# Revit family: ATK_ST_SFD_Pile (NEW)
name_source: partatom
category: Structural Foundations
units: mm (PartAtom-declared; Revit-internal decimal feet)

## family parameters
Always vertical = Yes
Cap = No
Cut with Voids When Loaded = No
Material for Model Behavior = Concrete
Shared = Yes
Work Plane-Based = No

## types (170) — shared parameters
31 = Pile Type-30
Assembly Code = A1020130
Minimum Embedment = 75 mm
Pile Type = Pile Type-30
Type Comments = Z2
Width = 1000 mm  [stored 3.28084 ft]

## per-type parameters (varying)
- ATK_P3A_1000_Diameter_Pile: ATK_1.25DIA_Circle_Radius=1250 mm  [stored 4.10105 ft]; ATK_2.5_DIA_Circle_Radius=2500 mm  [stored 8.2021 ft]; ATK_Pile_DIA=1000 mm  [stored 3.28084 ft]; Band Width 2=240 mm; Band Width 3=100 mm  [stored 0.328084 ft]; Depth=15000 mm  [stored 49.2126 ft]; Pile Type 01=Yes; Pile Type 02=No; Pile Type 03=No; Pile Type 04=No; Pile Type 05=No; Pile Type 06=No; Pile Type 07=No; Pile Type 08=No; Pile Type 09=No; Pile Type 10=No; Pile Type 11=No; Pile Type 12=No; Pile Type 13=No; Pile Type 14=No; Pile Type 15=No; Pile Type 16=No; Pile Type 17=No; Pile Type 18=No; Pile Type 19=No; Pile Type 20=No; Pile Type 21=No; Pile Type 22=No; Pile Type 23=No; Pile Type 24=No; Pile Type 25=No; Pile Type 26=No; Pile Type 27=No; Pile Type 28=No; Pile Type 29=No; Pile Type 30=No; Pile Type 31=Yes; Pile Type-32=No; Pile Type-33=No; Pile Type-34=No; Pile Type-35=No; Pile Type-36=No; Pile Type-37=Yes; Pile Type-38=No; Pile Type-39=No; Pile Type-40=No; Pile Type-41=No; Pile Type-42=No; Pile Type-43=No; Pile Type-44=No; Pile Type-45=No; Pile Type-46=No; Pile Type-47=No; Pile Type-48=No; Pile Type-49=No; Pile Type-50=No; Pile Type-51=No; Pile Type-52=No; Pile Type-53=No; Pile Type-54=No; Radius=500 mm  [stored 1.64042 ft]; Radius/2=250 mm  [stored 0.82021 ft]; band width=167 mm
- ATK_P7A_1000_Diameter_Pile: ATK_1.25DIA_Circle_Radius=1250 mm  [stored 4.10105 ft]; ATK_2.5_DIA_Circle_Radius=2500 mm  [stored 8.2021 ft]; ATK_Pile_DIA=1000 mm  [stored 3.28084 ft]; Band Width 2=240 mm; Band Width 3=100 mm  [stored 0.328084 ft]; Depth=19000 mm; Pile Type 01=No; Pile Type 02=No; Pile Type 03=No; Pile Type 04=No; Pile Type 05=No; Pile Type 06=No; Pile Type 07=No; Pile Type 08=No; Pile Type 09=No; Pile Type 10=No; Pile Type 11=No; Pile Type 12=No; Pile Type 13=No; Pile Type 14=No; Pile Type 15=No; Pile Type 16=No; Pile Type 17=No; Pile Type 18=No; Pile Type 19=No; Pile Type 20=No; Pile Type 21=No; Pile Type 22=No; Pile Type 23=No; Pile Type 24=No; Pile Type 25=Yes; Pile Type 26=No; Pile Type 27=No; Pile Type 28=No; Pile Type 29=No; Pile Type 30=No; Pile Type 31=Yes; Pile Type-32=No; Pile Type-33=No; Pile Type-34=No; Pile Type-35=No; Pile Type-36=No; Pile Type-37=Yes; Pile Type-38=No; Pile Type-39=No; Pile Type-40=No; Pile Type-41=No; Pile Type-42=No; Pile Type-43=No; Pile Type-44=No; Pile Type-45=No; Pile Type-46=No; Pile Type-47=No; Pile Type-48=No; Pile Type-49=No; Pile Type-50=No; Pile Type-51=No; Pile Type-52=No; Pile Type-53=No; Pile Type-54=No; Radius=500 mm  [stored 1.64042 ft]; Radius/2=250 mm  [stored 0.82021 ft]; band width=167 mm
- ATK_P8A_1000_Diameter_Pile: ATK_1.25DIA_Circle_Radius=1250 mm  [stored 4.10105 ft]; ATK_2.5_DIA_Circle_Radius=2500 mm  [stored 8.2021 ft]; ATK_Pile_DIA=1000 mm  [stored 3.28084 ft]; Band Width 2=240 mm; Band Width 3=100 mm  [stored 0.328084 ft]; Depth=20000 mm  [stored 65.6168 ft]; Pile Type 01=No; Pile Type 02=No; Pile Type 03=No; Pile Type 04=No; Pile Type 05=No; Pile Type 06=No; Pile Type 07=No; Pile Type 08=No; Pile Type 09=No; Pile Type 10=No; Pile Type 11=No; Pile Type 12=No; Pile Type 13=No; Pile Type 14=No; Pile Type 15=No; Pile Type 16=No; Pile Type 17=No; Pile Type 18=No; Pile Type 19=No; Pile Type 20=No; Pile Type 21=No; Pile Type 22=No; Pile Type 23=No; Pile Type 24=No; Pile Type 25=No; Pile Type 26=No; Pile Type 27=No; Pile Type 28=No; Pile Type 29=Yes; Pile Type 30=No; Pile Type 31=Yes; Pile Type-32=No; Pile Type-33=No; Pile Type-34=No; Pile Type-35=No; Pile Type-36=No; Pile Type-37=Yes; Pile Type-38=No; Pile Type-39=No; Pile Type-40=No; Pile Type-41=No; Pile Type-42=No; Pile Type-43=No; Pile Type-44=No; Pile Type-45=No; Pile Type-46=No; Pile Type-47=No; Pile Type-48=No; Pile Type-49=No; Pile Type-50=No; Pile Type-51=No; Pile Type-52=No; Pile Type-53=No; Pile Type-54=No; Radius=500 mm  [stored 1.64042 ft]; Radius/2=250 mm  [stored 0.82021 ft]; band width=167 mm
- ATK_P9A_1000_Diameter_Pile 2: ATK_1.25DIA_Circle_Radius=1250 mm  [stored 4.10105 ft]; ATK_2.5_DIA_Circle_Radius=2500 mm  [stored 8.2021 ft]; ATK_Pile_DIA=1000 mm  [stored 3.28084 ft]; Band Width 2=240 mm; Band Width 3=100 mm  [stored 0.328084 ft]; Depth=21000 mm  [stored 68.8976 ft]; Pile Type 01=No; Pile Type 02=No; Pile Type 03=No; Pile Type 04=No; Pile Type 05=No; Pile Type 06=No; Pile Type 07=No; Pile Type 08=No; Pile Type 09=No; Pile Type 10=No; Pile Type 11=No; Pile Type 12=No; Pile Type 13=No; Pile Type 14=No; Pile Type 15=No; Pile Type 16=No; Pile Type 17=No; Pile Type 18=No; Pile Type 19=No; Pile Type 20=No; Pile Type 21=No; Pile Type 22=No; Pile Type 23=Yes; Pile Type 24=No; Pile Type 25=No; Pile Type 26=No; Pile Type 27=No; Pile Type 28=No; Pile Type 29=No; Pile Type 30=No; Pile Type 31=Yes; Pile Type-32=No; Pile Type-33=No; Pile Type-34=No; Pile Type-35=No; Pile Type-36=No; Pile Type-37=Yes; Pile Type-38=No; Pile Type-39=No; Pile Type-40=No; Pile Type-41=No; Pile Type-42=No; Pile Type-43=No; Pile Type-44=No; Pile Type-45=No; Pile Type-46=No; Pile Type-47=No; Pile Type-48=No; Pile Type-49=No; Pile Type-50=No; Pile Type-51=No; Pile Type-52=No; Pile Type-53=No; Pile Type-54=No; Radius=500 mm  [stored 1.64042 ft]; Radius/2=250 mm  [stored 0.82021 ft]; band width=167 mm
- ATK_P4B_900_Diameter_Pile 6: ATK_1.25DIA_Circle_Radius=1125 mm; ATK_2.5_DIA_Circle_Radius=2250 mm; ATK_Pile_DIA=900 mm  [stored 2.95276 ft]; Band Width 2=215 mm; Band Width 3=90 mm; Depth=16000 mm  [stored 52.4934 ft]; Pile Type 01=No; Pile Type 02=Yes; Pile Type 03=No; Pile Type 04=No; Pile Type 05=No; Pile Type 06=No; Pile Type 07=No; Pile Type 08=No; Pile Type 09=No; Pile Type 10=No; Pile Type 11=No; Pile Type 12=No; Pile Type 13=No; Pile Type 14=No; Pile Type 15=No; Pile Type 16=No; Pile Type 17=No; Pile Type 18=No; Pile Type 19=No; Pile Type 20=No; Pile Type 21=No; Pile Type 22=No; Pile Type 23=No; Pile Type 24=No; Pile Type 25=No; Pile Type 26=No; Pile Type 27=No; Pile Type 28=No; Pile Type 29=No; Pile Type 30=No; Pile Type 31=Yes; Pile Type-32=No; Pile Type-33=No; Pile Type-34=No; Pile Type-35=No; Pile Type-36=No; Pile Type-37=Yes; Pile Type-38=No; Pile Type-39=No; Pile Type-40=No; Pile Type-41=No; Pile Type-42=No; Pile Type-43=No; Pile Type-44=No; Pile Type-45=No; Pile Type-46=No; Pile Type-47=No; Pile Type-48=No; Pile Type-49=No; Pile Type-50=No; Pile Type-51=No; Pile Type-52=No; Pile Type-53=No; Pile Type-54=No; Radius=450 mm  [stored 1.47638 ft]; Radius/2=225 mm  [stored 0.738189 ft]; band width=150 mm
- ATK_P3B_900_Diameter_Pile 6: ATK_1.25DIA_Circle_Radius=1125 mm; ATK_2.5_DIA_Circle_Radius=2250 mm; ATK_Pile_DIA=900 mm  [stored 2.95276 ft]; Band Width 2=215 mm; Band Width 3=90 mm; Depth=15000 mm  [stored 49.2126 ft]; Pile Type 01=No; Pile Type 02=No; Pile Type 03=No; Pile Type 04=No; Pile Type 05=No; Pile Type 06=No; Pile Type 07=Yes; Pile Type 08=No; Pile Type 09=No; Pile Type 10=No; Pile Type 11=No; Pile Type 12=No; Pile Type 13=No; Pile Type 14=No; Pile Type 15=No; Pile Type 16=No; Pile Type 17=No; Pile Type 18=No; Pile Type 19=No; Pile Type 20=No; Pile Type 21=No; Pile Type 22=No; Pile Type 23=No; Pile Type 24=No; Pile Type 25=No; Pile Type 26=No; Pile Type 27=No; Pile Type 28=No; Pile Type 29=No; Pile Type 30=No; Pile Type 31=Yes; Pile Type-32=No; Pile Type-33=No; Pile Type-34=No; Pile Type-35=No; Pile Type-36=No; Pile Type-37=Yes; Pile Type-38=No; Pile Type-39=No; Pile Type-40=No; Pile Type-41=No; Pile Type-42=No; Pile Type-43=No; Pile Type-44=No; Pile Type-45=No; Pile Type-46=No; Pile Type-47=No; Pile Type-48=No; Pile Type-49=No; Pile Type-50=No; Pile Type-51=No; Pile Type-52=No; Pile Type-53=No; Pile Type-54=No; Radius=450 mm  [stored 1.47638 ft]; Radius/2=225 mm  [stored 0.738189 ft]; band width=150 mm
- ATK_P2B_900_Diameter_Pile 5: ATK_1.25DIA_Circle_Radius=1125 mm; ATK_2.5_DIA_Circle_Radius=2250 mm; ATK_Pile_DIA=900 mm  [stored 2.95276 ft]; Band Width 2=215 mm; Band Width 3=90 mm; Depth=14000 mm  [stored 45.9318 ft]; Pile Type 01=No; Pile Type 02=No; Pile Type 03=Yes; Pile Type 04=No; Pile Type 05=No; Pile Type 06=No; Pile Type 07=No; Pile Type 08=No; Pile Type 09=No; Pile Type 10=No; Pile Type 11=No; Pile Type 12=No; Pile Type 13=No; Pile Type 14=No; Pile Type 15=No; Pile Type 16=No; Pile Type 17=No; Pile Type 18=No; Pile Type 19=No; Pile Type 20=No; Pile Type 21=No; Pile Type 22=No; Pile Type 23=No; Pile Type 24=No; Pile Type 25=No; Pile Type 26=No; Pile Type 27=No; Pile Type 28=No; Pile Type 29=No; Pile Type 30=No; Pile Type 31=Yes; Pile Type-32=No; Pile Type-33=No; Pile Type-34=No; Pile Type-35=No; Pile Type-36=No; Pile Type-37=Yes; Pile Type-38=No; Pile Type-39=No; Pile Type-40=No; Pile Type-41=No; Pile Type-42=No; Pile Type-43=No; Pile Type-44=No; Pile Type-45=No; Pile Type-46=No; Pile Type-47=No; Pile Type-48=No; Pile Type-49=No; Pile Type-50=No; Pile Type-51=No; Pile Type-52=No; Pile Type-53=No; Pile Type-54=No; Radius=450 mm  [stored 1.47638 ft]; Radius/2=225 mm  [stored 0.738189 ft]; band width=150 mm
- ATK_P6C_750_Diameter_Pile 2: ATK_1.25DIA_Circle_Radius=938 mm; ATK_2.5_DIA_Circle_Radius=1875 mm  [stored 6.15157 ft]; ATK_Pile_DIA=750 mm  [stored 2.46063 ft]; Band Width 2=178 mm; Band Width 3=75 mm; Depth=18000 mm; Pile Type 01=No; Pile Type 02=No; Pile Type 03=No; Pile Type 04=No; Pile Type 05=No; Pile Type 06=Yes; Pile Type 07=No; Pile Type 08=No; Pile Type 09=No; Pile Type 10=No; Pile Type 11=No; Pile Type 12=No; Pile Type 13=No; Pile Type 14=No; Pile Type 15=No; Pile Type 16=No; Pile Type 17=No; Pile Type 18=No; Pile Type 19=No; Pile Type 20=No; Pile Type 21=No; Pile Type 22=No; Pile Type 23=No; Pile Type 24=No; Pile Type 25=No; Pile Type 26=No; Pile Type 27=No; Pile Type 28=No; Pile Type 29=No; Pile Type 30=No; Pile Type 31=Yes; Pile Type-32=No; Pile Type-33=No; Pile Type-34=No; Pile Type-35=No; Pile Type-36=No; Pile Type-37=Yes; Pile Type-38=No; Pile Type-39=No; Pile Type-40=No; Pile Type-41=No; Pile Type-42=No; Pile Type-43=No; Pile Type-44=No; Pile Type-45=No; Pile Type-46=No; Pile Type-47=No; Pile Type-48=No; Pile Type-49=No; Pile Type-50=No; Pile Type-51=No; Pile Type-52=No; Pile Type-53=No; Pile Type-54=No; Radius=375 mm  [stored 1.23031 ft]; Radius/2=188 mm; band width=125 mm  [stored 0.410105 ft]
- ATK_P5C_750_Diameter_Pile 2: ATK_1.25DIA_Circle_Radius=938 mm; ATK_2.5_DIA_Circle_Radius=1875 mm  [stored 6.15157 ft]; ATK_Pile_DIA=750 mm  [stored 2.46063 ft]; Band Width 2=178 mm; Band Width 3=75 mm; Depth=17000 mm; Pile Type 01=No; Pile Type 02=No; Pile Type 03=No; Pile Type 04=No; Pile Type 05=No; Pile Type 06=No; Pile Type 07=No; Pile Type 08=Yes; Pile Type 09=No; Pile Type 10=No; Pile Type 11=No; Pile Type 12=No; Pile Type 13=No; Pile Type 14=No; Pile Type 15=No; Pile Type 16=No; Pile Type 17=No; Pile Type 18=No; Pile Type 19=No; Pile Type 20=No; Pile Type 21=No; Pile Type 22=No; Pile Type 23=No; Pile Type 24=No; Pile Type 25=No; Pile Type 26=No; Pile Type 27=No; Pile Type 28=No; Pile Type 29=No; Pile Type 30=No; Pile Type 31=Yes; Pile Type-32=No; Pile Type-33=No; Pile Type-34=No; Pile Type-35=No; Pile Type-36=No; Pile Type-37=Yes; Pile Type-38=No; Pile Type-39=No; Pile Type-40=No; Pile Type-41=No; Pile Type-42=No; Pile Type-43=No; Pile Type-44=No; Pile Type-45=No; Pile Type-46=No; Pile Type-47=No; Pile Type-48=No; Pile Type-49=No; Pile Type-50=No; Pile Type-51=No; Pile Type-52=No; Pile Type-53=No; Pile Type-54=No; Radius=375 mm  [stored 1.23031 ft]; Radius/2=188 mm; band width=125 mm  [stored 0.410105 ft]
- ATK_P4C_750_Diameter_Pile 2: ATK_1.25DIA_Circle_Radius=938 mm; ATK_2.5_DIA_Circle_Radius=1875 mm  [stored 6.15157 ft]; ATK_Pile_DIA=750 mm  [stored 2.46063 ft]; Band Width 2=178 mm; Band Width 3=75 mm; Depth=16000 mm  [stored 52.4934 ft]; Pile Type 01=No; Pile Type 02=No; Pile Type 03=No; Pile Type 04=No; Pile Type 05=No; Pile Type 06=No; Pile Type 07=No; Pile Type 08=No; Pile Type 09=No; Pile Type 10=No; Pile Type 11=No; Pile Type 12=Yes; Pile Type 13=No; Pile Type 14=No; Pile Type 15=No; Pile Type 16=No; Pile Type 17=No; Pile Type 18=No; Pile Type 19=No; Pile Type 20=No; Pile Type 21=No; Pile Type 22=No; Pile Type 23=No; Pile Type 24=No; Pile Type 25=No; Pile Type 26=No; Pile Type 27=No; Pile Type 28=No; Pile Type 29=No; Pile Type 30=No; Pile Type 31=Yes; Pile Type-32=No; Pile Type-33=No; Pile Type-34=No; Pile Type-35=No; Pile Type-36=No; Pile Type-37=Yes; Pile Type-38=No; Pile Type-39=No; Pile Type-40=No; Pile Type-41=No; Pile Type-42=No; Pile Type-43=No; Pile Type-44=No; Pile Type-45=No; Pile Type-46=No; Pile Type-47=No; Pile Type-48=No; Pile Type-49=No; Pile Type-50=No; Pile Type-51=No; Pile Type-52=No; Pile Type-53=No; Pile Type-54=No; Radius=375 mm  [stored 1.23031 ft]; Radius/2=188 mm; band width=125 mm  [stored 0.410105 ft]
- ATK_P3C_750_Diameter_Pile 2: ATK_1.25DIA_Circle_Radius=938 mm; ATK_2.5_DIA_Circle_Radius=1875 mm  [stored 6.15157 ft]; ATK_Pile_DIA=750 mm  [stored 2.46063 ft]; Band Width 2=178 mm; Band Width 3=75 mm; Depth=15000 mm  [stored 49.2126 ft]; Pile Type 01=No; Pile Type 02=No; Pile Type 03=No; Pile Type 04=No; Pile Type 05=No; Pile Type 06=No; Pile Type 07=No; Pile Type 08=No; Pile Type 09=No; Pile Type 10=No; Pile Type 11=No; Pile Type 12=No; Pile Type 13=Yes; Pile Type 14=No; Pile Type 15=No; Pile Type 16=No; Pile Type 17=No; Pile Type 18=No; Pile Type 19=No; Pile Type 20=No; Pile Type 21=No; Pile Type 22=No; Pile Type 23=No; Pile Type 24=No; Pile Type 25=No; Pile Type 26=No; Pile Type 27=No; Pile Type 28=No; Pile Type 29=No; Pile Type 30=No; Pile Type 31=Yes; Pile Type-32=No; Pile Type-33=No; Pile Type-34=No; Pile Type-35=No; Pile Type-36=No; Pile Type-37=Yes; Pile Type-38=No; Pile Type-39=No; Pile Type-40=No; Pile Type-41=No; Pile Type-42=No; Pile Type-43=No; Pile Type-44=No; Pile Type-45=No; Pile Type-46=No; Pile Type-47=No; Pile Type-48=No; Pile Type-49=No; Pile Type-50=No; Pile Type-51=No; Pile Type-52=No; Pile Type-53=No; Pile Type-54=No; Radius=375 mm  [stored 1.23031 ft]; Radius/2=188 mm; band width=125 mm  [stored 0.410105 ft]
- ATK_P2C_750_Diameter_Pile: ATK_1.25DIA_Circle_Radius=938 mm; ATK_2.5_DIA_Circle_Radius=1875 mm  [stored 6.15157 ft]; ATK_Pile_DIA=750 mm  [stored 2.46063 ft]; Band Width 2=178 mm; Band Width 3=75 mm; Depth=14000 mm  [stored 45.9318 ft]; Pile Type 01=No; Pile Type 02=No; Pile Type 03=No; Pile Type 04=No; Pile Type 05=No; Pile Type 06=No; Pile Type 07=No; Pile Type 08=No; Pile Type 09=No; Pile Type 10=No; Pile Type 11=No; Pile Type 12=No; Pile Type 13=No; Pile Type 14=Yes; Pile Type 15=No; Pile Type 16=No; Pile Type 17=No; Pile Type 18=No; Pile Type 19=No; Pile Type 20=No; Pile Type 21=No; Pile Type 22=No; Pile Type 23=No; Pile Type 24=No; Pile Type 25=No; Pile Type 26=No; Pile Type 27=No; Pile Type 28=No; Pile Type 29=No; Pile Type 30=No; Pile Type 31=Yes; Pile Type-32=No; Pile Type-33=No; Pile Type-34=No; Pile Type-35=No; Pile Type-36=No; Pile Type-37=Yes; Pile Type-38=No; Pile Type-39=No; Pile Type-40=No; Pile Type-41=No; Pile Type-42=No; Pile Type-43=No; Pile Type-44=No; Pile Type-45=No; Pile Type-46=No; Pile Type-47=No; Pile Type-48=No; Pile Type-49=No; Pile Type-50=No; Pile Type-51=No; Pile Type-52=No; Pile Type-53=No; Pile Type-54=No; Radius=375 mm  [stored 1.23031 ft]; Radius/2=188 mm; band width=125 mm  [stored 0.410105 ft]
- ATK_P5B_900_Diameter_Pile 3: ATK_1.25DIA_Circle_Radius=1125 mm; ATK_2.5_DIA_Circle_Radius=2250 mm; ATK_Pile_DIA=900 mm  [stored 2.95276 ft]; Band Width 2=215 mm; Band Width 3=90 mm; Depth=17000 mm; Pile Type 01=No; Pile Type 02=No; Pile Type 03=No; Pile Type 04=No; Pile Type 05=No; Pile Type 06=No; Pile Type 07=No; Pile Type 08=No; Pile Type 09=No; Pile Type 10=No; Pile Type 11=No; Pile Type 12=No; Pile Type 13=No; Pile Type 14=No; Pile Type 15=No; Pile Type 16=No; Pile Type 17=No; Pile Type 18=No; Pile Type 19=No; Pile Type 20=Yes; Pile Type 21=No; Pile Type 22=No; Pile Type 23=No; Pile Type 24=No; Pile Type 25=No; Pile Type 26=No; Pile Type 27=No; Pile Type 28=No; Pile Type 29=No; Pile Type 30=No; Pile Type 31=Yes; Pile Type-32=No; Pile Type-33=No; Pile Type-34=No; Pile Type-35=No; Pile Type-36=No; Pile Type-37=Yes; Pile Type-38=No; Pile Type-39=No; Pile Type-40=No; Pile Type-41=No; Pile Type-42=No; Pile Type-43=No; Pile Type-44=No; Pile Type-45=No; Pile Type-46=No; Pile Type-47=No; Pile Type-48=No; Pile Type-49=No; Pile Type-50=No; Pile Type-51=No; Pile Type-52=No; Pile Type-53=No; Pile Type-54=No; Radius=450 mm  [stored 1.47638 ft]; Radius/2=225 mm  [stored 0.738189 ft]; band width=150 mm
- ATK_P6A_1000_Diameter_Pile 2: ATK_1.25DIA_Circle_Radius=1250 mm  [stored 4.10105 ft]; ATK_2.5_DIA_Circle_Radius=2500 mm  [stored 8.2021 ft]; ATK_Pile_DIA=1000 mm  [stored 3.28084 ft]; Band Width 2=240 mm; Band Width 3=100 mm  [stored 0.328084 ft]; Depth=18000 mm; Pile Type 01=No; Pile Type 02=No; Pile Type 03=No; Pile Type 04=No; Pile Type 05=No; Pile Type 06=No; Pile Type 07=No; Pile Type 08=No; Pile Type 09=No; Pile Type 10=No; Pile Type 11=No; Pile Type 12=No; Pile Type 13=No; Pile Type 14=No; Pile Type 15=No; Pile Type 16=Yes; Pile Type 17=No; Pile Type 18=No; Pile Type 19=No; Pile Type 20=No; Pile Type 21=No; Pile Type 22=No; Pile Type 23=No; Pile Type 24=No; Pile Type 25=No; Pile Type 26=No; Pile Type 27=No; Pile Type 28=No; Pile Type 29=No; Pile Type 30=No; Pile Type 31=Yes; Pile Type-32=No; Pile Type-33=No; Pile Type-34=No; Pile Type-35=No; Pile Type-36=No; Pile Type-37=Yes; Pile Type-38=No; Pile Type-39=No; Pile Type-40=No; Pile Type-41=No; Pile Type-42=No; Pile Type-43=No; Pile Type-44=No; Pile Type-45=No; Pile Type-46=No; Pile Type-47=No; Pile Type-48=No; Pile Type-49=No; Pile Type-50=No; Pile Type-51=No; Pile Type-52=No; Pile Type-53=No; Pile Type-54=No; Radius=500 mm  [stored 1.64042 ft]; Radius/2=250 mm  [stored 0.82021 ft]; band width=167 mm
- ATK_P5A_1000_Diameter_Pile 2: ATK_1.25DIA_Circle_Radius=1250 mm  [stored 4.10105 ft]; ATK_2.5_DIA_Circle_Radius=2500 mm  [stored 8.2021 ft]; ATK_Pile_DIA=1000 mm  [stored 3.28084 ft]; Band Width 2=240 mm; Band Width 3=100 mm  [stored 0.328084 ft]; Depth=17000 mm; Pile Type 01=No; Pile Type 02=No; Pile Type 03=No; Pile Type 04=No; Pile Type 05=No; Pile Type 06=No; Pile Type 07=No; Pile Type 08=No; Pile Type 09=No; Pile Type 10=No; Pile Type 11=No; Pile Type 12=No; Pile Type 13=No; Pile Type 14=No; Pile Type 15=No; Pile Type 16=No; Pile Type 17=No; Pile Type 18=No; Pile Type 19=No; Pile Type 20=No; Pile Type 21=No; Pile Type 22=No; Pile Type 23=No; Pile Type 24=No; Pile Type 25=No; Pile Type 26=No; Pile Type 27=Yes; Pile Type 28=No; Pile Type 29=No; Pile Type 30=No; Pile Type 31=Yes; Pile Type-32=No; Pile Type-33=No; Pile Type-34=No; Pile Type-35=No; Pile Type-36=No; Pile Type-37=Yes; Pile Type-38=No; Pile Type-39=No; Pile Type-40=No; Pile Type-41=No; Pile Type-42=No; Pile Type-43=No; Pile Type-44=No; Pile Type-45=No; Pile Type-46=No; Pile Type-47=No; Pile Type-48=No; Pile Type-49=No; Pile Type-50=No; Pile Type-51=No; Pile Type-52=No; Pile Type-53=No; Pile Type-54=No; Radius=500 mm  [stored 1.64042 ft]; Radius/2=250 mm  [stored 0.82021 ft]; band width=167 mm
- ATK_P4A_1000_Diameter_Pile 2: ATK_1.25DIA_Circle_Radius=1250 mm  [stored 4.10105 ft]; ATK_2.5_DIA_Circle_Radius=2500 mm  [stored 8.2021 ft]; ATK_Pile_DIA=1000 mm  [stored 3.28084 ft]; Band Width 2=240 mm; Band Width 3=100 mm  [stored 0.328084 ft]; Depth=16000 mm  [stored 52.4934 ft]; Pile Type 01=No; Pile Type 02=No; Pile Type 03=No; Pile Type 04=No; Pile Type 05=No; Pile Type 06=No; Pile Type 07=No; Pile Type 08=No; Pile Type 09=No; Pile Type 10=No; Pile Type 11=No; Pile Type 12=No; Pile Type 13=No; Pile Type 14=No; Pile Type 15=No; Pile Type 16=No; Pile Type 17=No; Pile Type 18=No; Pile Type 19=No; Pile Type 20=No; Pile Type 21=No; Pile Type 22=No; Pile Type 23=No; Pile Type 24=No; Pile Type 25=No; Pile Type 26=No; Pile Type 27=No; Pile Type 28=Yes; Pile Type 29=No; Pile Type 30=No; Pile Type 31=Yes; Pile Type-32=No; Pile Type-33=No; Pile Type-34=No; Pile Type-35=No; Pile Type-36=No; Pile Type-37=Yes; Pile Type-38=No; Pile Type-39=No; Pile Type-40=No; Pile Type-41=No; Pile Type-42=No; Pile Type-43=No; Pile Type-44=No; Pile Type-45=No; Pile Type-46=No; Pile Type-47=No; Pile Type-48=No; Pile Type-49=No; Pile Type-50=No; Pile Type-51=No; Pile Type-52=No; Pile Type-53=No; Pile Type-54=No; Radius=500 mm  [stored 1.64042 ft]; Radius/2=250 mm  [stored 0.82021 ft]; band width=167 mm
- ATK_P4B2_900_Diameter_Pile 7: ATK_1.25DIA_Circle_Radius=1125 mm; ATK_2.5_DIA_Circle_Radius=2250 mm; ATK_Pile_DIA=900 mm  [stored 2.95276 ft]; Band Width 2=215 mm; Band Width 3=90 mm; Depth=16000 mm  [stored 52.4934 ft]; Pile Type 01=No; Pile Type 02=No; Pile Type 03=No; Pile Type 04=No; Pile Type 05=No; Pile Type 06=No; Pile Type 07=No; Pile Type 08=No; Pile Type 09=No; Pile Type 10=No; Pile Type 11=Yes; Pile Type 12=Yes; Pile Type 13=No; Pile Type 14=No; Pile Type 15=No; Pile Type 16=No; Pile Type 17=No; Pile Type 18=No; Pile Type 19=No; Pile Type 20=No; Pile Type 21=No; Pile Type 22=No; Pile Type 23=No; Pile Type 24=No; Pile Type 25=No; Pile Type 26=No; Pile Type 27=No; Pile Type 28=No; Pile Type 29=No; Pile Type 30=No; Pile Type 31=Yes; Pile Type-32=No; Pile Type-33=No; Pile Type-34=No; Pile Type-35=No; Pile Type-36=No; Pile Type-37=Yes; Pile Type-38=No; Pile Type-39=No; Pile Type-40=No; Pile Type-41=No; Pile Type-42=No; Pile Type-43=No; Pile Type-44=No; Pile Type-45=No; Pile Type-46=No; Pile Type-47=No; Pile Type-48=No; Pile Type-49=No; Pile Type-50=No; Pile Type-51=No; Pile Type-52=No; Pile Type-53=No; Pile Type-54=No; Radius=450 mm  [stored 1.47638 ft]; Radius/2=225 mm  [stored 0.738189 ft]; band width=150 mm
- ATK_P5B2_900_Diameter_Pile 4: ATK_1.25DIA_Circle_Radius=1125 mm; ATK_2.5_DIA_Circle_Radius=2250 mm; ATK_Pile_DIA=900 mm  [stored 2.95276 ft]; Band Width 2=215 mm; Band Width 3=90 mm; Depth=17000 mm; Pile Type 01=No; Pile Type 02=No; Pile Type 03=No; Pile Type 04=No; Pile Type 05=No; Pile Type 06=No; Pile Type 07=No; Pile Type 08=No; Pile Type 09=No; Pile Type 10=No; Pile Type 11=No; Pile Type 12=No; Pile Type 13=No; Pile Type 14=No; Pile Type 15=No; Pile Type 16=No; Pile Type 17=No; Pile Type 18=No; Pile Type 19=No; Pile Type 20=No; Pile Type 21=No; Pile Type 22=No; Pile Type 23=No; Pile Type 24=No; Pile Type 25=No; Pile Type 26=Yes; Pile Type 27=No; Pile Type 28=No; Pile Type 29=No; Pile Type 30=No; Pile Type 31=Yes; Pile Type-32=No; Pile Type-33=No; Pile Type-34=No; Pile Type-35=No; Pile Type-36=No; Pile Type-37=Yes; Pile Type-38=No; Pile Type-39=No; Pile Type-40=No; Pile Type-41=No; Pile Type-42=No; Pile Type-43=No; Pile Type-44=No; Pile Type-45=No; Pile Type-46=No; Pile Type-47=No; Pile Type-48=No; Pile Type-49=No; Pile Type-50=No; Pile Type-51=No; Pile Type-52=No; Pile Type-53=No; Pile Type-54=No; Radius=450 mm  [stored 1.47638 ft]; Radius/2=225 mm  [stored 0.738189 ft]; band width=150 mm
- ATK_P5A4_1000_Diameter_Pile 4: ATK_1.25DIA_Circle_Radius=1250 mm  [stored 4.10105 ft]; ATK_2.5_DIA_Circle_Radius=2500 mm  [stored 8.2021 ft]; ATK_Pile_DIA=1000 mm  [stored 3.28084 ft]; Band Width 2=240 mm; Band Width 3=100 mm  [stored 0.328084 ft]; Depth=17000 mm; Pile Type 01=No; Pile Type 02=No; Pile Type 03=No; Pile Type 04=No; Pile Type 05=No; Pile Type 06=No; Pile Type 07=No; Pile Type 08=No; Pile Type 09=No; Pile Type 10=No; Pile Type 11=Yes; Pile Type 12=No; Pile Type 13=No; Pile Type 14=No; Pile Type 15=No; Pile Type 16=No; Pile Type 17=No; Pile Type 18=No; Pile Type 19=No; Pile Type 20=No; Pile Type 21=No; Pile Type 22=No; Pile Type 23=No; Pile Type 24=No; Pile Type 25=No; Pile Type 26=No; Pile Type 27=No; Pile Type 28=No; Pile Type 29=No; Pile Type 30=No; Pile Type 31=Yes; Pile Type-32=No; Pile Type-33=No; Pile Type-34=No; Pile Type-35=No; Pile Type-36=No; Pile Type-37=Yes; Pile Type-38=No; Pile Type-39=No; Pile Type-40=No; Pile Type-41=No; Pile Type-42=No; Pile Type-43=No; Pile Type-44=No; Pile Type-45=No; Pile Type-46=No; Pile Type-47=No; Pile Type-48=No; Pile Type-49=No; Pile Type-50=No; Pile Type-51=No; Pile Type-52=No; Pile Type-53=No; Pile Type-54=No; Radius=500 mm  [stored 1.64042 ft]; Radius/2=250 mm  [stored 0.82021 ft]; band width=167 mm
- ATK_P6A1_1000_Diameter_Pile 3: ATK_1.25DIA_Circle_Radius=1250 mm  [stored 4.10105 ft]; ATK_2.5_DIA_Circle_Radius=2500 mm  [stored 8.2021 ft]; ATK_Pile_DIA=1000 mm  [stored 3.28084 ft]; Band Width 2=240 mm; Band Width 3=100 mm  [stored 0.328084 ft]; Depth=18000 mm; Pile Type 01=No; Pile Type 02=No; Pile Type 03=No; Pile Type 04=No; Pile Type 05=No; Pile Type 06=No; Pile Type 07=No; Pile Type 08=No; Pile Type 09=No; Pile Type 10=No; Pile Type 11=No; Pile Type 12=No; Pile Type 13=No; Pile Type 14=No; Pile Type 15=No; Pile Type 16=No; Pile Type 17=No; Pile Type 18=No; Pile Type 19=Yes; Pile Type 20=No; Pile Type 21=No; Pile Type 22=No; Pile Type 23=No; Pile Type 24=No; Pile Type 25=No; Pile Type 26=No; Pile Type 27=No; Pile Type 28=No; Pile Type 29=No; Pile Type 30=No; Pile Type 31=Yes; Pile Type-32=No; Pile Type-33=No; Pile Type-34=No; Pile Type-35=No; Pile Type-36=No; Pile Type-37=Yes; Pile Type-38=No; Pile Type-39=No; Pile Type-40=No; Pile Type-41=No; Pile Type-42=No; Pile Type-43=No; Pile Type-44=No; Pile Type-45=No; Pile Type-46=No; Pile Type-47=No; Pile Type-48=No; Pile Type-49=No; Pile Type-50=No; Pile Type-51=No; Pile Type-52=No; Pile Type-53=No; Pile Type-54=No; Radius=500 mm  [stored 1.64042 ft]; Radius/2=250 mm  [stored 0.82021 ft]; band width=167 mm
- ATK_P5C1_750_Diameter_Pile 3: ATK_1.25DIA_Circle_Radius=938 mm; ATK_2.5_DIA_Circle_Radius=1875 mm  [stored 6.15157 ft]; ATK_Pile_DIA=750 mm  [stored 2.46063 ft]; Band Width 2=178 mm; Band Width 3=75 mm; Depth=17000 mm; Pile Type 01=No; Pile Type 02=No; Pile Type 03=No; Pile Type 04=No; Pile Type 05=No; Pile Type 06=No; Pile Type 07=No; Pile Type 08=No; Pile Type 09=No; Pile Type 10=No; Pile Type 11=No; Pile Type 12=No; Pile Type 13=No; Pile Type 14=No; Pile Type 15=Yes; Pile Type 16=No; Pile Type 17=No; Pile Type 18=No; Pile Type 19=No; Pile Type 20=No; Pile Type 21=No; Pile Type 22=No; Pile Type 23=No; Pile Type 24=No; Pile Type 25=No; Pile Type 26=No; Pile Type 27=No; Pile Type 28=No; Pile Type 29=No; Pile Type 30=No; Pile Type 31=Yes; Pile Type-32=No; Pile Type-33=No; Pile Type-34=No; Pile Type-35=No; Pile Type-36=No; Pile Type-37=Yes; Pile Type-38=No; Pile Type-39=No; Pile Type-40=No; Pile Type-41=No; Pile Type-42=No; Pile Type-43=No; Pile Type-44=No; Pile Type-45=No; Pile Type-46=No; Pile Type-47=No; Pile Type-48=No; Pile Type-49=No; Pile Type-50=No; Pile Type-51=No; Pile Type-52=No; Pile Type-53=No; Pile Type-54=No; Radius=375 mm  [stored 1.23031 ft]; Radius/2=188 mm; band width=125 mm  [stored 0.410105 ft]
- ATK_P6C1_750_Diameter_Pile 3: ATK_1.25DIA_Circle_Radius=938 mm; ATK_2.5_DIA_Circle_Radius=1875 mm  [stored 6.15157 ft]; ATK_Pile_DIA=750 mm  [stored 2.46063 ft]; Band Width 2=178 mm; Band Width 3=75 mm; Depth=18000 mm; Pile Type 01=No; Pile Type 02=No; Pile Type 03=No; Pile Type 04=No; Pile Type 05=Yes; Pile Type 06=No; Pile Type 07=No; Pile Type 08=No; Pile Type 09=No; Pile Type 10=No; Pile Type 11=No; Pile Type 12=No; Pile Type 13=No; Pile Type 14=No; Pile Type 15=No; Pile Type 16=No; Pile Type 17=No; Pile Type 18=No; Pile Type 19=No; Pile Type 20=No; Pile Type 21=No; Pile Type 22=No; Pile Type 23=No; Pile Type 24=No; Pile Type 25=No; Pile Type 26=No; Pile Type 27=No; Pile Type 28=No; Pile Type 29=No; Pile Type 30=No; Pile Type 31=Yes; Pile Type-32=No; Pile Type-33=No; Pile Type-34=No; Pile Type-35=No; Pile Type-36=No; Pile Type-37=Yes; Pile Type-38=No; Pile Type-39=No; Pile Type-40=No; Pile Type-41=No; Pile Type-42=No; Pile Type-43=No; Pile Type-44=No; Pile Type-45=No; Pile Type-46=No; Pile Type-47=No; Pile Type-48=No; Pile Type-49=No; Pile Type-50=No; Pile Type-51=No; Pile Type-52=No; Pile Type-53=No; Pile Type-54=No; Radius=375 mm  [stored 1.23031 ft]; Radius/2=188 mm; band width=125 mm  [stored 0.410105 ft]
- ATK_P5A3_1000_Diameter_Pile 3: ATK_1.25DIA_Circle_Radius=1250 mm  [stored 4.10105 ft]; ATK_2.5_DIA_Circle_Radius=2500 mm  [stored 8.2021 ft]; ATK_Pile_DIA=1000 mm  [stored 3.28084 ft]; Band Width 2=240 mm; Band Width 3=100 mm  [stored 0.328084 ft]; Depth=17000 mm; Pile Type 01=No; Pile Type 02=No; Pile Type 03=No; Pile Type 04=Yes; Pile Type 05=No; Pile Type 06=No; Pile Type 07=No; Pile Type 08=No; Pile Type 09=No; Pile Type 10=No; Pile Type 11=No; Pile Type 12=No; Pile Type 13=No; Pile Type 14=No; Pile Type 15=No; Pile Type 16=No; Pile Type 17=No; Pile Type 18=No; Pile Type 19=No; Pile Type 20=No; Pile Type 21=No; Pile Type 22=No; Pile Type 23=No; Pile Type 24=No; Pile Type 25=No; Pile Type 26=No; Pile Type 27=No; Pile Type 28=No; Pile Type 29=No; Pile Type 30=No; Pile Type 31=Yes; Pile Type-32=No; Pile Type-33=No; Pile Type-34=No; Pile Type-35=No; Pile Type-36=No; Pile Type-37=Yes; Pile Type-38=No; Pile Type-39=No; Pile Type-40=No; Pile Type-41=No; Pile Type-42=No; Pile Type-43=No; Pile Type-44=No; Pile Type-45=No; Pile Type-46=No; Pile Type-47=No; Pile Type-48=No; Pile Type-49=No; Pile Type-50=No; Pile Type-51=No; Pile Type-52=No; Pile Type-53=No; Pile Type-54=No; Radius=500 mm  [stored 1.64042 ft]; Radius/2=250 mm  [stored 0.82021 ft]; band width=167 mm
- ATK_P5B1_900_Diameter_Pile 8: ATK_1.25DIA_Circle_Radius=1125 mm; ATK_2.5_DIA_Circle_Radius=2250 mm; ATK_Pile_DIA=900 mm  [stored 2.95276 ft]; Band Width 2=215 mm; Band Width 3=90 mm; Depth=17000 mm; Pile Type 01=Yes; Pile Type 02=No; Pile Type 03=No; Pile Type 04=No; Pile Type 05=No; Pile Type 06=No; Pile Type 07=No; Pile Type 08=No; Pile Type 09=No; Pile Type 10=No; Pile Type 11=No; Pile Type 12=No; Pile Type 13=No; Pile Type 14=No; Pile Type 15=No; Pile Type 16=No; Pile Type 17=No; Pile Type 18=No; Pile Type 19=No; Pile Type 20=No; Pile Type 21=No; Pile Type 22=No; Pile Type 23=No; Pile Type 24=No; Pile Type 25=No; Pile Type 26=No; Pile Type 27=No; Pile Type 28=No; Pile Type 29=No; Pile Type 30=No; Pile Type 31=Yes; Pile Type-32=No; Pile Type-33=No; Pile Type-34=No; Pile Type-35=No; Pile Type-36=No; Pile Type-37=Yes; Pile Type-38=No; Pile Type-39=No; Pile Type-40=No; Pile Type-41=No; Pile Type-42=No; Pile Type-43=No; Pile Type-44=No; Pile Type-45=No; Pile Type-46=No; Pile Type-47=No; Pile Type-48=No; Pile Type-49=No; Pile Type-50=No; Pile Type-51=No; Pile Type-52=No; Pile Type-53=No; Pile Type-54=No; Radius=450 mm  [stored 1.47638 ft]; Radius/2=225 mm  [stored 0.738189 ft]; band width=150 mm
- ATK_P4B1_900_Diameter_Pile 7: ATK_1.25DIA_Circle_Radius=1125 mm; ATK_2.5_DIA_Circle_Radius=2250 mm; ATK_Pile_DIA=900 mm  [stored 2.95276 ft]; Band Width 2=215 mm; Band Width 3=90 mm; Depth=16000 mm  [stored 52.4934 ft]; Pile Type 01=No; Pile Type 02=No; Pile Type 03=No; Pile Type 04=No; Pile Type 05=No; Pile Type 06=No; Pile Type 07=No; Pile Type 08=No; Pile Type 09=No; Pile Type 10=Yes; Pile Type 11=No; Pile Type 12=No; Pile Type 13=No; Pile Type 14=No; Pile Type 15=No; Pile Type 16=No; Pile Type 17=No; Pile Type 18=No; Pile Type 19=No; Pile Type 20=No; Pile Type 21=No; Pile Type 22=No; Pile Type 23=No; Pile Type 24=No; Pile Type 25=No; Pile Type 26=No; Pile Type 27=No; Pile Type 28=No; Pile Type 29=No; Pile Type 30=No; Pile Type 31=Yes; Pile Type-32=No; Pile Type-33=No; Pile Type-34=No; Pile Type-35=No; Pile Type-36=No; Pile Type-37=Yes; Pile Type-38=No; Pile Type-39=No; Pile Type-40=No; Pile Type-41=No; Pile Type-42=No; Pile Type-43=No; Pile Type-44=No; Pile Type-45=No; Pile Type-46=No; Pile Type-47=No; Pile Type-48=No; Pile Type-49=No; Pile Type-50=No; Pile Type-51=No; Pile Type-52=No; Pile Type-53=No; Pile Type-54=No; Radius=450 mm  [stored 1.47638 ft]; Radius/2=225 mm  [stored 0.738189 ft]; band width=150 mm
- ATK_P5A2_1000_Diameter_Pile 3: ATK_1.25DIA_Circle_Radius=1250 mm  [stored 4.10105 ft]; ATK_2.5_DIA_Circle_Radius=2500 mm  [stored 8.2021 ft]; ATK_Pile_DIA=1000 mm  [stored 3.28084 ft]; Band Width 2=240 mm; Band Width 3=100 mm  [stored 0.328084 ft]; Depth=17000 mm; Pile Type 01=No; Pile Type 02=No; Pile Type 03=No; Pile Type 04=No; Pile Type 05=No; Pile Type 06=No; Pile Type 07=No; Pile Type 08=No; Pile Type 09=Yes; Pile Type 10=No; Pile Type 11=No; Pile Type 12=No; Pile Type 13=No; Pile Type 14=No; Pile Type 15=No; Pile Type 16=No; Pile Type 17=No; Pile Type 18=No; Pile Type 19=No; Pile Type 20=No; Pile Type 21=No; Pile Type 22=No; Pile Type 23=No; Pile Type 24=No; Pile Type 25=No; Pile Type 26=No; Pile Type 27=No; Pile Type 28=No; Pile Type 29=No; Pile Type 30=No; Pile Type 31=Yes; Pile Type-32=No; Pile Type-33=No; Pile Type-34=No; Pile Type-35=No; Pile Type-36=No; Pile Type-37=Yes; Pile Type-38=No; Pile Type-39=No; Pile Type-40=No; Pile Type-41=No; Pile Type-42=No; Pile Type-43=No; Pile Type-44=No; Pile Type-45=No; Pile Type-46=No; Pile Type-47=No; Pile Type-48=No; Pile Type-49=No; Pile Type-50=No; Pile Type-51=No; Pile Type-52=No; Pile Type-53=No; Pile Type-54=No; Radius=500 mm  [stored 1.64042 ft]; Radius/2=250 mm  [stored 0.82021 ft]; band width=167 mm
- ATK_P5A1_1000_Diameter_Pile 2: ATK_1.25DIA_Circle_Radius=1250 mm  [stored 4.10105 ft]; ATK_2.5_DIA_Circle_Radius=2500 mm  [stored 8.2021 ft]; ATK_Pile_DIA=1000 mm  [stored 3.28084 ft]; Band Width 2=240 mm; Band Width 3=100 mm  [stored 0.328084 ft]; Depth=16000 mm  [stored 52.4934 ft]; Pile Type 01=No; Pile Type 02=No; Pile Type 03=No; Pile Type 04=No; Pile Type 05=No; Pile Type 06=No; Pile Type 07=No; Pile Type 08=No; Pile Type 09=No; Pile Type 10=No; Pile Type 11=No; Pile Type 12=No; Pile Type 13=No; Pile Type 14=No; Pile Type 15=No; Pile Type 16=No; Pile Type 17=No; Pile Type 18=No; Pile Type 19=No; Pile Type 20=Yes; Pile Type 21=Yes; Pile Type 22=No; Pile Type 23=No; Pile Type 24=No; Pile Type 25=No; Pile Type 26=No; Pile Type 27=No; Pile Type 28=No; Pile Type 29=No; Pile Type 30=No; Pile Type 31=Yes; Pile Type-32=No; Pile Type-33=No; Pile Type-34=No; Pile Type-35=No; Pile Type-36=No; Pile Type-37=Yes; Pile Type-38=No; Pile Type-39=No; Pile Type-40=No; Pile Type-41=No; Pile Type-42=No; Pile Type-43=No; Pile Type-44=No; Pile Type-45=No; Pile Type-46=No; Pile Type-47=No; Pile Type-48=No; Pile Type-49=No; Pile Type-50=No; Pile Type-51=No; Pile Type-52=No; Pile Type-53=No; Pile Type-54=No; Radius=500 mm  [stored 1.64042 ft]; Radius/2=250 mm  [stored 0.82021 ft]; band width=167 mm
- ATK_P4C1_750_Diameter_Pile 4: ATK_1.25DIA_Circle_Radius=938 mm; ATK_2.5_DIA_Circle_Radius=1875 mm  [stored 6.15157 ft]; ATK_Pile_DIA=750 mm  [stored 2.46063 ft]; Band Width 2=178 mm; Band Width 3=75 mm; Depth=16000 mm  [stored 52.4934 ft]; Pile Type 01=No; Pile Type 02=No; Pile Type 03=No; Pile Type 04=Yes; Pile Type 05=Yes; Pile Type 06=No; Pile Type 07=No; Pile Type 08=No; Pile Type 09=No; Pile Type 10=No; Pile Type 11=No; Pile Type 12=No; Pile Type 13=No; Pile Type 14=No; Pile Type 15=No; Pile Type 16=No; Pile Type 17=No; Pile Type 18=No; Pile Type 19=No; Pile Type 20=No; Pile Type 21=No; Pile Type 22=No; Pile Type 23=No; Pile Type 24=No; Pile Type 25=No; Pile Type 26=No; Pile Type 27=No; Pile Type 28=No; Pile Type 29=No; Pile Type 30=No; Pile Type 31=Yes; Pile Type-32=No; Pile Type-33=No; Pile Type-34=No; Pile Type-35=No; Pile Type-36=No; Pile Type-37=Yes; Pile Type-38=No; Pile Type-39=No; Pile Type-40=No; Pile Type-41=No; Pile Type-42=No; Pile Type-43=No; Pile Type-44=No; Pile Type-45=No; Pile Type-46=No; Pile Type-47=No; Pile Type-48=No; Pile Type-49=No; Pile Type-50=No; Pile Type-51=No; Pile Type-52=No; Pile Type-53=No; Pile Type-54=No; Radius=375 mm  [stored 1.23031 ft]; Radius/2=188 mm; band width=125 mm  [stored 0.410105 ft]
- ATK_P8O_750_Diameter: ATK_1.25DIA_Circle_Radius=938 mm; ATK_2.5_DIA_Circle_Radius=1875 mm  [stored 6.15157 ft]; ATK_Pile_DIA=750 mm  [stored 2.46063 ft]; Band Width 2=178 mm; Band Width 3=75 mm; Depth=20000 mm  [stored 65.6168 ft]; Pile Type 01=No; Pile Type 02=No; Pile Type 03=No; Pile Type 04=No; Pile Type 05=No; Pile Type 06=No; Pile Type 07=No; Pile Type 08=Yes; Pile Type 09=No; Pile Type 10=No; Pile Type 11=No; Pile Type 12=No; Pile Type 13=No; Pile Type 14=No; Pile Type 15=No; Pile Type 16=No; Pile Type 17=No; Pile Type 18=No; Pile Type 19=No; Pile Type 20=No; Pile Type 21=No; Pile Type 22=No; Pile Type 23=No; Pile Type 24=No; Pile Type 25=No; Pile Type 26=No; Pile Type 27=No; Pile Type 28=No; Pile Type 29=No; Pile Type 30=No; Pile Type 31=Yes; Pile Type-32=No; Pile Type-33=No; Pile Type-34=No; Pile Type-35=No; Pile Type-36=No; Pile Type-37=Yes; Pile Type-38=No; Pile Type-39=No; Pile Type-40=No; Pile Type-41=No; Pile Type-42=No; Pile Type-43=No; Pile Type-44=No; Pile Type-45=No; Pile Type-46=No; Pile Type-47=No; Pile Type-48=No; Pile Type-49=No; Pile Type-50=No; Pile Type-51=No; Pile Type-52=No; Pile Type-53=No; Pile Type-54=No; Radius=375 mm  [stored 1.23031 ft]; Radius/2=188 mm; band width=125 mm  [stored 0.410105 ft]
- ATK_P16R_1000_Diameter: ATK_1.25DIA_Circle_Radius=1250 mm  [stored 4.10105 ft]; ATK_2.5_DIA_Circle_Radius=2500 mm  [stored 8.2021 ft]; ATK_Pile_DIA=1000 mm  [stored 3.28084 ft]; Band Width 2=240 mm; Band Width 3=100 mm  [stored 0.328084 ft]; Depth=28000 mm  [stored 91.8635 ft]; Pile Type 01=No; Pile Type 02=No; Pile Type 03=No; Pile Type 04=No; Pile Type 05=No; Pile Type 06=No; Pile Type 07=No; Pile Type 08=Yes; Pile Type 09=No; Pile Type 10=No; Pile Type 11=No; Pile Type 12=No; Pile Type 13=No; Pile Type 14=No; Pile Type 15=No; Pile Type 16=Yes; Pile Type 17=No; Pile Type 18=No; Pile Type 19=No; Pile Type 20=No; Pile Type 21=No; Pile Type 22=No; Pile Type 23=No; Pile Type 24=No; Pile Type 25=No; Pile Type 26=No; Pile Type 27=No; Pile Type 28=No; Pile Type 29=No; Pile Type 30=No; Pile Type 31=Yes; Pile Type-32=No; Pile Type-33=No; Pile Type-34=No; Pile Type-35=No; Pile Type-36=No; Pile Type-37=Yes; Pile Type-38=No; Pile Type-39=No; Pile Type-40=No; Pile Type-41=No; Pile Type-42=No; Pile Type-43=No; Pile Type-44=No; Pile Type-45=No; Pile Type-46=No; Pile Type-47=No; Pile Type-48=No; Pile Type-49=No; Pile Type-50=No; Pile Type-51=No; Pile Type-52=No; Pile Type-53=No; Pile Type-54=No; Radius=500 mm  [stored 1.64042 ft]; Radius/2=250 mm  [stored 0.82021 ft]; band width=167 mm
- ATK_P15R_1000_Diameter: ATK_1.25DIA_Circle_Radius=1250 mm  [stored 4.10105 ft]; ATK_2.5_DIA_Circle_Radius=2500 mm  [stored 8.2021 ft]; ATK_Pile_DIA=1000 mm  [stored 3.28084 ft]; Band Width 2=240 mm; Band Width 3=100 mm  [stored 0.328084 ft]; Depth=27000 mm  [stored 88.5827 ft]; Pile Type 01=No; Pile Type 02=No; Pile Type 03=No; Pile Type 04=No; Pile Type 05=No; Pile Type 06=No; Pile Type 07=Yes; Pile Type 08=No; Pile Type 09=No; Pile Type 10=No; Pile Type 11=No; Pile Type 12=No; Pile Type 13=No; Pile Type 14=No; Pile Type 15=Yes; Pile Type 16=No; Pile Type 17=No; Pile Type 18=No; Pile Type 19=No; Pile Type 20=No; Pile Type 21=No; Pile Type 22=No; Pile Type 23=No; Pile Type 24=No; Pile Type 25=No; Pile Type 26=No; Pile Type 27=No; Pile Type 28=No; Pile Type 29=No; Pile Type 30=No; Pile Type 31=Yes; Pile Type-32=No; Pile Type-33=No; Pile Type-34=No; Pile Type-35=No; Pile Type-36=No; Pile Type-37=Yes; Pile Type-38=No; Pile Type-39=No; Pile Type-40=No; Pile Type-41=No; Pile Type-42=No; Pile Type-43=No; Pile Type-44=No; Pile Type-45=No; Pile Type-46=No; Pile Type-47=No; Pile Type-48=No; Pile Type-49=No; Pile Type-50=No; Pile Type-51=No; Pile Type-52=No; Pile Type-53=No; Pile Type-54=No; Radius=500 mm  [stored 1.64042 ft]; Radius/2=250 mm  [stored 0.82021 ft]; band width=167 mm
- ATK_P14R_1000_Diameter: ATK_1.25DIA_Circle_Radius=1250 mm  [stored 4.10105 ft]; ATK_2.5_DIA_Circle_Radius=2500 mm  [stored 8.2021 ft]; ATK_Pile_DIA=1000 mm  [stored 3.28084 ft]; Band Width 2=240 mm; Band Width 3=100 mm  [stored 0.328084 ft]; Depth=26000 mm  [stored 85.3018 ft]; Pile Type 01=No; Pile Type 02=No; Pile Type 03=No; Pile Type 04=No; Pile Type 05=No; Pile Type 06=Yes; Pile Type 07=No; Pile Type 08=No; Pile Type 09=No; Pile Type 10=No; Pile Type 11=No; Pile Type 12=No; Pile Type 13=No; Pile Type 14=Yes; Pile Type 15=No; Pile Type 16=No; Pile Type 17=No; Pile Type 18=No; Pile Type 19=No; Pile Type 20=No; Pile Type 21=No; Pile Type 22=No; Pile Type 23=No; Pile Type 24=No; Pile Type 25=No; Pile Type 26=No; Pile Type 27=No; Pile Type 28=No; Pile Type 29=No; Pile Type 30=No; Pile Type 31=Yes; Pile Type-32=No; Pile Type-33=No; Pile Type-34=No; Pile Type-35=No; Pile Type-36=No; Pile Type-37=Yes; Pile Type-38=No; Pile Type-39=No; Pile Type-40=No; Pile Type-41=No; Pile Type-42=No; Pile Type-43=No; Pile Type-44=No; Pile Type-45=No; Pile Type-46=No; Pile Type-47=No; Pile Type-48=No; Pile Type-49=No; Pile Type-50=No; Pile Type-51=No; Pile Type-52=No; Pile Type-53=No; Pile Type-54=No; Radius=500 mm  [stored 1.64042 ft]; Radius/2=250 mm  [stored 0.82021 ft]; band width=167 mm
- ATK_P13R_1000_Diameter: ATK_1.25DIA_Circle_Radius=1250 mm  [stored 4.10105 ft]; ATK_2.5_DIA_Circle_Radius=2500 mm  [stored 8.2021 ft]; ATK_Pile_DIA=1000 mm  [stored 3.28084 ft]; Band Width 2=240 mm; Band Width 3=100 mm  [stored 0.328084 ft]; Depth=25000 mm  [stored 82.021 ft]; Pile Type 01=No; Pile Type 02=No; Pile Type 03=No; Pile Type 04=No; Pile Type 05=Yes; Pile Type 06=No; Pile Type 07=No; Pile Type 08=No; Pile Type 09=No; Pile Type 10=No; Pile Type 11=No; Pile Type 12=No; Pile Type 13=Yes; Pile Type 14=No; Pile Type 15=No; Pile Type 16=No; Pile Type 17=No; Pile Type 18=No; Pile Type 19=No; Pile Type 20=No; Pile Type 21=No; Pile Type 22=No; Pile Type 23=No; Pile Type 24=No; Pile Type 25=No; Pile Type 26=No; Pile Type 27=No; Pile Type 28=No; Pile Type 29=No; Pile Type 30=No; Pile Type 31=Yes; Pile Type-32=No; Pile Type-33=No; Pile Type-34=No; Pile Type-35=No; Pile Type-36=No; Pile Type-37=Yes; Pile Type-38=No; Pile Type-39=No; Pile Type-40=No; Pile Type-41=No; Pile Type-42=No; Pile Type-43=No; Pile Type-44=No; Pile Type-45=No; Pile Type-46=No; Pile Type-47=No; Pile Type-48=No; Pile Type-49=No; Pile Type-50=No; Pile Type-51=No; Pile Type-52=No; Pile Type-53=No; Pile Type-54=No; Radius=500 mm  [stored 1.64042 ft]; Radius/2=250 mm  [stored 0.82021 ft]; band width=167 mm
- ATK_P12R_1000_Diameter: ATK_1.25DIA_Circle_Radius=1250 mm  [stored 4.10105 ft]; ATK_2.5_DIA_Circle_Radius=2500 mm  [stored 8.2021 ft]; ATK_Pile_DIA=1000 mm  [stored 3.28084 ft]; Band Width 2=240 mm; Band Width 3=100 mm  [stored 0.328084 ft]; Depth=24000 mm  [stored 78.7402 ft]; Pile Type 01=No; Pile Type 02=No; Pile Type 03=No; Pile Type 04=Yes; Pile Type 05=No; Pile Type 06=No; Pile Type 07=No; Pile Type 08=No; Pile Type 09=No; Pile Type 10=No; Pile Type 11=No; Pile Type 12=Yes; Pile Type 13=No; Pile Type 14=No; Pile Type 15=No; Pile Type 16=No; Pile Type 17=No; Pile Type 18=No; Pile Type 19=No; Pile Type 20=No; Pile Type 21=No; Pile Type 22=No; Pile Type 23=No; Pile Type 24=No; Pile Type 25=No; Pile Type 26=No; Pile Type 27=No; Pile Type 28=No; Pile Type 29=No; Pile Type 30=No; Pile Type 31=Yes; Pile Type-32=No; Pile Type-33=No; Pile Type-34=No; Pile Type-35=No; Pile Type-36=No; Pile Type-37=Yes; Pile Type-38=No; Pile Type-39=No; Pile Type-40=No; Pile Type-41=No; Pile Type-42=No; Pile Type-43=No; Pile Type-44=No; Pile Type-45=No; Pile Type-46=No; Pile Type-47=No; Pile Type-48=No; Pile Type-49=No; Pile Type-50=No; Pile Type-51=No; Pile Type-52=No; Pile Type-53=No; Pile Type-54=No; Radius=500 mm  [stored 1.64042 ft]; Radius/2=250 mm  [stored 0.82021 ft]; band width=167 mm
- ATK_P11R_1000_Diameter: ATK_1.25DIA_Circle_Radius=1250 mm  [stored 4.10105 ft]; ATK_2.5_DIA_Circle_Radius=2500 mm  [stored 8.2021 ft]; ATK_Pile_DIA=1000 mm  [stored 3.28084 ft]; Band Width 2=240 mm; Band Width 3=100 mm  [stored 0.328084 ft]; Depth=23000 mm  [stored 75.4593 ft]; Pile Type 01=No; Pile Type 02=No; Pile Type 03=Yes; Pile Type 04=No; Pile Type 05=No; Pile Type 06=No; Pile Type 07=No; Pile Type 08=No; Pile Type 09=No; Pile Type 10=No; Pile Type 11=Yes; Pile Type 12=No; Pile Type 13=No; Pile Type 14=No; Pile Type 15=No; Pile Type 16=No; Pile Type 17=No; Pile Type 18=No; Pile Type 19=No; Pile Type 20=No; Pile Type 21=No; Pile Type 22=No; Pile Type 23=No; Pile Type 24=No; Pile Type 25=No; Pile Type 26=No; Pile Type 27=No; Pile Type 28=No; Pile Type 29=No; Pile Type 30=No; Pile Type 31=Yes; Pile Type-32=No; Pile Type-33=No; Pile Type-34=No; Pile Type-35=No; Pile Type-36=No; Pile Type-37=Yes; Pile Type-38=No; Pile Type-39=No; Pile Type-40=No; Pile Type-41=No; Pile Type-42=No; Pile Type-43=No; Pile Type-44=No; Pile Type-45=No; Pile Type-46=No; Pile Type-47=No; Pile Type-48=No; Pile Type-49=No; Pile Type-50=No; Pile Type-51=No; Pile Type-52=No; Pile Type-53=No; Pile Type-54=No; Radius=500 mm  [stored 1.64042 ft]; Radius/2=250 mm  [stored 0.82021 ft]; band width=167 mm
- ATK_P9R_1000_Diameter: ATK_1.25DIA_Circle_Radius=1250 mm  [stored 4.10105 ft]; ATK_2.5_DIA_Circle_Radius=2500 mm  [stored 8.2021 ft]; ATK_Pile_DIA=1000 mm  [stored 3.28084 ft]; Band Width 2=240 mm; Band Width 3=100 mm  [stored 0.328084 ft]; Depth=21000 mm  [stored 68.8976 ft]; Pile Type 01=No; Pile Type 02=No; Pile Type 03=No; Pile Type 04=No; Pile Type 05=No; Pile Type 06=No; Pile Type 07=No; Pile Type 08=No; Pile Type 09=Yes; Pile Type 10=No; Pile Type 11=No; Pile Type 12=No; Pile Type 13=No; Pile Type 14=No; Pile Type 15=No; Pile Type 16=No; Pile Type 17=No; Pile Type 18=No; Pile Type 19=Yes; Pile Type 20=No; Pile Type 21=No; Pile Type 22=No; Pile Type 23=No; Pile Type 24=No; Pile Type 25=No; Pile Type 26=No; Pile Type 27=No; Pile Type 28=No; Pile Type 29=No; Pile Type 30=No; Pile Type 31=Yes; Pile Type-32=No; Pile Type-33=No; Pile Type-34=No; Pile Type-35=No; Pile Type-36=No; Pile Type-37=Yes; Pile Type-38=No; Pile Type-39=No; Pile Type-40=No; Pile Type-41=No; Pile Type-42=No; Pile Type-43=No; Pile Type-44=No; Pile Type-45=No; Pile Type-46=No; Pile Type-47=No; Pile Type-48=No; Pile Type-49=No; Pile Type-50=No; Pile Type-51=No; Pile Type-52=No; Pile Type-53=No; Pile Type-54=No; Radius=500 mm  [stored 1.64042 ft]; Radius/2=250 mm  [stored 0.82021 ft]; band width=167 mm
- ATK_P8R_1000_Diameter: ATK_1.25DIA_Circle_Radius=1250 mm  [stored 4.10105 ft]; ATK_2.5_DIA_Circle_Radius=2500 mm  [stored 8.2021 ft]; ATK_Pile_DIA=1000 mm  [stored 3.28084 ft]; Band Width 2=240 mm; Band Width 3=100 mm  [stored 0.328084 ft]; Depth=20000 mm  [stored 65.6168 ft]; Pile Type 01=No; Pile Type 02=No; Pile Type 03=No; Pile Type 04=No; Pile Type 05=No; Pile Type 06=No; Pile Type 07=No; Pile Type 08=Yes; Pile Type 09=No; Pile Type 10=No; Pile Type 11=No; Pile Type 12=No; Pile Type 13=No; Pile Type 14=No; Pile Type 15=No; Pile Type 16=No; Pile Type 17=No; Pile Type 18=Yes; Pile Type 19=No; Pile Type 20=No; Pile Type 21=No; Pile Type 22=No; Pile Type 23=No; Pile Type 24=No; Pile Type 25=No; Pile Type 26=No; Pile Type 27=No; Pile Type 28=No; Pile Type 29=No; Pile Type 30=No; Pile Type 31=Yes; Pile Type-32=No; Pile Type-33=No; Pile Type-34=No; Pile Type-35=No; Pile Type-36=No; Pile Type-37=Yes; Pile Type-38=No; Pile Type-39=No; Pile Type-40=No; Pile Type-41=No; Pile Type-42=No; Pile Type-43=No; Pile Type-44=No; Pile Type-45=No; Pile Type-46=No; Pile Type-47=No; Pile Type-48=No; Pile Type-49=No; Pile Type-50=No; Pile Type-51=No; Pile Type-52=No; Pile Type-53=No; Pile Type-54=No; Radius=500 mm  [stored 1.64042 ft]; Radius/2=250 mm  [stored 0.82021 ft]; band width=167 mm
- ATK_P7R_1000_Diameter: ATK_1.25DIA_Circle_Radius=1250 mm  [stored 4.10105 ft]; ATK_2.5_DIA_Circle_Radius=2500 mm  [stored 8.2021 ft]; ATK_Pile_DIA=1000 mm  [stored 3.28084 ft]; Band Width 2=240 mm; Band Width 3=100 mm  [stored 0.328084 ft]; Depth=19000 mm; Pile Type 01=No; Pile Type 02=No; Pile Type 03=No; Pile Type 04=No; Pile Type 05=No; Pile Type 06=No; Pile Type 07=Yes; Pile Type 08=No; Pile Type 09=No; Pile Type 10=No; Pile Type 11=No; Pile Type 12=No; Pile Type 13=No; Pile Type 14=No; Pile Type 15=No; Pile Type 16=No; Pile Type 17=Yes; Pile Type 18=No; Pile Type 19=No; Pile Type 20=No; Pile Type 21=No; Pile Type 22=No; Pile Type 23=No; Pile Type 24=No; Pile Type 25=No; Pile Type 26=No; Pile Type 27=No; Pile Type 28=No; Pile Type 29=No; Pile Type 30=No; Pile Type 31=Yes; Pile Type-32=No; Pile Type-33=No; Pile Type-34=No; Pile Type-35=No; Pile Type-36=No; Pile Type-37=Yes; Pile Type-38=No; Pile Type-39=No; Pile Type-40=No; Pile Type-41=No; Pile Type-42=No; Pile Type-43=No; Pile Type-44=No; Pile Type-45=No; Pile Type-46=No; Pile Type-47=No; Pile Type-48=No; Pile Type-49=No; Pile Type-50=No; Pile Type-51=No; Pile Type-52=No; Pile Type-53=No; Pile Type-54=No; Radius=500 mm  [stored 1.64042 ft]; Radius/2=250 mm  [stored 0.82021 ft]; band width=167 mm
- ATK_P6R_1000_Diameter: ATK_1.25DIA_Circle_Radius=1250 mm  [stored 4.10105 ft]; ATK_2.5_DIA_Circle_Radius=2500 mm  [stored 8.2021 ft]; ATK_Pile_DIA=1000 mm  [stored 3.28084 ft]; Band Width 2=240 mm; Band Width 3=100 mm  [stored 0.328084 ft]; Depth=18000 mm; Pile Type 01=No; Pile Type 02=No; Pile Type 03=No; Pile Type 04=No; Pile Type 05=No; Pile Type 06=Yes; Pile Type 07=No; Pile Type 08=No; Pile Type 09=No; Pile Type 10=No; Pile Type 11=No; Pile Type 12=No; Pile Type 13=No; Pile Type 14=No; Pile Type 15=No; Pile Type 16=Yes; Pile Type 17=No; Pile Type 18=No; Pile Type 19=No; Pile Type 20=No; Pile Type 21=No; Pile Type 22=No; Pile Type 23=No; Pile Type 24=No; Pile Type 25=No; Pile Type 26=No; Pile Type 27=No; Pile Type 28=No; Pile Type 29=No; Pile Type 30=No; Pile Type 31=Yes; Pile Type-32=No; Pile Type-33=No; Pile Type-34=No; Pile Type-35=No; Pile Type-36=No; Pile Type-37=Yes; Pile Type-38=No; Pile Type-39=No; Pile Type-40=No; Pile Type-41=No; Pile Type-42=No; Pile Type-43=No; Pile Type-44=No; Pile Type-45=No; Pile Type-46=No; Pile Type-47=No; Pile Type-48=No; Pile Type-49=No; Pile Type-50=No; Pile Type-51=No; Pile Type-52=No; Pile Type-53=No; Pile Type-54=No; Radius=500 mm  [stored 1.64042 ft]; Radius/2=250 mm  [stored 0.82021 ft]; band width=167 mm
- ATK_P5R_1000_Diameter: ATK_1.25DIA_Circle_Radius=1250 mm  [stored 4.10105 ft]; ATK_2.5_DIA_Circle_Radius=2500 mm  [stored 8.2021 ft]; ATK_Pile_DIA=1000 mm  [stored 3.28084 ft]; Band Width 2=240 mm; Band Width 3=100 mm  [stored 0.328084 ft]; Depth=17000 mm; Pile Type 01=No; Pile Type 02=No; Pile Type 03=No; Pile Type 04=No; Pile Type 05=Yes; Pile Type 06=No; Pile Type 07=No; Pile Type 08=No; Pile Type 09=No; Pile Type 10=No; Pile Type 11=No; Pile Type 12=No; Pile Type 13=No; Pile Type 14=No; Pile Type 15=Yes; Pile Type 16=No; Pile Type 17=No; Pile Type 18=No; Pile Type 19=No; Pile Type 20=No; Pile Type 21=No; Pile Type 22=No; Pile Type 23=No; Pile Type 24=No; Pile Type 25=No; Pile Type 26=No; Pile Type 27=No; Pile Type 28=No; Pile Type 29=No; Pile Type 30=No; Pile Type 31=Yes; Pile Type-32=No; Pile Type-33=No; Pile Type-34=No; Pile Type-35=No; Pile Type-36=No; Pile Type-37=Yes; Pile Type-38=No; Pile Type-39=No; Pile Type-40=No; Pile Type-41=No; Pile Type-42=No; Pile Type-43=No; Pile Type-44=No; Pile Type-45=No; Pile Type-46=No; Pile Type-47=No; Pile Type-48=No; Pile Type-49=No; Pile Type-50=No; Pile Type-51=No; Pile Type-52=No; Pile Type-53=No; Pile Type-54=No; Radius=500 mm  [stored 1.64042 ft]; Radius/2=250 mm  [stored 0.82021 ft]; band width=167 mm
- ATK_P4R_1000_Diameter: ATK_1.25DIA_Circle_Radius=1250 mm  [stored 4.10105 ft]; ATK_2.5_DIA_Circle_Radius=2500 mm  [stored 8.2021 ft]; ATK_Pile_DIA=1000 mm  [stored 3.28084 ft]; Band Width 2=240 mm; Band Width 3=100 mm  [stored 0.328084 ft]; Depth=16000 mm  [stored 52.4934 ft]; Pile Type 01=No; Pile Type 02=No; Pile Type 03=No; Pile Type 04=Yes; Pile Type 05=No; Pile Type 06=No; Pile Type 07=No; Pile Type 08=No; Pile Type 09=No; Pile Type 10=No; Pile Type 11=No; Pile Type 12=No; Pile Type 13=No; Pile Type 14=Yes; Pile Type 15=No; Pile Type 16=No; Pile Type 17=No; Pile Type 18=No; Pile Type 19=No; Pile Type 20=No; Pile Type 21=No; Pile Type 22=No; Pile Type 23=No; Pile Type 24=No; Pile Type 25=No; Pile Type 26=No; Pile Type 27=No; Pile Type 28=No; Pile Type 29=No; Pile Type 30=No; Pile Type 31=Yes; Pile Type-32=No; Pile Type-33=No; Pile Type-34=No; Pile Type-35=No; Pile Type-36=No; Pile Type-37=Yes; Pile Type-38=No; Pile Type-39=No; Pile Type-40=No; Pile Type-41=No; Pile Type-42=No; Pile Type-43=No; Pile Type-44=No; Pile Type-45=No; Pile Type-46=No; Pile Type-47=No; Pile Type-48=No; Pile Type-49=No; Pile Type-50=No; Pile Type-51=No; Pile Type-52=No; Pile Type-53=No; Pile Type-54=No; Radius=500 mm  [stored 1.64042 ft]; Radius/2=250 mm  [stored 0.82021 ft]; band width=167 mm
- ATK_P3R_1000_Diameter: ATK_1.25DIA_Circle_Radius=1250 mm  [stored 4.10105 ft]; ATK_2.5_DIA_Circle_Radius=2500 mm  [stored 8.2021 ft]; ATK_Pile_DIA=1000 mm  [stored 3.28084 ft]; Band Width 2=240 mm; Band Width 3=100 mm  [stored 0.328084 ft]; Depth=15000 mm  [stored 49.2126 ft]; Pile Type 01=No; Pile Type 02=No; Pile Type 03=Yes; Pile Type 04=No; Pile Type 05=No; Pile Type 06=No; Pile Type 07=No; Pile Type 08=No; Pile Type 09=No; Pile Type 10=No; Pile Type 11=No; Pile Type 12=No; Pile Type 13=Yes; Pile Type 14=No; Pile Type 15=No; Pile Type 16=No; Pile Type 17=No; Pile Type 18=No; Pile Type 19=No; Pile Type 20=No; Pile Type 21=No; Pile Type 22=No; Pile Type 23=No; Pile Type 24=No; Pile Type 25=No; Pile Type 26=No; Pile Type 27=No; Pile Type 28=No; Pile Type 29=No; Pile Type 30=No; Pile Type 31=Yes; Pile Type-32=No; Pile Type-33=No; Pile Type-34=No; Pile Type-35=No; Pile Type-36=No; Pile Type-37=Yes; Pile Type-38=No; Pile Type-39=No; Pile Type-40=No; Pile Type-41=No; Pile Type-42=No; Pile Type-43=No; Pile Type-44=No; Pile Type-45=No; Pile Type-46=No; Pile Type-47=No; Pile Type-48=No; Pile Type-49=No; Pile Type-50=No; Pile Type-51=No; Pile Type-52=No; Pile Type-53=No; Pile Type-54=No; Radius=500 mm  [stored 1.64042 ft]; Radius/2=250 mm  [stored 0.82021 ft]; band width=167 mm
- ATK_P2R_1000_Diameter: ATK_1.25DIA_Circle_Radius=1250 mm  [stored 4.10105 ft]; ATK_2.5_DIA_Circle_Radius=2500 mm  [stored 8.2021 ft]; ATK_Pile_DIA=1000 mm  [stored 3.28084 ft]; Band Width 2=240 mm; Band Width 3=100 mm  [stored 0.328084 ft]; Depth=14000 mm  [stored 45.9318 ft]; Pile Type 01=No; Pile Type 02=Yes; Pile Type 03=No; Pile Type 04=No; Pile Type 05=No; Pile Type 06=No; Pile Type 07=No; Pile Type 08=No; Pile Type 09=No; Pile Type 10=No; Pile Type 11=No; Pile Type 12=Yes; Pile Type 13=No; Pile Type 14=No; Pile Type 15=No; Pile Type 16=No; Pile Type 17=No; Pile Type 18=No; Pile Type 19=No; Pile Type 20=No; Pile Type 21=No; Pile Type 22=No; Pile Type 23=No; Pile Type 24=No; Pile Type 25=No; Pile Type 26=No; Pile Type 27=No; Pile Type 28=No; Pile Type 29=No; Pile Type 30=No; Pile Type 31=Yes; Pile Type-32=No; Pile Type-33=No; Pile Type-34=No; Pile Type-35=No; Pile Type-36=No; Pile Type-37=Yes; Pile Type-38=No; Pile Type-39=No; Pile Type-40=No; Pile Type-41=No; Pile Type-42=No; Pile Type-43=No; Pile Type-44=No; Pile Type-45=No; Pile Type-46=No; Pile Type-47=No; Pile Type-48=No; Pile Type-49=No; Pile Type-50=No; Pile Type-51=No; Pile Type-52=No; Pile Type-53=No; Pile Type-54=No; Radius=500 mm  [stored 1.64042 ft]; Radius/2=250 mm  [stored 0.82021 ft]; band width=167 mm
- ATK_P1R_1000_Diameter: ATK_1.25DIA_Circle_Radius=1250 mm  [stored 4.10105 ft]; ATK_2.5_DIA_Circle_Radius=2500 mm  [stored 8.2021 ft]; ATK_Pile_DIA=1000 mm  [stored 3.28084 ft]; Band Width 2=240 mm; Band Width 3=100 mm  [stored 0.328084 ft]; Depth=13000 mm  [stored 42.6509 ft]; Pile Type 01=Yes; Pile Type 02=No; Pile Type 03=No; Pile Type 04=No; Pile Type 05=No; Pile Type 06=No; Pile Type 07=No; Pile Type 08=No; Pile Type 09=No; Pile Type 10=No; Pile Type 11=Yes; Pile Type 12=No; Pile Type 13=No; Pile Type 14=No; Pile Type 15=No; Pile Type 16=No; Pile Type 17=No; Pile Type 18=No; Pile Type 19=No; Pile Type 20=No; Pile Type 21=No; Pile Type 22=No; Pile Type 23=No; Pile Type 24=No; Pile Type 25=No; Pile Type 26=No; Pile Type 27=No; Pile Type 28=No; Pile Type 29=No; Pile Type 30=No; Pile Type 31=Yes; Pile Type-32=No; Pile Type-33=No; Pile Type-34=No; Pile Type-35=No; Pile Type-36=No; Pile Type-37=Yes; Pile Type-38=No; Pile Type-39=No; Pile Type-40=No; Pile Type-41=No; Pile Type-42=No; Pile Type-43=No; Pile Type-44=No; Pile Type-45=No; Pile Type-46=No; Pile Type-47=No; Pile Type-48=No; Pile Type-49=No; Pile Type-50=No; Pile Type-51=No; Pile Type-52=No; Pile Type-53=No; Pile Type-54=No; Radius=500 mm  [stored 1.64042 ft]; Radius/2=250 mm  [stored 0.82021 ft]; band width=167 mm
- ATK_P7O_750_Diameter: ATK_1.25DIA_Circle_Radius=938 mm; ATK_2.5_DIA_Circle_Radius=1875 mm  [stored 6.15157 ft]; ATK_Pile_DIA=750 mm  [stored 2.46063 ft]; Band Width 2=178 mm; Band Width 3=75 mm; Depth=19000 mm; Pile Type 01=No; Pile Type 02=No; Pile Type 03=No; Pile Type 04=No; Pile Type 05=No; Pile Type 06=No; Pile Type 07=Yes; Pile Type 08=No; Pile Type 09=No; Pile Type 10=No; Pile Type 11=No; Pile Type 12=No; Pile Type 13=No; Pile Type 14=No; Pile Type 15=No; Pile Type 16=No; Pile Type 17=No; Pile Type 18=No; Pile Type 19=No; Pile Type 20=No; Pile Type 21=No; Pile Type 22=No; Pile Type 23=No; Pile Type 24=No; Pile Type 25=No; Pile Type 26=No; Pile Type 27=No; Pile Type 28=No; Pile Type 29=No; Pile Type 30=No; Pile Type 31=Yes; Pile Type-32=No; Pile Type-33=No; Pile Type-34=No; Pile Type-35=No; Pile Type-36=No; Pile Type-37=Yes; Pile Type-38=No; Pile Type-39=No; Pile Type-40=No; Pile Type-41=No; Pile Type-42=No; Pile Type-43=No; Pile Type-44=No; Pile Type-45=No; Pile Type-46=No; Pile Type-47=No; Pile Type-48=No; Pile Type-49=No; Pile Type-50=No; Pile Type-51=No; Pile Type-52=No; Pile Type-53=No; Pile Type-54=No; Radius=375 mm  [stored 1.23031 ft]; Radius/2=188 mm; band width=125 mm  [stored 0.410105 ft]
- ATK_P6O_750_Diameter: ATK_1.25DIA_Circle_Radius=938 mm; ATK_2.5_DIA_Circle_Radius=1875 mm  [stored 6.15157 ft]; ATK_Pile_DIA=750 mm  [stored 2.46063 ft]; Band Width 2=178 mm; Band Width 3=75 mm; Depth=18000 mm; Pile Type 01=No; Pile Type 02=No; Pile Type 03=No; Pile Type 04=No; Pile Type 05=No; Pile Type 06=Yes; Pile Type 07=No; Pile Type 08=No; Pile Type 09=No; Pile Type 10=No; Pile Type 11=No; Pile Type 12=No; Pile Type 13=No; Pile Type 14=No; Pile Type 15=No; Pile Type 16=No; Pile Type 17=No; Pile Type 18=No; Pile Type 19=No; Pile Type 20=No; Pile Type 21=No; Pile Type 22=No; Pile Type 23=No; Pile Type 24=No; Pile Type 25=No; Pile Type 26=No; Pile Type 27=No; Pile Type 28=No; Pile Type 29=No; Pile Type 30=No; Pile Type 31=Yes; Pile Type-32=No; Pile Type-33=No; Pile Type-34=No; Pile Type-35=No; Pile Type-36=No; Pile Type-37=Yes; Pile Type-38=No; Pile Type-39=No; Pile Type-40=No; Pile Type-41=No; Pile Type-42=No; Pile Type-43=No; Pile Type-44=No; Pile Type-45=No; Pile Type-46=No; Pile Type-47=No; Pile Type-48=No; Pile Type-49=No; Pile Type-50=No; Pile Type-51=No; Pile Type-52=No; Pile Type-53=No; Pile Type-54=No; Radius=375 mm  [stored 1.23031 ft]; Radius/2=188 mm; band width=125 mm  [stored 0.410105 ft]
- ATK_P5O_750_Diameter: ATK_1.25DIA_Circle_Radius=938 mm; ATK_2.5_DIA_Circle_Radius=1875 mm  [stored 6.15157 ft]; ATK_Pile_DIA=750 mm  [stored 2.46063 ft]; Band Width 2=178 mm; Band Width 3=75 mm; Depth=17000 mm; Pile Type 01=No; Pile Type 02=No; Pile Type 03=No; Pile Type 04=No; Pile Type 05=Yes; Pile Type 06=No; Pile Type 07=No; Pile Type 08=No; Pile Type 09=No; Pile Type 10=No; Pile Type 11=No; Pile Type 12=No; Pile Type 13=No; Pile Type 14=No; Pile Type 15=No; Pile Type 16=No; Pile Type 17=No; Pile Type 18=No; Pile Type 19=No; Pile Type 20=No; Pile Type 21=No; Pile Type 22=No; Pile Type 23=No; Pile Type 24=No; Pile Type 25=No; Pile Type 26=No; Pile Type 27=No; Pile Type 28=No; Pile Type 29=No; Pile Type 30=No; Pile Type 31=Yes; Pile Type-32=No; Pile Type-33=No; Pile Type-34=No; Pile Type-35=No; Pile Type-36=No; Pile Type-37=Yes; Pile Type-38=No; Pile Type-39=No; Pile Type-40=No; Pile Type-41=No; Pile Type-42=No; Pile Type-43=No; Pile Type-44=No; Pile Type-45=No; Pile Type-46=No; Pile Type-47=No; Pile Type-48=No; Pile Type-49=No; Pile Type-50=No; Pile Type-51=No; Pile Type-52=No; Pile Type-53=No; Pile Type-54=No; Radius=375 mm  [stored 1.23031 ft]; Radius/2=188 mm; band width=125 mm  [stored 0.410105 ft]
- ATK_P4O_750_Diameter: ATK_1.25DIA_Circle_Radius=938 mm; ATK_2.5_DIA_Circle_Radius=1875 mm  [stored 6.15157 ft]; ATK_Pile_DIA=750 mm  [stored 2.46063 ft]; Band Width 2=178 mm; Band Width 3=75 mm; Depth=16000 mm  [stored 52.4934 ft]; Pile Type 01=No; Pile Type 02=No; Pile Type 03=No; Pile Type 04=Yes; Pile Type 05=No; Pile Type 06=No; Pile Type 07=No; Pile Type 08=No; Pile Type 09=No; Pile Type 10=No; Pile Type 11=No; Pile Type 12=No; Pile Type 13=No; Pile Type 14=No; Pile Type 15=No; Pile Type 16=No; Pile Type 17=No; Pile Type 18=No; Pile Type 19=No; Pile Type 20=No; Pile Type 21=No; Pile Type 22=No; Pile Type 23=No; Pile Type 24=No; Pile Type 25=No; Pile Type 26=No; Pile Type 27=No; Pile Type 28=No; Pile Type 29=No; Pile Type 30=No; Pile Type 31=Yes; Pile Type-32=No; Pile Type-33=No; Pile Type-34=No; Pile Type-35=No; Pile Type-36=No; Pile Type-37=Yes; Pile Type-38=No; Pile Type-39=No; Pile Type-40=No; Pile Type-41=No; Pile Type-42=No; Pile Type-43=No; Pile Type-44=No; Pile Type-45=No; Pile Type-46=No; Pile Type-47=No; Pile Type-48=No; Pile Type-49=No; Pile Type-50=No; Pile Type-51=No; Pile Type-52=No; Pile Type-53=No; Pile Type-54=No; Radius=375 mm  [stored 1.23031 ft]; Radius/2=188 mm; band width=125 mm  [stored 0.410105 ft]
- ATK_P3O_750_Diameter: ATK_1.25DIA_Circle_Radius=938 mm; ATK_2.5_DIA_Circle_Radius=1875 mm  [stored 6.15157 ft]; ATK_Pile_DIA=750 mm  [stored 2.46063 ft]; Band Width 2=178 mm; Band Width 3=75 mm; Depth=15000 mm  [stored 49.2126 ft]; Pile Type 01=No; Pile Type 02=No; Pile Type 03=Yes; Pile Type 04=No; Pile Type 05=No; Pile Type 06=No; Pile Type 07=No; Pile Type 08=No; Pile Type 09=No; Pile Type 10=No; Pile Type 11=No; Pile Type 12=No; Pile Type 13=No; Pile Type 14=No; Pile Type 15=No; Pile Type 16=No; Pile Type 17=No; Pile Type 18=No; Pile Type 19=No; Pile Type 20=No; Pile Type 21=No; Pile Type 22=No; Pile Type 23=No; Pile Type 24=No; Pile Type 25=No; Pile Type 26=No; Pile Type 27=No; Pile Type 28=No; Pile Type 29=No; Pile Type 30=No; Pile Type 31=Yes; Pile Type-32=No; Pile Type-33=No; Pile Type-34=No; Pile Type-35=No; Pile Type-36=No; Pile Type-37=Yes; Pile Type-38=No; Pile Type-39=No; Pile Type-40=No; Pile Type-41=No; Pile Type-42=No; Pile Type-43=No; Pile Type-44=No; Pile Type-45=No; Pile Type-46=No; Pile Type-47=No; Pile Type-48=No; Pile Type-49=No; Pile Type-50=No; Pile Type-51=No; Pile Type-52=No; Pile Type-53=No; Pile Type-54=No; Radius=375 mm  [stored 1.23031 ft]; Radius/2=188 mm; band width=125 mm  [stored 0.410105 ft]
- ATK_P1O_750_Diameter: ATK_1.25DIA_Circle_Radius=938 mm; ATK_2.5_DIA_Circle_Radius=1875 mm  [stored 6.15157 ft]; ATK_Pile_DIA=750 mm  [stored 2.46063 ft]; Band Width 2=178 mm; Band Width 3=75 mm; Depth=13000 mm  [stored 42.6509 ft]; Pile Type 01=Yes; Pile Type 02=No; Pile Type 03=No; Pile Type 04=No; Pile Type 05=No; Pile Type 06=No; Pile Type 07=No; Pile Type 08=No; Pile Type 09=No; Pile Type 10=No; Pile Type 11=No; Pile Type 12=No; Pile Type 13=No; Pile Type 14=No; Pile Type 15=No; Pile Type 16=No; Pile Type 17=No; Pile Type 18=No; Pile Type 19=No; Pile Type 20=No; Pile Type 21=No; Pile Type 22=No; Pile Type 23=No; Pile Type 24=No; Pile Type 25=No; Pile Type 26=No; Pile Type 27=No; Pile Type 28=No; Pile Type 29=No; Pile Type 30=No; Pile Type 31=Yes; Pile Type-32=No; Pile Type-33=No; Pile Type-34=No; Pile Type-35=No; Pile Type-36=No; Pile Type-37=Yes; Pile Type-38=No; Pile Type-39=No; Pile Type-40=No; Pile Type-41=No; Pile Type-42=No; Pile Type-43=No; Pile Type-44=No; Pile Type-45=No; Pile Type-46=No; Pile Type-47=No; Pile Type-48=No; Pile Type-49=No; Pile Type-50=No; Pile Type-51=No; Pile Type-52=No; Pile Type-53=No; Pile Type-54=No; Radius=375 mm  [stored 1.23031 ft]; Radius/2=188 mm; band width=125 mm  [stored 0.410105 ft]
- ATK_P3U_900_Diameter: ATK_1.25DIA_Circle_Radius=1125 mm; ATK_2.5_DIA_Circle_Radius=2250 mm; ATK_Pile_DIA=900 mm  [stored 2.95276 ft]; Band Width 2=215 mm; Band Width 3=90 mm; Depth=15000 mm  [stored 49.2126 ft]; Pile Type 01=No; Pile Type 02=No; Pile Type 03=Yes; Pile Type 04=Yes; Pile Type 05=No; Pile Type 06=No; Pile Type 07=No; Pile Type 08=No; Pile Type 09=No; Pile Type 10=No; Pile Type 11=No; Pile Type 12=No; Pile Type 13=No; Pile Type 14=No; Pile Type 15=No; Pile Type 16=No; Pile Type 17=No; Pile Type 18=No; Pile Type 19=No; Pile Type 20=No; Pile Type 21=No; Pile Type 22=No; Pile Type 23=No; Pile Type 24=No; Pile Type 25=No; Pile Type 26=No; Pile Type 27=No; Pile Type 28=No; Pile Type 29=No; Pile Type 30=No; Pile Type 31=Yes; Pile Type-32=No; Pile Type-33=No; Pile Type-34=No; Pile Type-35=No; Pile Type-36=No; Pile Type-37=Yes; Pile Type-38=No; Pile Type-39=No; Pile Type-40=No; Pile Type-41=No; Pile Type-42=No; Pile Type-43=No; Pile Type-44=No; Pile Type-45=No; Pile Type-46=No; Pile Type-47=No; Pile Type-48=No; Pile Type-49=No; Pile Type-50=No; Pile Type-51=No; Pile Type-52=No; Pile Type-53=No; Pile Type-54=No; Radius=450 mm  [stored 1.47638 ft]; Radius/2=225 mm  [stored 0.738189 ft]; band width=150 mm
- ATK_P18U_900_Diameter: ATK_1.25DIA_Circle_Radius=1125 mm; ATK_2.5_DIA_Circle_Radius=2250 mm; ATK_Pile_DIA=900 mm  [stored 2.95276 ft]; Band Width 2=215 mm; Band Width 3=90 mm; Depth=30000 mm; Pile Type 01=No; Pile Type 02=No; Pile Type 03=No; Pile Type 04=No; Pile Type 05=No; Pile Type 06=No; Pile Type 07=No; Pile Type 08=No; Pile Type 09=No; Pile Type 10=No; Pile Type 11=No; Pile Type 12=No; Pile Type 13=No; Pile Type 14=No; Pile Type 15=No; Pile Type 16=No; Pile Type 17=No; Pile Type 18=Yes; Pile Type 19=Yes; Pile Type 20=No; Pile Type 21=No; Pile Type 22=No; Pile Type 23=No; Pile Type 24=No; Pile Type 25=No; Pile Type 26=No; Pile Type 27=No; Pile Type 28=No; Pile Type 29=No; Pile Type 30=No; Pile Type 31=Yes; Pile Type-32=No; Pile Type-33=No; Pile Type-34=No; Pile Type-35=No; Pile Type-36=No; Pile Type-37=Yes; Pile Type-38=No; Pile Type-39=No; Pile Type-40=No; Pile Type-41=No; Pile Type-42=No; Pile Type-43=No; Pile Type-44=No; Pile Type-45=No; Pile Type-46=No; Pile Type-47=No; Pile Type-48=No; Pile Type-49=No; Pile Type-50=No; Pile Type-51=No; Pile Type-52=No; Pile Type-53=No; Pile Type-54=No; Radius=450 mm  [stored 1.47638 ft]; Radius/2=225 mm  [stored 0.738189 ft]; band width=150 mm
- ATK_P17U_900_Diameter: ATK_1.25DIA_Circle_Radius=1125 mm; ATK_2.5_DIA_Circle_Radius=2250 mm; ATK_Pile_DIA=900 mm  [stored 2.95276 ft]; Band Width 2=215 mm; Band Width 3=90 mm; Depth=29000 mm; Pile Type 01=No; Pile Type 02=No; Pile Type 03=No; Pile Type 04=No; Pile Type 05=No; Pile Type 06=No; Pile Type 07=No; Pile Type 08=No; Pile Type 09=No; Pile Type 10=No; Pile Type 11=No; Pile Type 12=No; Pile Type 13=No; Pile Type 14=No; Pile Type 15=No; Pile Type 16=No; Pile Type 17=Yes; Pile Type 18=Yes; Pile Type 19=No; Pile Type 20=No; Pile Type 21=No; Pile Type 22=No; Pile Type 23=No; Pile Type 24=No; Pile Type 25=No; Pile Type 26=No; Pile Type 27=No; Pile Type 28=No; Pile Type 29=No; Pile Type 30=No; Pile Type 31=Yes; Pile Type-32=No; Pile Type-33=No; Pile Type-34=No; Pile Type-35=No; Pile Type-36=No; Pile Type-37=Yes; Pile Type-38=No; Pile Type-39=No; Pile Type-40=No; Pile Type-41=No; Pile Type-42=No; Pile Type-43=No; Pile Type-44=No; Pile Type-45=No; Pile Type-46=No; Pile Type-47=No; Pile Type-48=No; Pile Type-49=No; Pile Type-50=No; Pile Type-51=No; Pile Type-52=No; Pile Type-53=No; Pile Type-54=No; Radius=450 mm  [stored 1.47638 ft]; Radius/2=225 mm  [stored 0.738189 ft]; band width=150 mm
- ATK_P16U_900_Diameter: ATK_1.25DIA_Circle_Radius=1125 mm; ATK_2.5_DIA_Circle_Radius=2250 mm; ATK_Pile_DIA=900 mm  [stored 2.95276 ft]; Band Width 2=215 mm; Band Width 3=90 mm; Depth=28000 mm  [stored 91.8635 ft]; Pile Type 01=No; Pile Type 02=No; Pile Type 03=No; Pile Type 04=No; Pile Type 05=No; Pile Type 06=No; Pile Type 07=No; Pile Type 08=No; Pile Type 09=No; Pile Type 10=No; Pile Type 11=No; Pile Type 12=No; Pile Type 13=No; Pile Type 14=No; Pile Type 15=No; Pile Type 16=Yes; Pile Type 17=Yes; Pile Type 18=No; Pile Type 19=No; Pile Type 20=No; Pile Type 21=No; Pile Type 22=No; Pile Type 23=No; Pile Type 24=No; Pile Type 25=No; Pile Type 26=No; Pile Type 27=No; Pile Type 28=No; Pile Type 29=No; Pile Type 30=No; Pile Type 31=Yes; Pile Type-32=No; Pile Type-33=No; Pile Type-34=No; Pile Type-35=No; Pile Type-36=No; Pile Type-37=Yes; Pile Type-38=No; Pile Type-39=No; Pile Type-40=No; Pile Type-41=No; Pile Type-42=No; Pile Type-43=No; Pile Type-44=No; Pile Type-45=No; Pile Type-46=No; Pile Type-47=No; Pile Type-48=No; Pile Type-49=No; Pile Type-50=No; Pile Type-51=No; Pile Type-52=No; Pile Type-53=No; Pile Type-54=No; Radius=450 mm  [stored 1.47638 ft]; Radius/2=225 mm  [stored 0.738189 ft]; band width=150 mm
- ATK_P15U_900_Diameter: ATK_1.25DIA_Circle_Radius=1125 mm; ATK_2.5_DIA_Circle_Radius=2250 mm; ATK_Pile_DIA=900 mm  [stored 2.95276 ft]; Band Width 2=215 mm; Band Width 3=90 mm; Depth=27000 mm  [stored 88.5827 ft]; Pile Type 01=No; Pile Type 02=No; Pile Type 03=No; Pile Type 04=No; Pile Type 05=No; Pile Type 06=No; Pile Type 07=No; Pile Type 08=No; Pile Type 09=No; Pile Type 10=No; Pile Type 11=No; Pile Type 12=No; Pile Type 13=No; Pile Type 14=No; Pile Type 15=Yes; Pile Type 16=Yes; Pile Type 17=No; Pile Type 18=No; Pile Type 19=No; Pile Type 20=No; Pile Type 21=No; Pile Type 22=No; Pile Type 23=No; Pile Type 24=No; Pile Type 25=No; Pile Type 26=No; Pile Type 27=No; Pile Type 28=No; Pile Type 29=No; Pile Type 30=No; Pile Type 31=Yes; Pile Type-32=No; Pile Type-33=No; Pile Type-34=No; Pile Type-35=No; Pile Type-36=No; Pile Type-37=Yes; Pile Type-38=No; Pile Type-39=No; Pile Type-40=No; Pile Type-41=No; Pile Type-42=No; Pile Type-43=No; Pile Type-44=No; Pile Type-45=No; Pile Type-46=No; Pile Type-47=No; Pile Type-48=No; Pile Type-49=No; Pile Type-50=No; Pile Type-51=No; Pile Type-52=No; Pile Type-53=No; Pile Type-54=No; Radius=450 mm  [stored 1.47638 ft]; Radius/2=225 mm  [stored 0.738189 ft]; band width=150 mm
- ATK_P14U_900_Diameter: ATK_1.25DIA_Circle_Radius=1125 mm; ATK_2.5_DIA_Circle_Radius=2250 mm; ATK_Pile_DIA=900 mm  [stored 2.95276 ft]; Band Width 2=215 mm; Band Width 3=90 mm; Depth=26000 mm  [stored 85.3018 ft]; Pile Type 01=No; Pile Type 02=No; Pile Type 03=No; Pile Type 04=No; Pile Type 05=No; Pile Type 06=No; Pile Type 07=No; Pile Type 08=No; Pile Type 09=No; Pile Type 10=No; Pile Type 11=No; Pile Type 12=No; Pile Type 13=No; Pile Type 14=Yes; Pile Type 15=Yes; Pile Type 16=No; Pile Type 17=No; Pile Type 18=No; Pile Type 19=No; Pile Type 20=No; Pile Type 21=No; Pile Type 22=No; Pile Type 23=No; Pile Type 24=No; Pile Type 25=No; Pile Type 26=No; Pile Type 27=No; Pile Type 28=No; Pile Type 29=No; Pile Type 30=No; Pile Type 31=Yes; Pile Type-32=No; Pile Type-33=No; Pile Type-34=No; Pile Type-35=No; Pile Type-36=No; Pile Type-37=Yes; Pile Type-38=No; Pile Type-39=No; Pile Type-40=No; Pile Type-41=No; Pile Type-42=No; Pile Type-43=No; Pile Type-44=No; Pile Type-45=No; Pile Type-46=No; Pile Type-47=No; Pile Type-48=No; Pile Type-49=No; Pile Type-50=No; Pile Type-51=No; Pile Type-52=No; Pile Type-53=No; Pile Type-54=No; Radius=450 mm  [stored 1.47638 ft]; Radius/2=225 mm  [stored 0.738189 ft]; band width=150 mm
- ATK_P13U_900_Diameter: ATK_1.25DIA_Circle_Radius=1125 mm; ATK_2.5_DIA_Circle_Radius=2250 mm; ATK_Pile_DIA=900 mm  [stored 2.95276 ft]; Band Width 2=215 mm; Band Width 3=90 mm; Depth=25000 mm  [stored 82.021 ft]; Pile Type 01=No; Pile Type 02=No; Pile Type 03=No; Pile Type 04=No; Pile Type 05=No; Pile Type 06=No; Pile Type 07=No; Pile Type 08=No; Pile Type 09=No; Pile Type 10=No; Pile Type 11=No; Pile Type 12=No; Pile Type 13=Yes; Pile Type 14=Yes; Pile Type 15=No; Pile Type 16=No; Pile Type 17=No; Pile Type 18=No; Pile Type 19=No; Pile Type 20=No; Pile Type 21=No; Pile Type 22=No; Pile Type 23=No; Pile Type 24=No; Pile Type 25=No; Pile Type 26=No; Pile Type 27=No; Pile Type 28=No; Pile Type 29=No; Pile Type 30=No; Pile Type 31=Yes; Pile Type-32=No; Pile Type-33=No; Pile Type-34=No; Pile Type-35=No; Pile Type-36=No; Pile Type-37=Yes; Pile Type-38=No; Pile Type-39=No; Pile Type-40=No; Pile Type-41=No; Pile Type-42=No; Pile Type-43=No; Pile Type-44=No; Pile Type-45=No; Pile Type-46=No; Pile Type-47=No; Pile Type-48=No; Pile Type-49=No; Pile Type-50=No; Pile Type-51=No; Pile Type-52=No; Pile Type-53=No; Pile Type-54=No; Radius=450 mm  [stored 1.47638 ft]; Radius/2=225 mm  [stored 0.738189 ft]; band width=150 mm
- ATK_P12U_900_Diameter: ATK_1.25DIA_Circle_Radius=1125 mm; ATK_2.5_DIA_Circle_Radius=2250 mm; ATK_Pile_DIA=900 mm  [stored 2.95276 ft]; Band Width 2=215 mm; Band Width 3=90 mm; Depth=24000 mm  [stored 78.7402 ft]; Pile Type 01=No; Pile Type 02=No; Pile Type 03=No; Pile Type 04=No; Pile Type 05=No; Pile Type 06=No; Pile Type 07=No; Pile Type 08=No; Pile Type 09=No; Pile Type 10=No; Pile Type 11=No; Pile Type 12=Yes; Pile Type 13=Yes; Pile Type 14=No; Pile Type 15=No; Pile Type 16=No; Pile Type 17=No; Pile Type 18=No; Pile Type 19=No; Pile Type 20=No; Pile Type 21=No; Pile Type 22=No; Pile Type 23=No; Pile Type 24=No; Pile Type 25=No; Pile Type 26=No; Pile Type 27=No; Pile Type 28=No; Pile Type 29=No; Pile Type 30=No; Pile Type 31=Yes; Pile Type-32=No; Pile Type-33=No; Pile Type-34=No; Pile Type-35=No; Pile Type-36=No; Pile Type-37=Yes; Pile Type-38=No; Pile Type-39=No; Pile Type-40=No; Pile Type-41=No; Pile Type-42=No; Pile Type-43=No; Pile Type-44=No; Pile Type-45=No; Pile Type-46=No; Pile Type-47=No; Pile Type-48=No; Pile Type-49=No; Pile Type-50=No; Pile Type-51=No; Pile Type-52=No; Pile Type-53=No; Pile Type-54=No; Radius=450 mm  [stored 1.47638 ft]; Radius/2=225 mm  [stored 0.738189 ft]; band width=150 mm
- ATK_P11U_900_Diameter: ATK_1.25DIA_Circle_Radius=1125 mm; ATK_2.5_DIA_Circle_Radius=2250 mm; ATK_Pile_DIA=900 mm  [stored 2.95276 ft]; Band Width 2=215 mm; Band Width 3=90 mm; Depth=23000 mm  [stored 75.4593 ft]; Pile Type 01=No; Pile Type 02=No; Pile Type 03=No; Pile Type 04=No; Pile Type 05=No; Pile Type 06=No; Pile Type 07=No; Pile Type 08=No; Pile Type 09=No; Pile Type 10=No; Pile Type 11=Yes; Pile Type 12=Yes; Pile Type 13=No; Pile Type 14=No; Pile Type 15=No; Pile Type 16=No; Pile Type 17=No; Pile Type 18=No; Pile Type 19=No; Pile Type 20=No; Pile Type 21=No; Pile Type 22=No; Pile Type 23=No; Pile Type 24=No; Pile Type 25=No; Pile Type 26=No; Pile Type 27=No; Pile Type 28=No; Pile Type 29=No; Pile Type 30=No; Pile Type 31=Yes; Pile Type-32=No; Pile Type-33=No; Pile Type-34=No; Pile Type-35=No; Pile Type-36=No; Pile Type-37=Yes; Pile Type-38=No; Pile Type-39=No; Pile Type-40=No; Pile Type-41=No; Pile Type-42=No; Pile Type-43=No; Pile Type-44=No; Pile Type-45=No; Pile Type-46=No; Pile Type-47=No; Pile Type-48=No; Pile Type-49=No; Pile Type-50=No; Pile Type-51=No; Pile Type-52=No; Pile Type-53=No; Pile Type-54=No; Radius=450 mm  [stored 1.47638 ft]; Radius/2=225 mm  [stored 0.738189 ft]; band width=150 mm
- ATK_P10U_900_Diameter: ATK_1.25DIA_Circle_Radius=1125 mm; ATK_2.5_DIA_Circle_Radius=2250 mm; ATK_Pile_DIA=900 mm  [stored 2.95276 ft]; Band Width 2=215 mm; Band Width 3=90 mm; Depth=22000 mm  [stored 72.1785 ft]; Pile Type 01=No; Pile Type 02=No; Pile Type 03=No; Pile Type 04=No; Pile Type 05=No; Pile Type 06=No; Pile Type 07=No; Pile Type 08=No; Pile Type 09=No; Pile Type 10=Yes; Pile Type 11=Yes; Pile Type 12=No; Pile Type 13=No; Pile Type 14=No; Pile Type 15=No; Pile Type 16=No; Pile Type 17=No; Pile Type 18=No; Pile Type 19=No; Pile Type 20=No; Pile Type 21=No; Pile Type 22=No; Pile Type 23=No; Pile Type 24=No; Pile Type 25=No; Pile Type 26=No; Pile Type 27=No; Pile Type 28=No; Pile Type 29=No; Pile Type 30=No; Pile Type 31=Yes; Pile Type-32=No; Pile Type-33=No; Pile Type-34=No; Pile Type-35=No; Pile Type-36=No; Pile Type-37=Yes; Pile Type-38=No; Pile Type-39=No; Pile Type-40=No; Pile Type-41=No; Pile Type-42=No; Pile Type-43=No; Pile Type-44=No; Pile Type-45=No; Pile Type-46=No; Pile Type-47=No; Pile Type-48=No; Pile Type-49=No; Pile Type-50=No; Pile Type-51=No; Pile Type-52=No; Pile Type-53=No; Pile Type-54=No; Radius=450 mm  [stored 1.47638 ft]; Radius/2=225 mm  [stored 0.738189 ft]; band width=150 mm
- ATK_P9U_900_Diameter: ATK_1.25DIA_Circle_Radius=1125 mm; ATK_2.5_DIA_Circle_Radius=2250 mm; ATK_Pile_DIA=900 mm  [stored 2.95276 ft]; Band Width 2=215 mm; Band Width 3=90 mm; Depth=21000 mm  [stored 68.8976 ft]; Pile Type 01=No; Pile Type 02=No; Pile Type 03=No; Pile Type 04=No; Pile Type 05=No; Pile Type 06=No; Pile Type 07=No; Pile Type 08=No; Pile Type 09=Yes; Pile Type 10=Yes; Pile Type 11=No; Pile Type 12=No; Pile Type 13=No; Pile Type 14=No; Pile Type 15=No; Pile Type 16=No; Pile Type 17=No; Pile Type 18=No; Pile Type 19=No; Pile Type 20=No; Pile Type 21=No; Pile Type 22=No; Pile Type 23=No; Pile Type 24=No; Pile Type 25=No; Pile Type 26=No; Pile Type 27=No; Pile Type 28=No; Pile Type 29=No; Pile Type 30=No; Pile Type 31=Yes; Pile Type-32=No; Pile Type-33=No; Pile Type-34=No; Pile Type-35=No; Pile Type-36=No; Pile Type-37=Yes; Pile Type-38=No; Pile Type-39=No; Pile Type-40=No; Pile Type-41=No; Pile Type-42=No; Pile Type-43=No; Pile Type-44=No; Pile Type-45=No; Pile Type-46=No; Pile Type-47=No; Pile Type-48=No; Pile Type-49=No; Pile Type-50=No; Pile Type-51=No; Pile Type-52=No; Pile Type-53=No; Pile Type-54=No; Radius=450 mm  [stored 1.47638 ft]; Radius/2=225 mm  [stored 0.738189 ft]; band width=150 mm
- ATK_P8U_900_Diameter: ATK_1.25DIA_Circle_Radius=1125 mm; ATK_2.5_DIA_Circle_Radius=2250 mm; ATK_Pile_DIA=900 mm  [stored 2.95276 ft]; Band Width 2=215 mm; Band Width 3=90 mm; Depth=20000 mm  [stored 65.6168 ft]; Pile Type 01=No; Pile Type 02=No; Pile Type 03=No; Pile Type 04=No; Pile Type 05=No; Pile Type 06=No; Pile Type 07=No; Pile Type 08=Yes; Pile Type 09=Yes; Pile Type 10=No; Pile Type 11=No; Pile Type 12=No; Pile Type 13=No; Pile Type 14=No; Pile Type 15=No; Pile Type 16=No; Pile Type 17=No; Pile Type 18=No; Pile Type 19=No; Pile Type 20=No; Pile Type 21=No; Pile Type 22=No; Pile Type 23=No; Pile Type 24=No; Pile Type 25=No; Pile Type 26=No; Pile Type 27=No; Pile Type 28=No; Pile Type 29=No; Pile Type 30=No; Pile Type 31=Yes; Pile Type-32=No; Pile Type-33=No; Pile Type-34=No; Pile Type-35=No; Pile Type-36=No; Pile Type-37=Yes; Pile Type-38=No; Pile Type-39=No; Pile Type-40=No; Pile Type-41=No; Pile Type-42=No; Pile Type-43=No; Pile Type-44=No; Pile Type-45=No; Pile Type-46=No; Pile Type-47=No; Pile Type-48=No; Pile Type-49=No; Pile Type-50=No; Pile Type-51=No; Pile Type-52=No; Pile Type-53=No; Pile Type-54=No; Radius=450 mm  [stored 1.47638 ft]; Radius/2=225 mm  [stored 0.738189 ft]; band width=150 mm
- ATK_P6U_900_Diameter: ATK_1.25DIA_Circle_Radius=1125 mm; ATK_2.5_DIA_Circle_Radius=2250 mm; ATK_Pile_DIA=900 mm  [stored 2.95276 ft]; Band Width 2=215 mm; Band Width 3=90 mm; Depth=17000 mm; Pile Type 01=No; Pile Type 02=No; Pile Type 03=No; Pile Type 04=No; Pile Type 05=Yes; Pile Type 06=Yes; Pile Type 07=No; Pile Type 08=No; Pile Type 09=No; Pile Type 10=No; Pile Type 11=No; Pile Type 12=No; Pile Type 13=No; Pile Type 14=No; Pile Type 15=No; Pile Type 16=No; Pile Type 17=No; Pile Type 18=No; Pile Type 19=No; Pile Type 20=No; Pile Type 21=No; Pile Type 22=No; Pile Type 23=No; Pile Type 24=No; Pile Type 25=No; Pile Type 26=No; Pile Type 27=No; Pile Type 28=No; Pile Type 29=No; Pile Type 30=No; Pile Type 31=Yes; Pile Type-32=No; Pile Type-33=No; Pile Type-34=No; Pile Type-35=No; Pile Type-36=No; Pile Type-37=Yes; Pile Type-38=No; Pile Type-39=No; Pile Type-40=No; Pile Type-41=No; Pile Type-42=No; Pile Type-43=No; Pile Type-44=No; Pile Type-45=No; Pile Type-46=No; Pile Type-47=No; Pile Type-48=No; Pile Type-49=No; Pile Type-50=No; Pile Type-51=No; Pile Type-52=No; Pile Type-53=No; Pile Type-54=No; Radius=450 mm  [stored 1.47638 ft]; Radius/2=225 mm  [stored 0.738189 ft]; band width=150 mm
- ATK_P7N_900_Diameter: ATK_1.25DIA_Circle_Radius=1125 mm; ATK_2.5_DIA_Circle_Radius=2250 mm; ATK_Pile_DIA=900 mm  [stored 2.95276 ft]; Band Width 2=215 mm; Band Width 3=90 mm; Depth=19000 mm; Pile Type 01=No; Pile Type 02=No; Pile Type 03=No; Pile Type 04=No; Pile Type 05=No; Pile Type 06=No; Pile Type 07=Yes; Pile Type 08=Yes; Pile Type 09=No; Pile Type 10=No; Pile Type 11=No; Pile Type 12=No; Pile Type 13=No; Pile Type 14=No; Pile Type 15=No; Pile Type 16=No; Pile Type 17=No; Pile Type 18=No; Pile Type 19=No; Pile Type 20=No; Pile Type 21=No; Pile Type 22=No; Pile Type 23=No; Pile Type 24=No; Pile Type 25=No; Pile Type 26=No; Pile Type 27=No; Pile Type 28=No; Pile Type 29=No; Pile Type 30=No; Pile Type 31=Yes; Pile Type-32=No; Pile Type-33=No; Pile Type-34=No; Pile Type-35=No; Pile Type-36=No; Pile Type-37=Yes; Pile Type-38=No; Pile Type-39=No; Pile Type-40=No; Pile Type-41=No; Pile Type-42=No; Pile Type-43=No; Pile Type-44=No; Pile Type-45=No; Pile Type-46=No; Pile Type-47=No; Pile Type-48=No; Pile Type-49=No; Pile Type-50=No; Pile Type-51=No; Pile Type-52=No; Pile Type-53=No; Pile Type-54=No; Radius=450 mm  [stored 1.47638 ft]; Radius/2=225 mm  [stored 0.738189 ft]; band width=150 mm
- ATK_P6N_900_Diameter_Pile 1: ATK_1.25DIA_Circle_Radius=1125 mm; ATK_2.5_DIA_Circle_Radius=2250 mm; ATK_Pile_DIA=900 mm  [stored 2.95276 ft]; Band Width 2=215 mm; Band Width 3=90 mm; Depth=18000 mm; Pile Type 01=No; Pile Type 02=No; Pile Type 03=No; Pile Type 04=No; Pile Type 05=No; Pile Type 06=Yes; Pile Type 07=Yes; Pile Type 08=No; Pile Type 09=No; Pile Type 10=No; Pile Type 11=No; Pile Type 12=No; Pile Type 13=No; Pile Type 14=No; Pile Type 15=No; Pile Type 16=No; Pile Type 17=No; Pile Type 18=No; Pile Type 19=No; Pile Type 20=No; Pile Type 21=No; Pile Type 22=No; Pile Type 23=No; Pile Type 24=No; Pile Type 25=No; Pile Type 26=No; Pile Type 27=No; Pile Type 28=No; Pile Type 29=No; Pile Type 30=No; Pile Type 31=Yes; Pile Type-32=No; Pile Type-33=No; Pile Type-34=No; Pile Type-35=No; Pile Type-36=No; Pile Type-37=Yes; Pile Type-38=No; Pile Type-39=No; Pile Type-40=No; Pile Type-41=No; Pile Type-42=No; Pile Type-43=No; Pile Type-44=No; Pile Type-45=No; Pile Type-46=No; Pile Type-47=No; Pile Type-48=No; Pile Type-49=No; Pile Type-50=No; Pile Type-51=No; Pile Type-52=No; Pile Type-53=No; Pile Type-54=No; Radius=450 mm  [stored 1.47638 ft]; Radius/2=225 mm  [stored 0.738189 ft]; band width=150 mm
- ATK_P4N_900_Diameter_Pile 1: ATK_1.25DIA_Circle_Radius=1125 mm; ATK_2.5_DIA_Circle_Radius=2250 mm; ATK_Pile_DIA=900 mm  [stored 2.95276 ft]; Band Width 2=215 mm; Band Width 3=90 mm; Depth=16000 mm  [stored 52.4934 ft]; Pile Type 01=No; Pile Type 02=No; Pile Type 03=No; Pile Type 04=Yes; Pile Type 05=Yes; Pile Type 06=No; Pile Type 07=No; Pile Type 08=No; Pile Type 09=No; Pile Type 10=No; Pile Type 11=No; Pile Type 12=No; Pile Type 13=No; Pile Type 14=No; Pile Type 15=No; Pile Type 16=No; Pile Type 17=No; Pile Type 18=No; Pile Type 19=No; Pile Type 20=No; Pile Type 21=No; Pile Type 22=No; Pile Type 23=No; Pile Type 24=No; Pile Type 25=No; Pile Type 26=No; Pile Type 27=No; Pile Type 28=No; Pile Type 29=No; Pile Type 30=No; Pile Type 31=Yes; Pile Type-32=No; Pile Type-33=No; Pile Type-34=No; Pile Type-35=No; Pile Type-36=No; Pile Type-37=Yes; Pile Type-38=No; Pile Type-39=No; Pile Type-40=No; Pile Type-41=No; Pile Type-42=No; Pile Type-43=No; Pile Type-44=No; Pile Type-45=No; Pile Type-46=No; Pile Type-47=No; Pile Type-48=No; Pile Type-49=No; Pile Type-50=No; Pile Type-51=No; Pile Type-52=No; Pile Type-53=No; Pile Type-54=No; Radius=450 mm  [stored 1.47638 ft]; Radius/2=225 mm  [stored 0.738189 ft]; band width=150 mm
- ATK_P10R_1000_Diameter: ATK_1.25DIA_Circle_Radius=1250 mm  [stored 4.10105 ft]; ATK_2.5_DIA_Circle_Radius=2500 mm  [stored 8.2021 ft]; ATK_Pile_DIA=1000 mm  [stored 3.28084 ft]; Band Width 2=240 mm; Band Width 3=100 mm  [stored 0.328084 ft]; Depth=22000 mm  [stored 72.1785 ft]; Pile Type 01=No; Pile Type 02=Yes; Pile Type 03=No; Pile Type 04=No; Pile Type 05=No; Pile Type 06=No; Pile Type 07=No; Pile Type 08=No; Pile Type 09=No; Pile Type 10=Yes; Pile Type 11=No; Pile Type 12=No; Pile Type 13=No; Pile Type 14=No; Pile Type 15=No; Pile Type 16=No; Pile Type 17=No; Pile Type 18=No; Pile Type 19=No; Pile Type 20=No; Pile Type 21=No; Pile Type 22=No; Pile Type 23=No; Pile Type 24=No; Pile Type 25=No; Pile Type 26=No; Pile Type 27=No; Pile Type 28=No; Pile Type 29=No; Pile Type 30=No; Pile Type 31=Yes; Pile Type-32=No; Pile Type-33=No; Pile Type-34=No; Pile Type-35=No; Pile Type-36=No; Pile Type-37=Yes; Pile Type-38=No; Pile Type-39=No; Pile Type-40=No; Pile Type-41=No; Pile Type-42=No; Pile Type-43=No; Pile Type-44=No; Pile Type-45=No; Pile Type-46=No; Pile Type-47=No; Pile Type-48=No; Pile Type-49=No; Pile Type-50=No; Pile Type-51=No; Pile Type-52=No; Pile Type-53=No; Pile Type-54=No; Radius=500 mm  [stored 1.64042 ft]; Radius/2=250 mm  [stored 0.82021 ft]; band width=167 mm
- ATK_P16T_1000_Diameter_Pile: ATK_1.25DIA_Circle_Radius=1250 mm  [stored 4.10105 ft]; ATK_2.5_DIA_Circle_Radius=2500 mm  [stored 8.2021 ft]; ATK_Pile_DIA=1000 mm  [stored 3.28084 ft]; Band Width 2=240 mm; Band Width 3=100 mm  [stored 0.328084 ft]; Depth=28000 mm  [stored 91.8635 ft]; Pile Type 01=No; Pile Type 02=No; Pile Type 03=No; Pile Type 04=No; Pile Type 05=No; Pile Type 06=No; Pile Type 07=No; Pile Type 08=Yes; Pile Type 09=No; Pile Type 10=No; Pile Type 11=No; Pile Type 12=No; Pile Type 13=No; Pile Type 14=No; Pile Type 15=No; Pile Type 16=Yes; Pile Type 17=No; Pile Type 18=No; Pile Type 19=No; Pile Type 20=No; Pile Type 21=No; Pile Type 22=No; Pile Type 23=No; Pile Type 24=No; Pile Type 25=No; Pile Type 26=No; Pile Type 27=No; Pile Type 28=No; Pile Type 29=No; Pile Type 30=No; Pile Type 31=Yes; Pile Type-32=No; Pile Type-33=No; Pile Type-34=No; Pile Type-35=No; Pile Type-36=No; Pile Type-37=Yes; Pile Type-38=No; Pile Type-39=No; Pile Type-40=No; Pile Type-41=No; Pile Type-42=No; Pile Type-43=No; Pile Type-44=No; Pile Type-45=No; Pile Type-46=No; Pile Type-47=No; Pile Type-48=No; Pile Type-49=No; Pile Type-50=No; Pile Type-51=No; Pile Type-52=No; Pile Type-53=No; Pile Type-54=No; Radius=500 mm  [stored 1.64042 ft]; Radius/2=250 mm  [stored 0.82021 ft]; band width=167 mm
- ATK_P15T_1000_Diameter_Pile: ATK_1.25DIA_Circle_Radius=1250 mm  [stored 4.10105 ft]; ATK_2.5_DIA_Circle_Radius=2500 mm  [stored 8.2021 ft]; ATK_Pile_DIA=1000 mm  [stored 3.28084 ft]; Band Width 2=240 mm; Band Width 3=100 mm  [stored 0.328084 ft]; Depth=27000 mm  [stored 88.5827 ft]; Pile Type 01=No; Pile Type 02=No; Pile Type 03=No; Pile Type 04=No; Pile Type 05=No; Pile Type 06=No; Pile Type 07=Yes; Pile Type 08=No; Pile Type 09=No; Pile Type 10=No; Pile Type 11=No; Pile Type 12=No; Pile Type 13=No; Pile Type 14=No; Pile Type 15=Yes; Pile Type 16=No; Pile Type 17=No; Pile Type 18=No; Pile Type 19=No; Pile Type 20=No; Pile Type 21=No; Pile Type 22=No; Pile Type 23=No; Pile Type 24=No; Pile Type 25=No; Pile Type 26=No; Pile Type 27=No; Pile Type 28=No; Pile Type 29=No; Pile Type 30=No; Pile Type 31=Yes; Pile Type-32=No; Pile Type-33=No; Pile Type-34=No; Pile Type-35=No; Pile Type-36=No; Pile Type-37=Yes; Pile Type-38=No; Pile Type-39=No; Pile Type-40=No; Pile Type-41=No; Pile Type-42=No; Pile Type-43=No; Pile Type-44=No; Pile Type-45=No; Pile Type-46=No; Pile Type-47=No; Pile Type-48=No; Pile Type-49=No; Pile Type-50=No; Pile Type-51=No; Pile Type-52=No; Pile Type-53=No; Pile Type-54=No; Radius=500 mm  [stored 1.64042 ft]; Radius/2=250 mm  [stored 0.82021 ft]; band width=167 mm
- ATK_P14T_1000_Diameter_Pile: ATK_1.25DIA_Circle_Radius=1250 mm  [stored 4.10105 ft]; ATK_2.5_DIA_Circle_Radius=2500 mm  [stored 8.2021 ft]; ATK_Pile_DIA=1000 mm  [stored 3.28084 ft]; Band Width 2=240 mm; Band Width 3=100 mm  [stored 0.328084 ft]; Depth=26000 mm  [stored 85.3018 ft]; Pile Type 01=No; Pile Type 02=No; Pile Type 03=No; Pile Type 04=No; Pile Type 05=No; Pile Type 06=Yes; Pile Type 07=No; Pile Type 08=No; Pile Type 09=No; Pile Type 10=No; Pile Type 11=No; Pile Type 12=No; Pile Type 13=No; Pile Type 14=Yes; Pile Type 15=No; Pile Type 16=No; Pile Type 17=No; Pile Type 18=No; Pile Type 19=No; Pile Type 20=No; Pile Type 21=No; Pile Type 22=No; Pile Type 23=No; Pile Type 24=No; Pile Type 25=No; Pile Type 26=No; Pile Type 27=No; Pile Type 28=No; Pile Type 29=No; Pile Type 30=No; Pile Type 31=Yes; Pile Type-32=No; Pile Type-33=No; Pile Type-34=No; Pile Type-35=No; Pile Type-36=No; Pile Type-37=Yes; Pile Type-38=No; Pile Type-39=No; Pile Type-40=No; Pile Type-41=No; Pile Type-42=No; Pile Type-43=No; Pile Type-44=No; Pile Type-45=No; Pile Type-46=No; Pile Type-47=No; Pile Type-48=No; Pile Type-49=No; Pile Type-50=No; Pile Type-51=No; Pile Type-52=No; Pile Type-53=No; Pile Type-54=No; Radius=500 mm  [stored 1.64042 ft]; Radius/2=250 mm  [stored 0.82021 ft]; band width=167 mm
- ATK_P13T_1000_Diameter_Pile: ATK_1.25DIA_Circle_Radius=1250 mm  [stored 4.10105 ft]; ATK_2.5_DIA_Circle_Radius=2500 mm  [stored 8.2021 ft]; ATK_Pile_DIA=1000 mm  [stored 3.28084 ft]; Band Width 2=240 mm; Band Width 3=100 mm  [stored 0.328084 ft]; Depth=25000 mm  [stored 82.021 ft]; Pile Type 01=No; Pile Type 02=No; Pile Type 03=No; Pile Type 04=No; Pile Type 05=Yes; Pile Type 06=No; Pile Type 07=No; Pile Type 08=No; Pile Type 09=No; Pile Type 10=No; Pile Type 11=No; Pile Type 12=No; Pile Type 13=Yes; Pile Type 14=No; Pile Type 15=No; Pile Type 16=No; Pile Type 17=No; Pile Type 18=No; Pile Type 19=No; Pile Type 20=No; Pile Type 21=No; Pile Type 22=No; Pile Type 23=No; Pile Type 24=No; Pile Type 25=No; Pile Type 26=No; Pile Type 27=No; Pile Type 28=No; Pile Type 29=No; Pile Type 30=No; Pile Type 31=Yes; Pile Type-32=No; Pile Type-33=No; Pile Type-34=No; Pile Type-35=No; Pile Type-36=No; Pile Type-37=Yes; Pile Type-38=No; Pile Type-39=No; Pile Type-40=No; Pile Type-41=No; Pile Type-42=No; Pile Type-43=No; Pile Type-44=No; Pile Type-45=No; Pile Type-46=No; Pile Type-47=No; Pile Type-48=No; Pile Type-49=No; Pile Type-50=No; Pile Type-51=No; Pile Type-52=No; Pile Type-53=No; Pile Type-54=No; Radius=500 mm  [stored 1.64042 ft]; Radius/2=250 mm  [stored 0.82021 ft]; band width=167 mm
- ATK_P12T_1000_Diameter_Pile: ATK_1.25DIA_Circle_Radius=1250 mm  [stored 4.10105 ft]; ATK_2.5_DIA_Circle_Radius=2500 mm  [stored 8.2021 ft]; ATK_Pile_DIA=1000 mm  [stored 3.28084 ft]; Band Width 2=240 mm; Band Width 3=100 mm  [stored 0.328084 ft]; Depth=24000 mm  [stored 78.7402 ft]; Pile Type 01=No; Pile Type 02=No; Pile Type 03=No; Pile Type 04=Yes; Pile Type 05=No; Pile Type 06=No; Pile Type 07=No; Pile Type 08=No; Pile Type 09=No; Pile Type 10=No; Pile Type 11=No; Pile Type 12=Yes; Pile Type 13=No; Pile Type 14=No; Pile Type 15=No; Pile Type 16=No; Pile Type 17=No; Pile Type 18=No; Pile Type 19=No; Pile Type 20=No; Pile Type 21=No; Pile Type 22=No; Pile Type 23=No; Pile Type 24=No; Pile Type 25=No; Pile Type 26=No; Pile Type 27=No; Pile Type 28=No; Pile Type 29=No; Pile Type 30=No; Pile Type 31=Yes; Pile Type-32=No; Pile Type-33=No; Pile Type-34=No; Pile Type-35=No; Pile Type-36=No; Pile Type-37=Yes; Pile Type-38=No; Pile Type-39=No; Pile Type-40=No; Pile Type-41=No; Pile Type-42=No; Pile Type-43=No; Pile Type-44=No; Pile Type-45=No; Pile Type-46=No; Pile Type-47=No; Pile Type-48=No; Pile Type-49=No; Pile Type-50=No; Pile Type-51=No; Pile Type-52=No; Pile Type-53=No; Pile Type-54=No; Radius=500 mm  [stored 1.64042 ft]; Radius/2=250 mm  [stored 0.82021 ft]; band width=167 mm
- ATK_P11T_1000_Diameter_Pile: ATK_1.25DIA_Circle_Radius=1250 mm  [stored 4.10105 ft]; ATK_2.5_DIA_Circle_Radius=2500 mm  [stored 8.2021 ft]; ATK_Pile_DIA=1000 mm  [stored 3.28084 ft]; Band Width 2=240 mm; Band Width 3=100 mm  [stored 0.328084 ft]; Depth=23000 mm  [stored 75.4593 ft]; Pile Type 01=No; Pile Type 02=No; Pile Type 03=Yes; Pile Type 04=No; Pile Type 05=No; Pile Type 06=No; Pile Type 07=No; Pile Type 08=No; Pile Type 09=No; Pile Type 10=No; Pile Type 11=Yes; Pile Type 12=No; Pile Type 13=No; Pile Type 14=No; Pile Type 15=No; Pile Type 16=No; Pile Type 17=No; Pile Type 18=No; Pile Type 19=No; Pile Type 20=No; Pile Type 21=No; Pile Type 22=No; Pile Type 23=No; Pile Type 24=No; Pile Type 25=No; Pile Type 26=No; Pile Type 27=No; Pile Type 28=No; Pile Type 29=No; Pile Type 30=No; Pile Type 31=Yes; Pile Type-32=No; Pile Type-33=No; Pile Type-34=No; Pile Type-35=No; Pile Type-36=No; Pile Type-37=Yes; Pile Type-38=No; Pile Type-39=No; Pile Type-40=No; Pile Type-41=No; Pile Type-42=No; Pile Type-43=No; Pile Type-44=No; Pile Type-45=No; Pile Type-46=No; Pile Type-47=No; Pile Type-48=No; Pile Type-49=No; Pile Type-50=No; Pile Type-51=No; Pile Type-52=No; Pile Type-53=No; Pile Type-54=No; Radius=500 mm  [stored 1.64042 ft]; Radius/2=250 mm  [stored 0.82021 ft]; band width=167 mm
- ATK_P10T_1000_Diameter_Pile: ATK_1.25DIA_Circle_Radius=1250 mm  [stored 4.10105 ft]; ATK_2.5_DIA_Circle_Radius=2500 mm  [stored 8.2021 ft]; ATK_Pile_DIA=1000 mm  [stored 3.28084 ft]; Band Width 2=240 mm; Band Width 3=100 mm  [stored 0.328084 ft]; Depth=22000 mm  [stored 72.1785 ft]; Pile Type 01=No; Pile Type 02=Yes; Pile Type 03=No; Pile Type 04=No; Pile Type 05=No; Pile Type 06=No; Pile Type 07=No; Pile Type 08=No; Pile Type 09=No; Pile Type 10=Yes; Pile Type 11=No; Pile Type 12=No; Pile Type 13=No; Pile Type 14=No; Pile Type 15=No; Pile Type 16=No; Pile Type 17=No; Pile Type 18=No; Pile Type 19=No; Pile Type 20=No; Pile Type 21=No; Pile Type 22=No; Pile Type 23=No; Pile Type 24=No; Pile Type 25=No; Pile Type 26=No; Pile Type 27=No; Pile Type 28=No; Pile Type 29=No; Pile Type 30=No; Pile Type 31=Yes; Pile Type-32=No; Pile Type-33=No; Pile Type-34=No; Pile Type-35=No; Pile Type-36=No; Pile Type-37=Yes; Pile Type-38=No; Pile Type-39=No; Pile Type-40=No; Pile Type-41=No; Pile Type-42=No; Pile Type-43=No; Pile Type-44=No; Pile Type-45=No; Pile Type-46=No; Pile Type-47=No; Pile Type-48=No; Pile Type-49=No; Pile Type-50=No; Pile Type-51=No; Pile Type-52=No; Pile Type-53=No; Pile Type-54=No; Radius=500 mm  [stored 1.64042 ft]; Radius/2=250 mm  [stored 0.82021 ft]; band width=167 mm
- ATK_P9T_1000_Diameter_Pile: ATK_1.25DIA_Circle_Radius=1250 mm  [stored 4.10105 ft]; ATK_2.5_DIA_Circle_Radius=2500 mm  [stored 8.2021 ft]; ATK_Pile_DIA=1000 mm  [stored 3.28084 ft]; Band Width 2=240 mm; Band Width 3=100 mm  [stored 0.328084 ft]; Depth=21000 mm  [stored 68.8976 ft]; Pile Type 01=No; Pile Type 02=No; Pile Type 03=No; Pile Type 04=No; Pile Type 05=No; Pile Type 06=No; Pile Type 07=No; Pile Type 08=No; Pile Type 09=Yes; Pile Type 10=No; Pile Type 11=No; Pile Type 12=No; Pile Type 13=No; Pile Type 14=No; Pile Type 15=No; Pile Type 16=No; Pile Type 17=No; Pile Type 18=No; Pile Type 19=Yes; Pile Type 20=No; Pile Type 21=No; Pile Type 22=No; Pile Type 23=No; Pile Type 24=No; Pile Type 25=No; Pile Type 26=No; Pile Type 27=No; Pile Type 28=No; Pile Type 29=No; Pile Type 30=No; Pile Type 31=Yes; Pile Type-32=No; Pile Type-33=No; Pile Type-34=No; Pile Type-35=No; Pile Type-36=No; Pile Type-37=Yes; Pile Type-38=No; Pile Type-39=No; Pile Type-40=No; Pile Type-41=No; Pile Type-42=No; Pile Type-43=No; Pile Type-44=No; Pile Type-45=No; Pile Type-46=No; Pile Type-47=No; Pile Type-48=No; Pile Type-49=No; Pile Type-50=No; Pile Type-51=No; Pile Type-52=No; Pile Type-53=No; Pile Type-54=No; Radius=500 mm  [stored 1.64042 ft]; Radius/2=250 mm  [stored 0.82021 ft]; band width=167 mm
- ATK_P8T_1000_Diameter_Pile: ATK_1.25DIA_Circle_Radius=1250 mm  [stored 4.10105 ft]; ATK_2.5_DIA_Circle_Radius=2500 mm  [stored 8.2021 ft]; ATK_Pile_DIA=1000 mm  [stored 3.28084 ft]; Band Width 2=240 mm; Band Width 3=100 mm  [stored 0.328084 ft]; Depth=20000 mm  [stored 65.6168 ft]; Pile Type 01=No; Pile Type 02=No; Pile Type 03=No; Pile Type 04=No; Pile Type 05=No; Pile Type 06=No; Pile Type 07=No; Pile Type 08=Yes; Pile Type 09=No; Pile Type 10=No; Pile Type 11=No; Pile Type 12=No; Pile Type 13=No; Pile Type 14=No; Pile Type 15=No; Pile Type 16=No; Pile Type 17=No; Pile Type 18=Yes; Pile Type 19=No; Pile Type 20=No; Pile Type 21=No; Pile Type 22=No; Pile Type 23=No; Pile Type 24=No; Pile Type 25=No; Pile Type 26=No; Pile Type 27=No; Pile Type 28=No; Pile Type 29=No; Pile Type 30=No; Pile Type 31=Yes; Pile Type-32=No; Pile Type-33=No; Pile Type-34=No; Pile Type-35=No; Pile Type-36=No; Pile Type-37=Yes; Pile Type-38=No; Pile Type-39=No; Pile Type-40=No; Pile Type-41=No; Pile Type-42=No; Pile Type-43=No; Pile Type-44=No; Pile Type-45=No; Pile Type-46=No; Pile Type-47=No; Pile Type-48=No; Pile Type-49=No; Pile Type-50=No; Pile Type-51=No; Pile Type-52=No; Pile Type-53=No; Pile Type-54=No; Radius=500 mm  [stored 1.64042 ft]; Radius/2=250 mm  [stored 0.82021 ft]; band width=167 mm
- ATK_P18U_900_Diameter_Pile: ATK_1.25DIA_Circle_Radius=1125 mm; ATK_2.5_DIA_Circle_Radius=2250 mm; ATK_Pile_DIA=900 mm  [stored 2.95276 ft]; Band Width 2=215 mm; Band Width 3=90 mm; Depth=30000 mm; Pile Type 01=No; Pile Type 02=No; Pile Type 03=No; Pile Type 04=No; Pile Type 05=No; Pile Type 06=No; Pile Type 07=No; Pile Type 08=No; Pile Type 09=No; Pile Type 10=No; Pile Type 11=No; Pile Type 12=No; Pile Type 13=No; Pile Type 14=No; Pile Type 15=No; Pile Type 16=No; Pile Type 17=No; Pile Type 18=Yes; Pile Type 19=Yes; Pile Type 20=No; Pile Type 21=No; Pile Type 22=No; Pile Type 23=No; Pile Type 24=No; Pile Type 25=No; Pile Type 26=No; Pile Type 27=No; Pile Type 28=No; Pile Type 29=No; Pile Type 30=No; Pile Type 31=Yes; Pile Type-32=No; Pile Type-33=No; Pile Type-34=No; Pile Type-35=No; Pile Type-36=No; Pile Type-37=Yes; Pile Type-38=No; Pile Type-39=No; Pile Type-40=No; Pile Type-41=No; Pile Type-42=No; Pile Type-43=No; Pile Type-44=No; Pile Type-45=No; Pile Type-46=No; Pile Type-47=No; Pile Type-48=No; Pile Type-49=No; Pile Type-50=No; Pile Type-51=No; Pile Type-52=No; Pile Type-53=No; Pile Type-54=No; Radius=450 mm  [stored 1.47638 ft]; Radius/2=225 mm  [stored 0.738189 ft]; band width=150 mm
- ATK_P17U_900_Diameter_Pile: ATK_1.25DIA_Circle_Radius=1125 mm; ATK_2.5_DIA_Circle_Radius=2250 mm; ATK_Pile_DIA=900 mm  [stored 2.95276 ft]; Band Width 2=215 mm; Band Width 3=90 mm; Depth=29000 mm; Pile Type 01=No; Pile Type 02=No; Pile Type 03=No; Pile Type 04=No; Pile Type 05=No; Pile Type 06=No; Pile Type 07=No; Pile Type 08=No; Pile Type 09=No; Pile Type 10=No; Pile Type 11=No; Pile Type 12=No; Pile Type 13=No; Pile Type 14=No; Pile Type 15=No; Pile Type 16=No; Pile Type 17=Yes; Pile Type 18=Yes; Pile Type 19=No; Pile Type 20=No; Pile Type 21=No; Pile Type 22=No; Pile Type 23=No; Pile Type 24=No; Pile Type 25=No; Pile Type 26=No; Pile Type 27=No; Pile Type 28=No; Pile Type 29=No; Pile Type 30=No; Pile Type 31=Yes; Pile Type-32=No; Pile Type-33=No; Pile Type-34=No; Pile Type-35=No; Pile Type-36=No; Pile Type-37=Yes; Pile Type-38=No; Pile Type-39=No; Pile Type-40=No; Pile Type-41=No; Pile Type-42=No; Pile Type-43=No; Pile Type-44=No; Pile Type-45=No; Pile Type-46=No; Pile Type-47=No; Pile Type-48=No; Pile Type-49=No; Pile Type-50=No; Pile Type-51=No; Pile Type-52=No; Pile Type-53=No; Pile Type-54=No; Radius=450 mm  [stored 1.47638 ft]; Radius/2=225 mm  [stored 0.738189 ft]; band width=150 mm
- ATK_P16U_900_Diameter_Pile: ATK_1.25DIA_Circle_Radius=1125 mm; ATK_2.5_DIA_Circle_Radius=2250 mm; ATK_Pile_DIA=900 mm  [stored 2.95276 ft]; Band Width 2=215 mm; Band Width 3=90 mm; Depth=28000 mm  [stored 91.8635 ft]; Pile Type 01=No; Pile Type 02=No; Pile Type 03=No; Pile Type 04=No; Pile Type 05=No; Pile Type 06=No; Pile Type 07=No; Pile Type 08=No; Pile Type 09=No; Pile Type 10=No; Pile Type 11=No; Pile Type 12=No; Pile Type 13=No; Pile Type 14=No; Pile Type 15=No; Pile Type 16=Yes; Pile Type 17=Yes; Pile Type 18=No; Pile Type 19=No; Pile Type 20=No; Pile Type 21=No; Pile Type 22=No; Pile Type 23=No; Pile Type 24=No; Pile Type 25=No; Pile Type 26=No; Pile Type 27=No; Pile Type 28=No; Pile Type 29=No; Pile Type 30=No; Pile Type 31=Yes; Pile Type-32=No; Pile Type-33=No; Pile Type-34=No; Pile Type-35=No; Pile Type-36=No; Pile Type-37=Yes; Pile Type-38=No; Pile Type-39=No; Pile Type-40=No; Pile Type-41=No; Pile Type-42=No; Pile Type-43=No; Pile Type-44=No; Pile Type-45=No; Pile Type-46=No; Pile Type-47=No; Pile Type-48=No; Pile Type-49=No; Pile Type-50=No; Pile Type-51=No; Pile Type-52=No; Pile Type-53=No; Pile Type-54=No; Radius=450 mm  [stored 1.47638 ft]; Radius/2=225 mm  [stored 0.738189 ft]; band width=150 mm
- ATK_P15U_900_Diameter_Pile: ATK_1.25DIA_Circle_Radius=1125 mm; ATK_2.5_DIA_Circle_Radius=2250 mm; ATK_Pile_DIA=900 mm  [stored 2.95276 ft]; Band Width 2=215 mm; Band Width 3=90 mm; Depth=27000 mm  [stored 88.5827 ft]; Pile Type 01=No; Pile Type 02=No; Pile Type 03=No; Pile Type 04=No; Pile Type 05=No; Pile Type 06=No; Pile Type 07=No; Pile Type 08=No; Pile Type 09=No; Pile Type 10=No; Pile Type 11=No; Pile Type 12=No; Pile Type 13=No; Pile Type 14=No; Pile Type 15=Yes; Pile Type 16=Yes; Pile Type 17=No; Pile Type 18=No; Pile Type 19=No; Pile Type 20=No; Pile Type 21=No; Pile Type 22=No; Pile Type 23=No; Pile Type 24=No; Pile Type 25=No; Pile Type 26=No; Pile Type 27=No; Pile Type 28=No; Pile Type 29=No; Pile Type 30=No; Pile Type 31=Yes; Pile Type-32=No; Pile Type-33=No; Pile Type-34=No; Pile Type-35=No; Pile Type-36=No; Pile Type-37=Yes; Pile Type-38=No; Pile Type-39=No; Pile Type-40=No; Pile Type-41=No; Pile Type-42=No; Pile Type-43=No; Pile Type-44=No; Pile Type-45=No; Pile Type-46=No; Pile Type-47=No; Pile Type-48=No; Pile Type-49=No; Pile Type-50=No; Pile Type-51=No; Pile Type-52=No; Pile Type-53=No; Pile Type-54=No; Radius=450 mm  [stored 1.47638 ft]; Radius/2=225 mm  [stored 0.738189 ft]; band width=150 mm
- ATK_P14U_900_Diameter_Pile: ATK_1.25DIA_Circle_Radius=1125 mm; ATK_2.5_DIA_Circle_Radius=2250 mm; ATK_Pile_DIA=900 mm  [stored 2.95276 ft]; Band Width 2=215 mm; Band Width 3=90 mm; Depth=26000 mm  [stored 85.3018 ft]; Pile Type 01=No; Pile Type 02=No; Pile Type 03=No; Pile Type 04=No; Pile Type 05=No; Pile Type 06=No; Pile Type 07=No; Pile Type 08=No; Pile Type 09=No; Pile Type 10=No; Pile Type 11=No; Pile Type 12=No; Pile Type 13=No; Pile Type 14=Yes; Pile Type 15=Yes; Pile Type 16=No; Pile Type 17=No; Pile Type 18=No; Pile Type 19=No; Pile Type 20=No; Pile Type 21=No; Pile Type 22=No; Pile Type 23=No; Pile Type 24=No; Pile Type 25=No; Pile Type 26=No; Pile Type 27=No; Pile Type 28=No; Pile Type 29=No; Pile Type 30=No; Pile Type 31=Yes; Pile Type-32=No; Pile Type-33=No; Pile Type-34=No; Pile Type-35=No; Pile Type-36=No; Pile Type-37=Yes; Pile Type-38=No; Pile Type-39=No; Pile Type-40=No; Pile Type-41=No; Pile Type-42=No; Pile Type-43=No; Pile Type-44=No; Pile Type-45=No; Pile Type-46=No; Pile Type-47=No; Pile Type-48=No; Pile Type-49=No; Pile Type-50=No; Pile Type-51=No; Pile Type-52=No; Pile Type-53=No; Pile Type-54=No; Radius=450 mm  [stored 1.47638 ft]; Radius/2=225 mm  [stored 0.738189 ft]; band width=150 mm
- ATK_P13U_900_Diameter_Pile: ATK_1.25DIA_Circle_Radius=1125 mm; ATK_2.5_DIA_Circle_Radius=2250 mm; ATK_Pile_DIA=900 mm  [stored 2.95276 ft]; Band Width 2=215 mm; Band Width 3=90 mm; Depth=25000 mm  [stored 82.021 ft]; Pile Type 01=No; Pile Type 02=No; Pile Type 03=No; Pile Type 04=No; Pile Type 05=No; Pile Type 06=No; Pile Type 07=No; Pile Type 08=No; Pile Type 09=No; Pile Type 10=No; Pile Type 11=No; Pile Type 12=No; Pile Type 13=Yes; Pile Type 14=Yes; Pile Type 15=No; Pile Type 16=No; Pile Type 17=No; Pile Type 18=No; Pile Type 19=No; Pile Type 20=No; Pile Type 21=No; Pile Type 22=No; Pile Type 23=No; Pile Type 24=No; Pile Type 25=No; Pile Type 26=No; Pile Type 27=No; Pile Type 28=No; Pile Type 29=No; Pile Type 30=No; Pile Type 31=Yes; Pile Type-32=No; Pile Type-33=No; Pile Type-34=No; Pile Type-35=No; Pile Type-36=No; Pile Type-37=Yes; Pile Type-38=No; Pile Type-39=No; Pile Type-40=No; Pile Type-41=No; Pile Type-42=No; Pile Type-43=No; Pile Type-44=No; Pile Type-45=No; Pile Type-46=No; Pile Type-47=No; Pile Type-48=No; Pile Type-49=No; Pile Type-50=No; Pile Type-51=No; Pile Type-52=No; Pile Type-53=No; Pile Type-54=No; Radius=450 mm  [stored 1.47638 ft]; Radius/2=225 mm  [stored 0.738189 ft]; band width=150 mm
- ATK_P12U_900_Diameter_Pile: ATK_1.25DIA_Circle_Radius=1125 mm; ATK_2.5_DIA_Circle_Radius=2250 mm; ATK_Pile_DIA=900 mm  [stored 2.95276 ft]; Band Width 2=215 mm; Band Width 3=90 mm; Depth=24000 mm  [stored 78.7402 ft]; Pile Type 01=No; Pile Type 02=No; Pile Type 03=No; Pile Type 04=No; Pile Type 05=No; Pile Type 06=No; Pile Type 07=No; Pile Type 08=No; Pile Type 09=No; Pile Type 10=No; Pile Type 11=No; Pile Type 12=Yes; Pile Type 13=Yes; Pile Type 14=No; Pile Type 15=No; Pile Type 16=No; Pile Type 17=No; Pile Type 18=No; Pile Type 19=No; Pile Type 20=No; Pile Type 21=No; Pile Type 22=No; Pile Type 23=No; Pile Type 24=No; Pile Type 25=No; Pile Type 26=No; Pile Type 27=No; Pile Type 28=No; Pile Type 29=No; Pile Type 30=No; Pile Type 31=Yes; Pile Type-32=No; Pile Type-33=No; Pile Type-34=No; Pile Type-35=No; Pile Type-36=No; Pile Type-37=Yes; Pile Type-38=No; Pile Type-39=No; Pile Type-40=No; Pile Type-41=No; Pile Type-42=No; Pile Type-43=No; Pile Type-44=No; Pile Type-45=No; Pile Type-46=No; Pile Type-47=No; Pile Type-48=No; Pile Type-49=No; Pile Type-50=No; Pile Type-51=No; Pile Type-52=No; Pile Type-53=No; Pile Type-54=No; Radius=450 mm  [stored 1.47638 ft]; Radius/2=225 mm  [stored 0.738189 ft]; band width=150 mm
- ATK_P11U_750_Diameter_Pile: ATK_1.25DIA_Circle_Radius=1125 mm; ATK_2.5_DIA_Circle_Radius=2250 mm; ATK_Pile_DIA=900 mm  [stored 2.95276 ft]; Band Width 2=215 mm; Band Width 3=90 mm; Depth=23000 mm  [stored 75.4593 ft]; Pile Type 01=No; Pile Type 02=No; Pile Type 03=No; Pile Type 04=No; Pile Type 05=No; Pile Type 06=No; Pile Type 07=No; Pile Type 08=No; Pile Type 09=No; Pile Type 10=No; Pile Type 11=Yes; Pile Type 12=Yes; Pile Type 13=No; Pile Type 14=No; Pile Type 15=No; Pile Type 16=No; Pile Type 17=No; Pile Type 18=No; Pile Type 19=No; Pile Type 20=No; Pile Type 21=No; Pile Type 22=No; Pile Type 23=No; Pile Type 24=No; Pile Type 25=No; Pile Type 26=No; Pile Type 27=No; Pile Type 28=No; Pile Type 29=No; Pile Type 30=No; Pile Type 31=Yes; Pile Type-32=No; Pile Type-33=No; Pile Type-34=No; Pile Type-35=No; Pile Type-36=No; Pile Type-37=Yes; Pile Type-38=No; Pile Type-39=No; Pile Type-40=No; Pile Type-41=No; Pile Type-42=No; Pile Type-43=No; Pile Type-44=No; Pile Type-45=No; Pile Type-46=No; Pile Type-47=No; Pile Type-48=No; Pile Type-49=No; Pile Type-50=No; Pile Type-51=No; Pile Type-52=No; Pile Type-53=No; Pile Type-54=No; Radius=450 mm  [stored 1.47638 ft]; Radius/2=225 mm  [stored 0.738189 ft]; band width=150 mm
- ATK_P10U_900_Diameter_Pile: ATK_1.25DIA_Circle_Radius=1125 mm; ATK_2.5_DIA_Circle_Radius=2250 mm; ATK_Pile_DIA=900 mm  [stored 2.95276 ft]; Band Width 2=215 mm; Band Width 3=90 mm; Depth=22000 mm  [stored 72.1785 ft]; Pile Type 01=No; Pile Type 02=No; Pile Type 03=No; Pile Type 04=No; Pile Type 05=No; Pile Type 06=No; Pile Type 07=No; Pile Type 08=No; Pile Type 09=No; Pile Type 10=Yes; Pile Type 11=Yes; Pile Type 12=No; Pile Type 13=No; Pile Type 14=No; Pile Type 15=No; Pile Type 16=No; Pile Type 17=No; Pile Type 18=No; Pile Type 19=No; Pile Type 20=No; Pile Type 21=No; Pile Type 22=No; Pile Type 23=No; Pile Type 24=No; Pile Type 25=No; Pile Type 26=No; Pile Type 27=No; Pile Type 28=No; Pile Type 29=No; Pile Type 30=No; Pile Type 31=Yes; Pile Type-32=No; Pile Type-33=No; Pile Type-34=No; Pile Type-35=No; Pile Type-36=No; Pile Type-37=Yes; Pile Type-38=No; Pile Type-39=No; Pile Type-40=No; Pile Type-41=No; Pile Type-42=No; Pile Type-43=No; Pile Type-44=No; Pile Type-45=No; Pile Type-46=No; Pile Type-47=No; Pile Type-48=No; Pile Type-49=No; Pile Type-50=No; Pile Type-51=No; Pile Type-52=No; Pile Type-53=No; Pile Type-54=No; Radius=450 mm  [stored 1.47638 ft]; Radius/2=225 mm  [stored 0.738189 ft]; band width=150 mm
- ATK_P9U_900_Diameter_Pile: ATK_1.25DIA_Circle_Radius=1125 mm; ATK_2.5_DIA_Circle_Radius=2250 mm; ATK_Pile_DIA=900 mm  [stored 2.95276 ft]; Band Width 2=215 mm; Band Width 3=90 mm; Depth=21000 mm  [stored 68.8976 ft]; Pile Type 01=No; Pile Type 02=No; Pile Type 03=No; Pile Type 04=No; Pile Type 05=No; Pile Type 06=No; Pile Type 07=No; Pile Type 08=No; Pile Type 09=Yes; Pile Type 10=Yes; Pile Type 11=No; Pile Type 12=No; Pile Type 13=No; Pile Type 14=No; Pile Type 15=No; Pile Type 16=No; Pile Type 17=No; Pile Type 18=No; Pile Type 19=No; Pile Type 20=No; Pile Type 21=No; Pile Type 22=No; Pile Type 23=No; Pile Type 24=No; Pile Type 25=No; Pile Type 26=No; Pile Type 27=No; Pile Type 28=No; Pile Type 29=No; Pile Type 30=No; Pile Type 31=Yes; Pile Type-32=No; Pile Type-33=No; Pile Type-34=No; Pile Type-35=No; Pile Type-36=No; Pile Type-37=Yes; Pile Type-38=No; Pile Type-39=No; Pile Type-40=No; Pile Type-41=No; Pile Type-42=No; Pile Type-43=No; Pile Type-44=No; Pile Type-45=No; Pile Type-46=No; Pile Type-47=No; Pile Type-48=No; Pile Type-49=No; Pile Type-50=No; Pile Type-51=No; Pile Type-52=No; Pile Type-53=No; Pile Type-54=No; Radius=450 mm  [stored 1.47638 ft]; Radius/2=225 mm  [stored 0.738189 ft]; band width=150 mm
- ATK_P8U_900_Diameter_Pile: ATK_1.25DIA_Circle_Radius=1125 mm; ATK_2.5_DIA_Circle_Radius=2250 mm; ATK_Pile_DIA=900 mm  [stored 2.95276 ft]; Band Width 2=215 mm; Band Width 3=90 mm; Depth=20000 mm  [stored 65.6168 ft]; Pile Type 01=No; Pile Type 02=No; Pile Type 03=No; Pile Type 04=No; Pile Type 05=No; Pile Type 06=No; Pile Type 07=No; Pile Type 08=Yes; Pile Type 09=Yes; Pile Type 10=No; Pile Type 11=No; Pile Type 12=No; Pile Type 13=No; Pile Type 14=No; Pile Type 15=No; Pile Type 16=No; Pile Type 17=No; Pile Type 18=No; Pile Type 19=No; Pile Type 20=No; Pile Type 21=No; Pile Type 22=No; Pile Type 23=No; Pile Type 24=No; Pile Type 25=No; Pile Type 26=No; Pile Type 27=No; Pile Type 28=No; Pile Type 29=No; Pile Type 30=No; Pile Type 31=Yes; Pile Type-32=No; Pile Type-33=No; Pile Type-34=No; Pile Type-35=No; Pile Type-36=No; Pile Type-37=Yes; Pile Type-38=No; Pile Type-39=No; Pile Type-40=No; Pile Type-41=No; Pile Type-42=No; Pile Type-43=No; Pile Type-44=No; Pile Type-45=No; Pile Type-46=No; Pile Type-47=No; Pile Type-48=No; Pile Type-49=No; Pile Type-50=No; Pile Type-51=No; Pile Type-52=No; Pile Type-53=No; Pile Type-54=No; Radius=450 mm  [stored 1.47638 ft]; Radius/2=225 mm  [stored 0.738189 ft]; band width=150 mm
- ATK_P7U_900_Diameter_Pile: ATK_1.25DIA_Circle_Radius=1125 mm; ATK_2.5_DIA_Circle_Radius=2250 mm; ATK_Pile_DIA=900 mm  [stored 2.95276 ft]; Band Width 2=215 mm; Band Width 3=90 mm; Depth=19000 mm; Pile Type 01=No; Pile Type 02=No; Pile Type 03=No; Pile Type 04=No; Pile Type 05=No; Pile Type 06=No; Pile Type 07=Yes; Pile Type 08=Yes; Pile Type 09=No; Pile Type 10=No; Pile Type 11=No; Pile Type 12=No; Pile Type 13=No; Pile Type 14=No; Pile Type 15=No; Pile Type 16=No; Pile Type 17=No; Pile Type 18=No; Pile Type 19=No; Pile Type 20=No; Pile Type 21=No; Pile Type 22=No; Pile Type 23=No; Pile Type 24=No; Pile Type 25=No; Pile Type 26=No; Pile Type 27=No; Pile Type 28=No; Pile Type 29=No; Pile Type 30=No; Pile Type 31=Yes; Pile Type-32=No; Pile Type-33=No; Pile Type-34=No; Pile Type-35=No; Pile Type-36=No; Pile Type-37=Yes; Pile Type-38=No; Pile Type-39=No; Pile Type-40=No; Pile Type-41=No; Pile Type-42=No; Pile Type-43=No; Pile Type-44=No; Pile Type-45=No; Pile Type-46=No; Pile Type-47=No; Pile Type-48=No; Pile Type-49=No; Pile Type-50=No; Pile Type-51=No; Pile Type-52=No; Pile Type-53=No; Pile Type-54=No; Radius=450 mm  [stored 1.47638 ft]; Radius/2=225 mm  [stored 0.738189 ft]; band width=150 mm
- ATK_P6U_900_Diameter_Pile: ATK_1.25DIA_Circle_Radius=1125 mm; ATK_2.5_DIA_Circle_Radius=2250 mm; ATK_Pile_DIA=900 mm  [stored 2.95276 ft]; Band Width 2=215 mm; Band Width 3=90 mm; Depth=18000 mm; Pile Type 01=No; Pile Type 02=No; Pile Type 03=No; Pile Type 04=No; Pile Type 05=No; Pile Type 06=Yes; Pile Type 07=Yes; Pile Type 08=No; Pile Type 09=No; Pile Type 10=No; Pile Type 11=No; Pile Type 12=No; Pile Type 13=No; Pile Type 14=No; Pile Type 15=No; Pile Type 16=No; Pile Type 17=No; Pile Type 18=No; Pile Type 19=No; Pile Type 20=No; Pile Type 21=No; Pile Type 22=No; Pile Type 23=No; Pile Type 24=No; Pile Type 25=No; Pile Type 26=No; Pile Type 27=No; Pile Type 28=No; Pile Type 29=No; Pile Type 30=No; Pile Type 31=Yes; Pile Type-32=No; Pile Type-33=No; Pile Type-34=No; Pile Type-35=No; Pile Type-36=No; Pile Type-37=Yes; Pile Type-38=No; Pile Type-39=No; Pile Type-40=No; Pile Type-41=No; Pile Type-42=No; Pile Type-43=No; Pile Type-44=No; Pile Type-45=No; Pile Type-46=No; Pile Type-47=No; Pile Type-48=No; Pile Type-49=No; Pile Type-50=No; Pile Type-51=No; Pile Type-52=No; Pile Type-53=No; Pile Type-54=No; Radius=450 mm  [stored 1.47638 ft]; Radius/2=225 mm  [stored 0.738189 ft]; band width=150 mm
- ATK_P5U_900_Diameter_Pile: ATK_1.25DIA_Circle_Radius=1125 mm; ATK_2.5_DIA_Circle_Radius=2250 mm; ATK_Pile_DIA=900 mm  [stored 2.95276 ft]; Band Width 2=215 mm; Band Width 3=90 mm; Depth=17000 mm; Pile Type 01=No; Pile Type 02=No; Pile Type 03=No; Pile Type 04=No; Pile Type 05=Yes; Pile Type 06=Yes; Pile Type 07=No; Pile Type 08=No; Pile Type 09=No; Pile Type 10=No; Pile Type 11=No; Pile Type 12=No; Pile Type 13=No; Pile Type 14=No; Pile Type 15=No; Pile Type 16=No; Pile Type 17=No; Pile Type 18=No; Pile Type 19=No; Pile Type 20=No; Pile Type 21=No; Pile Type 22=No; Pile Type 23=No; Pile Type 24=No; Pile Type 25=No; Pile Type 26=No; Pile Type 27=No; Pile Type 28=No; Pile Type 29=No; Pile Type 30=No; Pile Type 31=Yes; Pile Type-32=No; Pile Type-33=No; Pile Type-34=No; Pile Type-35=No; Pile Type-36=No; Pile Type-37=Yes; Pile Type-38=No; Pile Type-39=No; Pile Type-40=No; Pile Type-41=No; Pile Type-42=No; Pile Type-43=No; Pile Type-44=No; Pile Type-45=No; Pile Type-46=No; Pile Type-47=No; Pile Type-48=No; Pile Type-49=No; Pile Type-50=No; Pile Type-51=No; Pile Type-52=No; Pile Type-53=No; Pile Type-54=No; Radius=450 mm  [stored 1.47638 ft]; Radius/2=225 mm  [stored 0.738189 ft]; band width=150 mm
- ATK_P4U_900_Diameter_Pile: ATK_1.25DIA_Circle_Radius=1125 mm; ATK_2.5_DIA_Circle_Radius=2250 mm; ATK_Pile_DIA=900 mm  [stored 2.95276 ft]; Band Width 2=215 mm; Band Width 3=90 mm; Depth=16000 mm  [stored 52.4934 ft]; Pile Type 01=No; Pile Type 02=No; Pile Type 03=No; Pile Type 04=Yes; Pile Type 05=Yes; Pile Type 06=No; Pile Type 07=No; Pile Type 08=No; Pile Type 09=No; Pile Type 10=No; Pile Type 11=No; Pile Type 12=No; Pile Type 13=No; Pile Type 14=No; Pile Type 15=No; Pile Type 16=No; Pile Type 17=No; Pile Type 18=No; Pile Type 19=No; Pile Type 20=No; Pile Type 21=No; Pile Type 22=No; Pile Type 23=No; Pile Type 24=No; Pile Type 25=No; Pile Type 26=No; Pile Type 27=No; Pile Type 28=No; Pile Type 29=No; Pile Type 30=No; Pile Type 31=Yes; Pile Type-32=No; Pile Type-33=No; Pile Type-34=No; Pile Type-35=No; Pile Type-36=No; Pile Type-37=Yes; Pile Type-38=No; Pile Type-39=No; Pile Type-40=No; Pile Type-41=No; Pile Type-42=No; Pile Type-43=No; Pile Type-44=No; Pile Type-45=No; Pile Type-46=No; Pile Type-47=No; Pile Type-48=No; Pile Type-49=No; Pile Type-50=No; Pile Type-51=No; Pile Type-52=No; Pile Type-53=No; Pile Type-54=No; Radius=450 mm  [stored 1.47638 ft]; Radius/2=225 mm  [stored 0.738189 ft]; band width=150 mm
- ATK_P3U_900_Diameter_Pile: ATK_1.25DIA_Circle_Radius=1125 mm; ATK_2.5_DIA_Circle_Radius=2250 mm; ATK_Pile_DIA=900 mm  [stored 2.95276 ft]; Band Width 2=215 mm; Band Width 3=90 mm; Depth=15000 mm  [stored 49.2126 ft]; Pile Type 01=No; Pile Type 02=No; Pile Type 03=Yes; Pile Type 04=Yes; Pile Type 05=No; Pile Type 06=No; Pile Type 07=No; Pile Type 08=No; Pile Type 09=No; Pile Type 10=No; Pile Type 11=No; Pile Type 12=No; Pile Type 13=No; Pile Type 14=No; Pile Type 15=No; Pile Type 16=No; Pile Type 17=No; Pile Type 18=No; Pile Type 19=No; Pile Type 20=No; Pile Type 21=No; Pile Type 22=No; Pile Type 23=No; Pile Type 24=No; Pile Type 25=No; Pile Type 26=No; Pile Type 27=No; Pile Type 28=No; Pile Type 29=No; Pile Type 30=No; Pile Type 31=Yes; Pile Type-32=No; Pile Type-33=No; Pile Type-34=No; Pile Type-35=No; Pile Type-36=No; Pile Type-37=Yes; Pile Type-38=No; Pile Type-39=No; Pile Type-40=No; Pile Type-41=No; Pile Type-42=No; Pile Type-43=No; Pile Type-44=No; Pile Type-45=No; Pile Type-46=No; Pile Type-47=No; Pile Type-48=No; Pile Type-49=No; Pile Type-50=No; Pile Type-51=No; Pile Type-52=No; Pile Type-53=No; Pile Type-54=No; Radius=450 mm  [stored 1.47638 ft]; Radius/2=225 mm  [stored 0.738189 ft]; band width=150 mm
- ATK_P2U_900_Diameter_Pile: ATK_1.25DIA_Circle_Radius=1125 mm; ATK_2.5_DIA_Circle_Radius=2250 mm; ATK_Pile_DIA=900 mm  [stored 2.95276 ft]; Band Width 2=215 mm; Band Width 3=90 mm; Depth=14000 mm  [stored 45.9318 ft]; Pile Type 01=No; Pile Type 02=Yes; Pile Type 03=Yes; Pile Type 04=No; Pile Type 05=No; Pile Type 06=No; Pile Type 07=No; Pile Type 08=No; Pile Type 09=No; Pile Type 10=No; Pile Type 11=No; Pile Type 12=No; Pile Type 13=No; Pile Type 14=No; Pile Type 15=No; Pile Type 16=No; Pile Type 17=No; Pile Type 18=No; Pile Type 19=No; Pile Type 20=No; Pile Type 21=No; Pile Type 22=No; Pile Type 23=No; Pile Type 24=No; Pile Type 25=No; Pile Type 26=No; Pile Type 27=No; Pile Type 28=No; Pile Type 29=No; Pile Type 30=No; Pile Type 31=Yes; Pile Type-32=No; Pile Type-33=No; Pile Type-34=No; Pile Type-35=No; Pile Type-36=No; Pile Type-37=Yes; Pile Type-38=No; Pile Type-39=No; Pile Type-40=No; Pile Type-41=No; Pile Type-42=No; Pile Type-43=No; Pile Type-44=No; Pile Type-45=No; Pile Type-46=No; Pile Type-47=No; Pile Type-48=No; Pile Type-49=No; Pile Type-50=No; Pile Type-51=No; Pile Type-52=No; Pile Type-53=No; Pile Type-54=No; Radius=450 mm  [stored 1.47638 ft]; Radius/2=225 mm  [stored 0.738189 ft]; band width=150 mm
- ATK_P1U_900_Diameter_Pile: ATK_1.25DIA_Circle_Radius=1125 mm; ATK_2.5_DIA_Circle_Radius=2250 mm; ATK_Pile_DIA=900 mm  [stored 2.95276 ft]; Band Width 2=215 mm; Band Width 3=90 mm; Depth=13000 mm  [stored 42.6509 ft]; Pile Type 01=Yes; Pile Type 02=Yes; Pile Type 03=No; Pile Type 04=No; Pile Type 05=No; Pile Type 06=No; Pile Type 07=No; Pile Type 08=No; Pile Type 09=No; Pile Type 10=No; Pile Type 11=No; Pile Type 12=No; Pile Type 13=No; Pile Type 14=No; Pile Type 15=No; Pile Type 16=No; Pile Type 17=No; Pile Type 18=No; Pile Type 19=No; Pile Type 20=No; Pile Type 21=No; Pile Type 22=No; Pile Type 23=No; Pile Type 24=No; Pile Type 25=No; Pile Type 26=No; Pile Type 27=No; Pile Type 28=No; Pile Type 29=No; Pile Type 30=No; Pile Type 31=Yes; Pile Type-32=No; Pile Type-33=No; Pile Type-34=No; Pile Type-35=No; Pile Type-36=No; Pile Type-37=Yes; Pile Type-38=No; Pile Type-39=No; Pile Type-40=No; Pile Type-41=No; Pile Type-42=No; Pile Type-43=No; Pile Type-44=No; Pile Type-45=No; Pile Type-46=No; Pile Type-47=No; Pile Type-48=No; Pile Type-49=No; Pile Type-50=No; Pile Type-51=No; Pile Type-52=No; Pile Type-53=No; Pile Type-54=No; Radius=450 mm  [stored 1.47638 ft]; Radius/2=225 mm  [stored 0.738189 ft]; band width=150 mm
- ATK_P18O_750_Diameter_Pile: ATK_1.25DIA_Circle_Radius=938 mm; ATK_2.5_DIA_Circle_Radius=1875 mm  [stored 6.15157 ft]; ATK_Pile_DIA=750 mm  [stored 2.46063 ft]; Band Width 2=178 mm; Band Width 3=75 mm; Depth=30000 mm; Pile Type 01=No; Pile Type 02=No; Pile Type 03=No; Pile Type 04=No; Pile Type 05=No; Pile Type 06=No; Pile Type 07=No; Pile Type 08=No; Pile Type 09=No; Pile Type 10=No; Pile Type 11=No; Pile Type 12=No; Pile Type 13=No; Pile Type 14=No; Pile Type 15=No; Pile Type 16=No; Pile Type 17=No; Pile Type 18=Yes; Pile Type 19=No; Pile Type 20=No; Pile Type 21=No; Pile Type 22=No; Pile Type 23=No; Pile Type 24=No; Pile Type 25=No; Pile Type 26=No; Pile Type 27=No; Pile Type 28=No; Pile Type 29=No; Pile Type 30=No; Pile Type 31=Yes; Pile Type-32=No; Pile Type-33=No; Pile Type-34=No; Pile Type-35=No; Pile Type-36=No; Pile Type-37=Yes; Pile Type-38=No; Pile Type-39=No; Pile Type-40=No; Pile Type-41=No; Pile Type-42=No; Pile Type-43=No; Pile Type-44=No; Pile Type-45=No; Pile Type-46=No; Pile Type-47=No; Pile Type-48=No; Pile Type-49=No; Pile Type-50=No; Pile Type-51=No; Pile Type-52=No; Pile Type-53=No; Pile Type-54=No; Radius=375 mm  [stored 1.23031 ft]; Radius/2=188 mm; band width=125 mm  [stored 0.410105 ft]
- ATK_P17O_750_Diameter_Pile: ATK_1.25DIA_Circle_Radius=938 mm; ATK_2.5_DIA_Circle_Radius=1875 mm  [stored 6.15157 ft]; ATK_Pile_DIA=750 mm  [stored 2.46063 ft]; Band Width 2=178 mm; Band Width 3=75 mm; Depth=29000 mm; Pile Type 01=No; Pile Type 02=No; Pile Type 03=No; Pile Type 04=No; Pile Type 05=No; Pile Type 06=No; Pile Type 07=No; Pile Type 08=No; Pile Type 09=No; Pile Type 10=No; Pile Type 11=No; Pile Type 12=No; Pile Type 13=No; Pile Type 14=No; Pile Type 15=No; Pile Type 16=No; Pile Type 17=Yes; Pile Type 18=No; Pile Type 19=No; Pile Type 20=No; Pile Type 21=No; Pile Type 22=No; Pile Type 23=No; Pile Type 24=No; Pile Type 25=No; Pile Type 26=No; Pile Type 27=No; Pile Type 28=No; Pile Type 29=No; Pile Type 30=No; Pile Type 31=Yes; Pile Type-32=No; Pile Type-33=No; Pile Type-34=No; Pile Type-35=No; Pile Type-36=No; Pile Type-37=Yes; Pile Type-38=No; Pile Type-39=No; Pile Type-40=No; Pile Type-41=No; Pile Type-42=No; Pile Type-43=No; Pile Type-44=No; Pile Type-45=No; Pile Type-46=No; Pile Type-47=No; Pile Type-48=No; Pile Type-49=No; Pile Type-50=No; Pile Type-51=No; Pile Type-52=No; Pile Type-53=No; Pile Type-54=No; Radius=375 mm  [stored 1.23031 ft]; Radius/2=188 mm; band width=125 mm  [stored 0.410105 ft]
- ATK_P16O_750_Diameter_Pile 2: ATK_1.25DIA_Circle_Radius=938 mm; ATK_2.5_DIA_Circle_Radius=1875 mm  [stored 6.15157 ft]; ATK_Pile_DIA=750 mm  [stored 2.46063 ft]; Band Width 2=178 mm; Band Width 3=75 mm; Depth=28000 mm  [stored 91.8635 ft]; Pile Type 01=No; Pile Type 02=No; Pile Type 03=No; Pile Type 04=No; Pile Type 05=No; Pile Type 06=No; Pile Type 07=No; Pile Type 08=No; Pile Type 09=No; Pile Type 10=No; Pile Type 11=No; Pile Type 12=No; Pile Type 13=No; Pile Type 14=No; Pile Type 15=No; Pile Type 16=Yes; Pile Type 17=No; Pile Type 18=No; Pile Type 19=No; Pile Type 20=No; Pile Type 21=No; Pile Type 22=No; Pile Type 23=No; Pile Type 24=No; Pile Type 25=No; Pile Type 26=No; Pile Type 27=No; Pile Type 28=No; Pile Type 29=No; Pile Type 30=No; Pile Type 31=Yes; Pile Type-32=No; Pile Type-33=No; Pile Type-34=No; Pile Type-35=No; Pile Type-36=No; Pile Type-37=Yes; Pile Type-38=No; Pile Type-39=No; Pile Type-40=No; Pile Type-41=No; Pile Type-42=No; Pile Type-43=No; Pile Type-44=No; Pile Type-45=No; Pile Type-46=No; Pile Type-47=No; Pile Type-48=No; Pile Type-49=No; Pile Type-50=No; Pile Type-51=No; Pile Type-52=No; Pile Type-53=No; Pile Type-54=No; Radius=375 mm  [stored 1.23031 ft]; Radius/2=188 mm; band width=125 mm  [stored 0.410105 ft]
- ATK_P15O_750_Diameter_Pile: ATK_1.25DIA_Circle_Radius=938 mm; ATK_2.5_DIA_Circle_Radius=1875 mm  [stored 6.15157 ft]; ATK_Pile_DIA=750 mm  [stored 2.46063 ft]; Band Width 2=178 mm; Band Width 3=75 mm; Depth=27000 mm  [stored 88.5827 ft]; Pile Type 01=No; Pile Type 02=No; Pile Type 03=No; Pile Type 04=No; Pile Type 05=No; Pile Type 06=No; Pile Type 07=No; Pile Type 08=No; Pile Type 09=No; Pile Type 10=No; Pile Type 11=No; Pile Type 12=No; Pile Type 13=No; Pile Type 14=No; Pile Type 15=Yes; Pile Type 16=No; Pile Type 17=No; Pile Type 18=No; Pile Type 19=No; Pile Type 20=No; Pile Type 21=No; Pile Type 22=No; Pile Type 23=No; Pile Type 24=No; Pile Type 25=No; Pile Type 26=No; Pile Type 27=No; Pile Type 28=No; Pile Type 29=No; Pile Type 30=No; Pile Type 31=Yes; Pile Type-32=No; Pile Type-33=No; Pile Type-34=No; Pile Type-35=No; Pile Type-36=No; Pile Type-37=Yes; Pile Type-38=No; Pile Type-39=No; Pile Type-40=No; Pile Type-41=No; Pile Type-42=No; Pile Type-43=No; Pile Type-44=No; Pile Type-45=No; Pile Type-46=No; Pile Type-47=No; Pile Type-48=No; Pile Type-49=No; Pile Type-50=No; Pile Type-51=No; Pile Type-52=No; Pile Type-53=No; Pile Type-54=No; Radius=375 mm  [stored 1.23031 ft]; Radius/2=188 mm; band width=125 mm  [stored 0.410105 ft]
- ATK_P14O_750_Diameter_Pile: ATK_1.25DIA_Circle_Radius=938 mm; ATK_2.5_DIA_Circle_Radius=1875 mm  [stored 6.15157 ft]; ATK_Pile_DIA=750 mm  [stored 2.46063 ft]; Band Width 2=178 mm; Band Width 3=75 mm; Depth=26000 mm  [stored 85.3018 ft]; Pile Type 01=No; Pile Type 02=No; Pile Type 03=No; Pile Type 04=No; Pile Type 05=No; Pile Type 06=No; Pile Type 07=No; Pile Type 08=No; Pile Type 09=No; Pile Type 10=No; Pile Type 11=No; Pile Type 12=No; Pile Type 13=No; Pile Type 14=Yes; Pile Type 15=No; Pile Type 16=No; Pile Type 17=No; Pile Type 18=No; Pile Type 19=No; Pile Type 20=No; Pile Type 21=No; Pile Type 22=No; Pile Type 23=No; Pile Type 24=No; Pile Type 25=No; Pile Type 26=No; Pile Type 27=No; Pile Type 28=No; Pile Type 29=No; Pile Type 30=No; Pile Type 31=Yes; Pile Type-32=No; Pile Type-33=No; Pile Type-34=No; Pile Type-35=No; Pile Type-36=No; Pile Type-37=Yes; Pile Type-38=No; Pile Type-39=No; Pile Type-40=No; Pile Type-41=No; Pile Type-42=No; Pile Type-43=No; Pile Type-44=No; Pile Type-45=No; Pile Type-46=No; Pile Type-47=No; Pile Type-48=No; Pile Type-49=No; Pile Type-50=No; Pile Type-51=No; Pile Type-52=No; Pile Type-53=No; Pile Type-54=No; Radius=375 mm  [stored 1.23031 ft]; Radius/2=188 mm; band width=125 mm  [stored 0.410105 ft]
- ATK_P13O_750_Diameter_Pile: ATK_1.25DIA_Circle_Radius=938 mm; ATK_2.5_DIA_Circle_Radius=1875 mm  [stored 6.15157 ft]; ATK_Pile_DIA=750 mm  [stored 2.46063 ft]; Band Width 2=178 mm; Band Width 3=75 mm; Depth=25000 mm  [stored 82.021 ft]; Pile Type 01=No; Pile Type 02=No; Pile Type 03=No; Pile Type 04=No; Pile Type 05=No; Pile Type 06=No; Pile Type 07=No; Pile Type 08=No; Pile Type 09=No; Pile Type 10=No; Pile Type 11=No; Pile Type 12=No; Pile Type 13=Yes; Pile Type 14=No; Pile Type 15=No; Pile Type 16=No; Pile Type 17=No; Pile Type 18=No; Pile Type 19=No; Pile Type 20=No; Pile Type 21=No; Pile Type 22=No; Pile Type 23=No; Pile Type 24=No; Pile Type 25=No; Pile Type 26=No; Pile Type 27=No; Pile Type 28=No; Pile Type 29=No; Pile Type 30=No; Pile Type 31=Yes; Pile Type-32=No; Pile Type-33=No; Pile Type-34=No; Pile Type-35=No; Pile Type-36=No; Pile Type-37=Yes; Pile Type-38=No; Pile Type-39=No; Pile Type-40=No; Pile Type-41=No; Pile Type-42=No; Pile Type-43=No; Pile Type-44=No; Pile Type-45=No; Pile Type-46=No; Pile Type-47=No; Pile Type-48=No; Pile Type-49=No; Pile Type-50=No; Pile Type-51=No; Pile Type-52=No; Pile Type-53=No; Pile Type-54=No; Radius=375 mm  [stored 1.23031 ft]; Radius/2=188 mm; band width=125 mm  [stored 0.410105 ft]
- ATK_P12O_750_Diameter_Pile: ATK_1.25DIA_Circle_Radius=938 mm; ATK_2.5_DIA_Circle_Radius=1875 mm  [stored 6.15157 ft]; ATK_Pile_DIA=750 mm  [stored 2.46063 ft]; Band Width 2=178 mm; Band Width 3=75 mm; Depth=24000 mm  [stored 78.7402 ft]; Pile Type 01=No; Pile Type 02=No; Pile Type 03=No; Pile Type 04=No; Pile Type 05=No; Pile Type 06=No; Pile Type 07=No; Pile Type 08=No; Pile Type 09=No; Pile Type 10=No; Pile Type 11=No; Pile Type 12=Yes; Pile Type 13=No; Pile Type 14=No; Pile Type 15=No; Pile Type 16=No; Pile Type 17=No; Pile Type 18=No; Pile Type 19=No; Pile Type 20=No; Pile Type 21=No; Pile Type 22=No; Pile Type 23=No; Pile Type 24=No; Pile Type 25=No; Pile Type 26=No; Pile Type 27=No; Pile Type 28=No; Pile Type 29=No; Pile Type 30=No; Pile Type 31=Yes; Pile Type-32=No; Pile Type-33=No; Pile Type-34=No; Pile Type-35=No; Pile Type-36=No; Pile Type-37=Yes; Pile Type-38=No; Pile Type-39=No; Pile Type-40=No; Pile Type-41=No; Pile Type-42=No; Pile Type-43=No; Pile Type-44=No; Pile Type-45=No; Pile Type-46=No; Pile Type-47=No; Pile Type-48=No; Pile Type-49=No; Pile Type-50=No; Pile Type-51=No; Pile Type-52=No; Pile Type-53=No; Pile Type-54=No; Radius=375 mm  [stored 1.23031 ft]; Radius/2=188 mm; band width=125 mm  [stored 0.410105 ft]
- ATK_P11O_750_Diameter_Pile: ATK_1.25DIA_Circle_Radius=938 mm; ATK_2.5_DIA_Circle_Radius=1875 mm  [stored 6.15157 ft]; ATK_Pile_DIA=750 mm  [stored 2.46063 ft]; Band Width 2=178 mm; Band Width 3=75 mm; Depth=23000 mm  [stored 75.4593 ft]; Pile Type 01=No; Pile Type 02=No; Pile Type 03=No; Pile Type 04=No; Pile Type 05=No; Pile Type 06=No; Pile Type 07=No; Pile Type 08=No; Pile Type 09=No; Pile Type 10=No; Pile Type 11=Yes; Pile Type 12=No; Pile Type 13=No; Pile Type 14=No; Pile Type 15=No; Pile Type 16=No; Pile Type 17=No; Pile Type 18=No; Pile Type 19=No; Pile Type 20=No; Pile Type 21=No; Pile Type 22=No; Pile Type 23=No; Pile Type 24=No; Pile Type 25=No; Pile Type 26=No; Pile Type 27=No; Pile Type 28=No; Pile Type 29=No; Pile Type 30=No; Pile Type 31=Yes; Pile Type-32=No; Pile Type-33=No; Pile Type-34=No; Pile Type-35=No; Pile Type-36=No; Pile Type-37=Yes; Pile Type-38=No; Pile Type-39=No; Pile Type-40=No; Pile Type-41=No; Pile Type-42=No; Pile Type-43=No; Pile Type-44=No; Pile Type-45=No; Pile Type-46=No; Pile Type-47=No; Pile Type-48=No; Pile Type-49=No; Pile Type-50=No; Pile Type-51=No; Pile Type-52=No; Pile Type-53=No; Pile Type-54=No; Radius=375 mm  [stored 1.23031 ft]; Radius/2=188 mm; band width=125 mm  [stored 0.410105 ft]
- ATK_P10O_750_Diameter_Pile: ATK_1.25DIA_Circle_Radius=938 mm; ATK_2.5_DIA_Circle_Radius=1875 mm  [stored 6.15157 ft]; ATK_Pile_DIA=750 mm  [stored 2.46063 ft]; Band Width 2=178 mm; Band Width 3=75 mm; Depth=22000 mm  [stored 72.1785 ft]; Pile Type 01=No; Pile Type 02=No; Pile Type 03=No; Pile Type 04=No; Pile Type 05=No; Pile Type 06=No; Pile Type 07=No; Pile Type 08=No; Pile Type 09=No; Pile Type 10=Yes; Pile Type 11=No; Pile Type 12=No; Pile Type 13=No; Pile Type 14=No; Pile Type 15=No; Pile Type 16=No; Pile Type 17=No; Pile Type 18=No; Pile Type 19=No; Pile Type 20=No; Pile Type 21=No; Pile Type 22=No; Pile Type 23=No; Pile Type 24=No; Pile Type 25=No; Pile Type 26=No; Pile Type 27=No; Pile Type 28=No; Pile Type 29=No; Pile Type 30=No; Pile Type 31=Yes; Pile Type-32=No; Pile Type-33=No; Pile Type-34=No; Pile Type-35=No; Pile Type-36=No; Pile Type-37=Yes; Pile Type-38=No; Pile Type-39=No; Pile Type-40=No; Pile Type-41=No; Pile Type-42=No; Pile Type-43=No; Pile Type-44=No; Pile Type-45=No; Pile Type-46=No; Pile Type-47=No; Pile Type-48=No; Pile Type-49=No; Pile Type-50=No; Pile Type-51=No; Pile Type-52=No; Pile Type-53=No; Pile Type-54=No; Radius=375 mm  [stored 1.23031 ft]; Radius/2=188 mm; band width=125 mm  [stored 0.410105 ft]
- ATK_P9O_750_Diameter_Pile: ATK_1.25DIA_Circle_Radius=938 mm; ATK_2.5_DIA_Circle_Radius=1875 mm  [stored 6.15157 ft]; ATK_Pile_DIA=750 mm  [stored 2.46063 ft]; Band Width 2=178 mm; Band Width 3=75 mm; Depth=21000 mm  [stored 68.8976 ft]; Pile Type 01=No; Pile Type 02=No; Pile Type 03=No; Pile Type 04=No; Pile Type 05=No; Pile Type 06=No; Pile Type 07=No; Pile Type 08=No; Pile Type 09=Yes; Pile Type 10=No; Pile Type 11=No; Pile Type 12=No; Pile Type 13=No; Pile Type 14=No; Pile Type 15=No; Pile Type 16=No; Pile Type 17=No; Pile Type 18=No; Pile Type 19=No; Pile Type 20=No; Pile Type 21=No; Pile Type 22=No; Pile Type 23=No; Pile Type 24=No; Pile Type 25=No; Pile Type 26=No; Pile Type 27=No; Pile Type 28=No; Pile Type 29=No; Pile Type 30=No; Pile Type 31=Yes; Pile Type-32=No; Pile Type-33=No; Pile Type-34=No; Pile Type-35=No; Pile Type-36=No; Pile Type-37=Yes; Pile Type-38=No; Pile Type-39=No; Pile Type-40=No; Pile Type-41=No; Pile Type-42=No; Pile Type-43=No; Pile Type-44=No; Pile Type-45=No; Pile Type-46=No; Pile Type-47=No; Pile Type-48=No; Pile Type-49=No; Pile Type-50=No; Pile Type-51=No; Pile Type-52=No; Pile Type-53=No; Pile Type-54=No; Radius=375 mm  [stored 1.23031 ft]; Radius/2=188 mm; band width=125 mm  [stored 0.410105 ft]
- ATK_P8O_750_Diameter_Pile: ATK_1.25DIA_Circle_Radius=938 mm; ATK_2.5_DIA_Circle_Radius=1875 mm  [stored 6.15157 ft]; ATK_Pile_DIA=750 mm  [stored 2.46063 ft]; Band Width 2=178 mm; Band Width 3=75 mm; Depth=20000 mm  [stored 65.6168 ft]; Pile Type 01=No; Pile Type 02=No; Pile Type 03=No; Pile Type 04=No; Pile Type 05=No; Pile Type 06=No; Pile Type 07=No; Pile Type 08=Yes; Pile Type 09=No; Pile Type 10=No; Pile Type 11=No; Pile Type 12=No; Pile Type 13=No; Pile Type 14=No; Pile Type 15=No; Pile Type 16=No; Pile Type 17=No; Pile Type 18=No; Pile Type 19=No; Pile Type 20=No; Pile Type 21=No; Pile Type 22=No; Pile Type 23=No; Pile Type 24=No; Pile Type 25=No; Pile Type 26=No; Pile Type 27=No; Pile Type 28=No; Pile Type 29=No; Pile Type 30=No; Pile Type 31=Yes; Pile Type-32=No; Pile Type-33=No; Pile Type-34=No; Pile Type-35=No; Pile Type-36=No; Pile Type-37=Yes; Pile Type-38=No; Pile Type-39=No; Pile Type-40=No; Pile Type-41=No; Pile Type-42=No; Pile Type-43=No; Pile Type-44=No; Pile Type-45=No; Pile Type-46=No; Pile Type-47=No; Pile Type-48=No; Pile Type-49=No; Pile Type-50=No; Pile Type-51=No; Pile Type-52=No; Pile Type-53=No; Pile Type-54=No; Radius=375 mm  [stored 1.23031 ft]; Radius/2=188 mm; band width=125 mm  [stored 0.410105 ft]
- ATK_P7O_750_Diameter_Pile: ATK_1.25DIA_Circle_Radius=938 mm; ATK_2.5_DIA_Circle_Radius=1875 mm  [stored 6.15157 ft]; ATK_Pile_DIA=750 mm  [stored 2.46063 ft]; Band Width 2=178 mm; Band Width 3=75 mm; Depth=19000 mm; Pile Type 01=No; Pile Type 02=No; Pile Type 03=No; Pile Type 04=No; Pile Type 05=No; Pile Type 06=No; Pile Type 07=Yes; Pile Type 08=No; Pile Type 09=No; Pile Type 10=No; Pile Type 11=No; Pile Type 12=No; Pile Type 13=No; Pile Type 14=No; Pile Type 15=No; Pile Type 16=No; Pile Type 17=No; Pile Type 18=No; Pile Type 19=No; Pile Type 20=No; Pile Type 21=No; Pile Type 22=No; Pile Type 23=No; Pile Type 24=No; Pile Type 25=No; Pile Type 26=No; Pile Type 27=No; Pile Type 28=No; Pile Type 29=No; Pile Type 30=No; Pile Type 31=Yes; Pile Type-32=No; Pile Type-33=No; Pile Type-34=No; Pile Type-35=No; Pile Type-36=No; Pile Type-37=Yes; Pile Type-38=No; Pile Type-39=No; Pile Type-40=No; Pile Type-41=No; Pile Type-42=No; Pile Type-43=No; Pile Type-44=No; Pile Type-45=No; Pile Type-46=No; Pile Type-47=No; Pile Type-48=No; Pile Type-49=No; Pile Type-50=No; Pile Type-51=No; Pile Type-52=No; Pile Type-53=No; Pile Type-54=No; Radius=375 mm  [stored 1.23031 ft]; Radius/2=188 mm; band width=125 mm  [stored 0.410105 ft]
- ATK_P6O_750_Diameter_Pile: ATK_1.25DIA_Circle_Radius=938 mm; ATK_2.5_DIA_Circle_Radius=1875 mm  [stored 6.15157 ft]; ATK_Pile_DIA=750 mm  [stored 2.46063 ft]; Band Width 2=178 mm; Band Width 3=75 mm; Depth=18000 mm; Pile Type 01=No; Pile Type 02=No; Pile Type 03=No; Pile Type 04=No; Pile Type 05=No; Pile Type 06=Yes; Pile Type 07=No; Pile Type 08=No; Pile Type 09=No; Pile Type 10=No; Pile Type 11=No; Pile Type 12=No; Pile Type 13=No; Pile Type 14=No; Pile Type 15=No; Pile Type 16=No; Pile Type 17=No; Pile Type 18=No; Pile Type 19=No; Pile Type 20=No; Pile Type 21=No; Pile Type 22=No; Pile Type 23=No; Pile Type 24=No; Pile Type 25=No; Pile Type 26=No; Pile Type 27=No; Pile Type 28=No; Pile Type 29=No; Pile Type 30=No; Pile Type 31=Yes; Pile Type-32=No; Pile Type-33=No; Pile Type-34=No; Pile Type-35=No; Pile Type-36=No; Pile Type-37=Yes; Pile Type-38=No; Pile Type-39=No; Pile Type-40=No; Pile Type-41=No; Pile Type-42=No; Pile Type-43=No; Pile Type-44=No; Pile Type-45=No; Pile Type-46=No; Pile Type-47=No; Pile Type-48=No; Pile Type-49=No; Pile Type-50=No; Pile Type-51=No; Pile Type-52=No; Pile Type-53=No; Pile Type-54=No; Radius=375 mm  [stored 1.23031 ft]; Radius/2=188 mm; band width=125 mm  [stored 0.410105 ft]
- ATK_P5O_750_Diameter_Pile: ATK_1.25DIA_Circle_Radius=938 mm; ATK_2.5_DIA_Circle_Radius=1875 mm  [stored 6.15157 ft]; ATK_Pile_DIA=750 mm  [stored 2.46063 ft]; Band Width 2=178 mm; Band Width 3=75 mm; Depth=17000 mm; Pile Type 01=No; Pile Type 02=No; Pile Type 03=No; Pile Type 04=No; Pile Type 05=Yes; Pile Type 06=No; Pile Type 07=No; Pile Type 08=No; Pile Type 09=No; Pile Type 10=No; Pile Type 11=No; Pile Type 12=No; Pile Type 13=No; Pile Type 14=No; Pile Type 15=No; Pile Type 16=No; Pile Type 17=No; Pile Type 18=No; Pile Type 19=No; Pile Type 20=No; Pile Type 21=No; Pile Type 22=No; Pile Type 23=No; Pile Type 24=No; Pile Type 25=No; Pile Type 26=No; Pile Type 27=No; Pile Type 28=No; Pile Type 29=No; Pile Type 30=No; Pile Type 31=Yes; Pile Type-32=No; Pile Type-33=No; Pile Type-34=No; Pile Type-35=No; Pile Type-36=No; Pile Type-37=Yes; Pile Type-38=No; Pile Type-39=No; Pile Type-40=No; Pile Type-41=No; Pile Type-42=No; Pile Type-43=No; Pile Type-44=No; Pile Type-45=No; Pile Type-46=No; Pile Type-47=No; Pile Type-48=No; Pile Type-49=No; Pile Type-50=No; Pile Type-51=No; Pile Type-52=No; Pile Type-53=No; Pile Type-54=No; Radius=375 mm  [stored 1.23031 ft]; Radius/2=188 mm; band width=125 mm  [stored 0.410105 ft]
- ATK_P4O_750_Diameter_Pile: ATK_1.25DIA_Circle_Radius=938 mm; ATK_2.5_DIA_Circle_Radius=1875 mm  [stored 6.15157 ft]; ATK_Pile_DIA=750 mm  [stored 2.46063 ft]; Band Width 2=178 mm; Band Width 3=75 mm; Depth=16000 mm  [stored 52.4934 ft]; Pile Type 01=No; Pile Type 02=No; Pile Type 03=No; Pile Type 04=Yes; Pile Type 05=No; Pile Type 06=No; Pile Type 07=No; Pile Type 08=No; Pile Type 09=No; Pile Type 10=No; Pile Type 11=No; Pile Type 12=No; Pile Type 13=No; Pile Type 14=No; Pile Type 15=No; Pile Type 16=No; Pile Type 17=No; Pile Type 18=No; Pile Type 19=No; Pile Type 20=No; Pile Type 21=No; Pile Type 22=No; Pile Type 23=No; Pile Type 24=No; Pile Type 25=No; Pile Type 26=No; Pile Type 27=No; Pile Type 28=No; Pile Type 29=No; Pile Type 30=No; Pile Type 31=Yes; Pile Type-32=No; Pile Type-33=No; Pile Type-34=No; Pile Type-35=No; Pile Type-36=No; Pile Type-37=Yes; Pile Type-38=No; Pile Type-39=No; Pile Type-40=No; Pile Type-41=No; Pile Type-42=No; Pile Type-43=No; Pile Type-44=No; Pile Type-45=No; Pile Type-46=No; Pile Type-47=No; Pile Type-48=No; Pile Type-49=No; Pile Type-50=No; Pile Type-51=No; Pile Type-52=No; Pile Type-53=No; Pile Type-54=No; Radius=375 mm  [stored 1.23031 ft]; Radius/2=188 mm; band width=125 mm  [stored 0.410105 ft]
- ATK_P3O_750_Diameter_Pile: ATK_1.25DIA_Circle_Radius=938 mm; ATK_2.5_DIA_Circle_Radius=1875 mm  [stored 6.15157 ft]; ATK_Pile_DIA=750 mm  [stored 2.46063 ft]; Band Width 2=178 mm; Band Width 3=75 mm; Depth=15000 mm  [stored 49.2126 ft]; Pile Type 01=No; Pile Type 02=No; Pile Type 03=Yes; Pile Type 04=No; Pile Type 05=No; Pile Type 06=No; Pile Type 07=No; Pile Type 08=No; Pile Type 09=No; Pile Type 10=No; Pile Type 11=No; Pile Type 12=No; Pile Type 13=No; Pile Type 14=No; Pile Type 15=No; Pile Type 16=No; Pile Type 17=No; Pile Type 18=No; Pile Type 19=No; Pile Type 20=No; Pile Type 21=No; Pile Type 22=No; Pile Type 23=No; Pile Type 24=No; Pile Type 25=No; Pile Type 26=No; Pile Type 27=No; Pile Type 28=No; Pile Type 29=No; Pile Type 30=No; Pile Type 31=Yes; Pile Type-32=No; Pile Type-33=No; Pile Type-34=No; Pile Type-35=No; Pile Type-36=No; Pile Type-37=Yes; Pile Type-38=No; Pile Type-39=No; Pile Type-40=No; Pile Type-41=No; Pile Type-42=No; Pile Type-43=No; Pile Type-44=No; Pile Type-45=No; Pile Type-46=No; Pile Type-47=No; Pile Type-48=No; Pile Type-49=No; Pile Type-50=No; Pile Type-51=No; Pile Type-52=No; Pile Type-53=No; Pile Type-54=No; Radius=375 mm  [stored 1.23031 ft]; Radius/2=188 mm; band width=125 mm  [stored 0.410105 ft]
- ATK_P2O_750_Diameter_Pile: ATK_1.25DIA_Circle_Radius=938 mm; ATK_2.5_DIA_Circle_Radius=1875 mm  [stored 6.15157 ft]; ATK_Pile_DIA=750 mm  [stored 2.46063 ft]; Band Width 2=178 mm; Band Width 3=75 mm; Depth=14000 mm  [stored 45.9318 ft]; Pile Type 01=No; Pile Type 02=Yes; Pile Type 03=No; Pile Type 04=No; Pile Type 05=No; Pile Type 06=No; Pile Type 07=No; Pile Type 08=No; Pile Type 09=No; Pile Type 10=No; Pile Type 11=No; Pile Type 12=No; Pile Type 13=No; Pile Type 14=No; Pile Type 15=No; Pile Type 16=No; Pile Type 17=No; Pile Type 18=No; Pile Type 19=No; Pile Type 20=No; Pile Type 21=No; Pile Type 22=No; Pile Type 23=No; Pile Type 24=No; Pile Type 25=No; Pile Type 26=No; Pile Type 27=No; Pile Type 28=No; Pile Type 29=No; Pile Type 30=No; Pile Type 31=Yes; Pile Type-32=No; Pile Type-33=No; Pile Type-34=No; Pile Type-35=No; Pile Type-36=No; Pile Type-37=Yes; Pile Type-38=No; Pile Type-39=No; Pile Type-40=No; Pile Type-41=No; Pile Type-42=No; Pile Type-43=No; Pile Type-44=No; Pile Type-45=No; Pile Type-46=No; Pile Type-47=No; Pile Type-48=No; Pile Type-49=No; Pile Type-50=No; Pile Type-51=No; Pile Type-52=No; Pile Type-53=No; Pile Type-54=No; Radius=375 mm  [stored 1.23031 ft]; Radius/2=188 mm; band width=125 mm  [stored 0.410105 ft]
- ATK_P1O_750_Diameter_Pile: ATK_1.25DIA_Circle_Radius=938 mm; ATK_2.5_DIA_Circle_Radius=1875 mm  [stored 6.15157 ft]; ATK_Pile_DIA=750 mm  [stored 2.46063 ft]; Band Width 2=178 mm; Band Width 3=75 mm; Depth=13000 mm  [stored 42.6509 ft]; Pile Type 01=Yes; Pile Type 02=No; Pile Type 03=No; Pile Type 04=No; Pile Type 05=No; Pile Type 06=No; Pile Type 07=No; Pile Type 08=No; Pile Type 09=No; Pile Type 10=No; Pile Type 11=No; Pile Type 12=No; Pile Type 13=No; Pile Type 14=No; Pile Type 15=No; Pile Type 16=No; Pile Type 17=No; Pile Type 18=No; Pile Type 19=No; Pile Type 20=No; Pile Type 21=No; Pile Type 22=No; Pile Type 23=No; Pile Type 24=No; Pile Type 25=No; Pile Type 26=No; Pile Type 27=No; Pile Type 28=No; Pile Type 29=No; Pile Type 30=No; Pile Type 31=Yes; Pile Type-32=No; Pile Type-33=No; Pile Type-34=No; Pile Type-35=No; Pile Type-36=No; Pile Type-37=Yes; Pile Type-38=No; Pile Type-39=No; Pile Type-40=No; Pile Type-41=No; Pile Type-42=No; Pile Type-43=No; Pile Type-44=No; Pile Type-45=No; Pile Type-46=No; Pile Type-47=No; Pile Type-48=No; Pile Type-49=No; Pile Type-50=No; Pile Type-51=No; Pile Type-52=No; Pile Type-53=No; Pile Type-54=No; Radius=375 mm  [stored 1.23031 ft]; Radius/2=188 mm; band width=125 mm  [stored 0.410105 ft]
- ATK_P5U_900_Diameter: ATK_1.25DIA_Circle_Radius=1125 mm; ATK_2.5_DIA_Circle_Radius=2250 mm; ATK_Pile_DIA=900 mm  [stored 2.95276 ft]; Band Width 2=215 mm; Band Width 3=90 mm; Depth=17000 mm; Pile Type 01=No; Pile Type 02=No; Pile Type 03=No; Pile Type 04=No; Pile Type 05=Yes; Pile Type 06=Yes; Pile Type 07=No; Pile Type 08=No; Pile Type 09=No; Pile Type 10=No; Pile Type 11=No; Pile Type 12=No; Pile Type 13=No; Pile Type 14=No; Pile Type 15=No; Pile Type 16=No; Pile Type 17=No; Pile Type 18=No; Pile Type 19=No; Pile Type 20=No; Pile Type 21=No; Pile Type 22=No; Pile Type 23=No; Pile Type 24=No; Pile Type 25=No; Pile Type 26=No; Pile Type 27=No; Pile Type 28=No; Pile Type 29=No; Pile Type 30=No; Pile Type 31=Yes; Pile Type-32=No; Pile Type-33=No; Pile Type-34=No; Pile Type-35=No; Pile Type-36=No; Pile Type-37=Yes; Pile Type-38=No; Pile Type-39=No; Pile Type-40=No; Pile Type-41=No; Pile Type-42=No; Pile Type-43=No; Pile Type-44=No; Pile Type-45=No; Pile Type-46=No; Pile Type-47=No; Pile Type-48=No; Pile Type-49=No; Pile Type-50=No; Pile Type-51=No; Pile Type-52=No; Pile Type-53=No; Pile Type-54=No; Radius=450 mm  [stored 1.47638 ft]; Radius/2=225 mm  [stored 0.738189 ft]; band width=150 mm
- ATK_P2O_750_Diameter: ATK_1.25DIA_Circle_Radius=938 mm; ATK_2.5_DIA_Circle_Radius=1875 mm  [stored 6.15157 ft]; ATK_Pile_DIA=750 mm  [stored 2.46063 ft]; Band Width 2=178 mm; Band Width 3=75 mm; Depth=14000 mm  [stored 45.9318 ft]; Pile Type 01=No; Pile Type 02=Yes; Pile Type 03=No; Pile Type 04=No; Pile Type 05=No; Pile Type 06=No; Pile Type 07=No; Pile Type 08=No; Pile Type 09=No; Pile Type 10=No; Pile Type 11=No; Pile Type 12=No; Pile Type 13=No; Pile Type 14=No; Pile Type 15=No; Pile Type 16=No; Pile Type 17=No; Pile Type 18=No; Pile Type 19=No; Pile Type 20=No; Pile Type 21=No; Pile Type 22=No; Pile Type 23=No; Pile Type 24=No; Pile Type 25=No; Pile Type 26=No; Pile Type 27=No; Pile Type 28=No; Pile Type 29=No; Pile Type 30=No; Pile Type 31=Yes; Pile Type-32=No; Pile Type-33=No; Pile Type-34=No; Pile Type-35=No; Pile Type-36=No; Pile Type-37=Yes; Pile Type-38=No; Pile Type-39=No; Pile Type-40=No; Pile Type-41=No; Pile Type-42=No; Pile Type-43=No; Pile Type-44=No; Pile Type-45=No; Pile Type-46=No; Pile Type-47=No; Pile Type-48=No; Pile Type-49=No; Pile Type-50=No; Pile Type-51=No; Pile Type-52=No; Pile Type-53=No; Pile Type-54=No; Radius=375 mm  [stored 1.23031 ft]; Radius/2=188 mm; band width=125 mm  [stored 0.410105 ft]
- 1,3: ATK_1.25DIA_Circle_Radius=1250 mm  [stored 4.10105 ft]; ATK_2.5_DIA_Circle_Radius=2500 mm  [stored 8.2021 ft]; ATK_Pile_DIA=1000 mm  [stored 3.28084 ft]; Band Width 2=240 mm; Band Width 3=100 mm  [stored 0.328084 ft]; Depth=15000 mm  [stored 49.2126 ft]; Pile Type 01=No; Pile Type 02=No; Pile Type 03=No; Pile Type 04=Yes; Pile Type 05=Yes; Pile Type 06=No; Pile Type 07=No; Pile Type 08=No; Pile Type 09=No; Pile Type 10=No; Pile Type 11=No; Pile Type 12=No; Pile Type 13=No; Pile Type 14=No; Pile Type 15=No; Pile Type 16=No; Pile Type 17=No; Pile Type 18=No; Pile Type 19=No; Pile Type 20=No; Pile Type 21=No; Pile Type 22=No; Pile Type 23=No; Pile Type 24=No; Pile Type 25=No; Pile Type 26=No; Pile Type 27=No; Pile Type 28=No; Pile Type 29=No; Pile Type 30=No; Pile Type 31=No; Pile Type-32=No; Pile Type-33=No; Pile Type-34=No; Pile Type-35=No; Pile Type-36=No; Pile Type-37=No; Pile Type-38=No; Pile Type-39=No; Pile Type-40=No; Pile Type-41=No; Pile Type-42=No; Pile Type-43=No; Pile Type-44=No; Pile Type-45=No; Pile Type-46=No; Pile Type-47=No; Pile Type-48=No; Pile Type-49=No; Pile Type-50=No; Pile Type-51=No; Pile Type-52=No; Pile Type-53=No; Pile Type-54=No; Radius=500 mm  [stored 1.64042 ft]; Radius/2=250 mm  [stored 0.82021 ft]; band width=167 mm
- 1,2: ATK_1.25DIA_Circle_Radius=1250 mm  [stored 4.10105 ft]; ATK_2.5_DIA_Circle_Radius=2500 mm  [stored 8.2021 ft]; ATK_Pile_DIA=1000 mm  [stored 3.28084 ft]; Band Width 2=240 mm; Band Width 3=100 mm  [stored 0.328084 ft]; Depth=15000 mm  [stored 49.2126 ft]; Pile Type 01=Yes; Pile Type 02=Yes; Pile Type 03=No; Pile Type 04=No; Pile Type 05=No; Pile Type 06=No; Pile Type 07=No; Pile Type 08=No; Pile Type 09=No; Pile Type 10=No; Pile Type 11=No; Pile Type 12=No; Pile Type 13=No; Pile Type 14=No; Pile Type 15=No; Pile Type 16=No; Pile Type 17=No; Pile Type 18=No; Pile Type 19=No; Pile Type 20=No; Pile Type 21=No; Pile Type 22=No; Pile Type 23=No; Pile Type 24=No; Pile Type 25=No; Pile Type 26=No; Pile Type 27=No; Pile Type 28=No; Pile Type 29=No; Pile Type 30=No; Pile Type 31=No; Pile Type-32=No; Pile Type-33=No; Pile Type-34=No; Pile Type-35=No; Pile Type-36=No; Pile Type-37=No; Pile Type-38=No; Pile Type-39=No; Pile Type-40=No; Pile Type-41=No; Pile Type-42=No; Pile Type-43=No; Pile Type-44=No; Pile Type-45=No; Pile Type-46=No; Pile Type-47=No; Pile Type-48=No; Pile Type-49=No; Pile Type-50=No; Pile Type-51=No; Pile Type-52=No; Pile Type-53=No; Pile Type-54=No; Radius=500 mm  [stored 1.64042 ft]; Radius/2=250 mm  [stored 0.82021 ft]; band width=167 mm
- 54: ATK_1.25DIA_Circle_Radius=1250 mm  [stored 4.10105 ft]; ATK_2.5_DIA_Circle_Radius=2500 mm  [stored 8.2021 ft]; ATK_Pile_DIA=1000 mm  [stored 3.28084 ft]; Band Width 2=240 mm; Band Width 3=100 mm  [stored 0.328084 ft]; Depth=15000 mm  [stored 49.2126 ft]; Pile Type 01=No; Pile Type 02=No; Pile Type 03=No; Pile Type 04=No; Pile Type 05=No; Pile Type 06=No; Pile Type 07=No; Pile Type 08=No; Pile Type 09=No; Pile Type 10=No; Pile Type 11=No; Pile Type 12=No; Pile Type 13=No; Pile Type 14=No; Pile Type 15=No; Pile Type 16=No; Pile Type 17=No; Pile Type 18=No; Pile Type 19=No; Pile Type 20=No; Pile Type 21=No; Pile Type 22=No; Pile Type 23=No; Pile Type 24=No; Pile Type 25=No; Pile Type 26=No; Pile Type 27=No; Pile Type 28=No; Pile Type 29=No; Pile Type 30=No; Pile Type 31=No; Pile Type-32=No; Pile Type-33=No; Pile Type-34=No; Pile Type-35=No; Pile Type-36=No; Pile Type-37=No; Pile Type-38=No; Pile Type-39=No; Pile Type-40=No; Pile Type-41=No; Pile Type-42=No; Pile Type-43=No; Pile Type-44=No; Pile Type-45=No; Pile Type-46=No; Pile Type-47=No; Pile Type-48=No; Pile Type-49=No; Pile Type-50=No; Pile Type-51=No; Pile Type-52=No; Pile Type-53=No; Pile Type-54=Yes; Radius=500 mm  [stored 1.64042 ft]; Radius/2=250 mm  [stored 0.82021 ft]; band width=167 mm
- 53: ATK_1.25DIA_Circle_Radius=1250 mm  [stored 4.10105 ft]; ATK_2.5_DIA_Circle_Radius=2500 mm  [stored 8.2021 ft]; ATK_Pile_DIA=1000 mm  [stored 3.28084 ft]; Band Width 2=240 mm; Band Width 3=100 mm  [stored 0.328084 ft]; Depth=15000 mm  [stored 49.2126 ft]; Pile Type 01=No; Pile Type 02=No; Pile Type 03=No; Pile Type 04=No; Pile Type 05=No; Pile Type 06=No; Pile Type 07=No; Pile Type 08=No; Pile Type 09=No; Pile Type 10=No; Pile Type 11=No; Pile Type 12=No; Pile Type 13=No; Pile Type 14=No; Pile Type 15=No; Pile Type 16=No; Pile Type 17=No; Pile Type 18=No; Pile Type 19=No; Pile Type 20=No; Pile Type 21=No; Pile Type 22=No; Pile Type 23=No; Pile Type 24=No; Pile Type 25=No; Pile Type 26=No; Pile Type 27=No; Pile Type 28=No; Pile Type 29=No; Pile Type 30=No; Pile Type 31=No; Pile Type-32=No; Pile Type-33=No; Pile Type-34=No; Pile Type-35=No; Pile Type-36=No; Pile Type-37=No; Pile Type-38=No; Pile Type-39=No; Pile Type-40=No; Pile Type-41=No; Pile Type-42=No; Pile Type-43=No; Pile Type-44=No; Pile Type-45=No; Pile Type-46=No; Pile Type-47=No; Pile Type-48=No; Pile Type-49=No; Pile Type-50=No; Pile Type-51=No; Pile Type-52=No; Pile Type-53=Yes; Pile Type-54=No; Radius=500 mm  [stored 1.64042 ft]; Radius/2=250 mm  [stored 0.82021 ft]; band width=167 mm
- 52: ATK_1.25DIA_Circle_Radius=1250 mm  [stored 4.10105 ft]; ATK_2.5_DIA_Circle_Radius=2500 mm  [stored 8.2021 ft]; ATK_Pile_DIA=1000 mm  [stored 3.28084 ft]; Band Width 2=240 mm; Band Width 3=100 mm  [stored 0.328084 ft]; Depth=15000 mm  [stored 49.2126 ft]; Pile Type 01=No; Pile Type 02=No; Pile Type 03=No; Pile Type 04=No; Pile Type 05=No; Pile Type 06=No; Pile Type 07=No; Pile Type 08=No; Pile Type 09=No; Pile Type 10=No; Pile Type 11=No; Pile Type 12=No; Pile Type 13=No; Pile Type 14=No; Pile Type 15=No; Pile Type 16=No; Pile Type 17=No; Pile Type 18=No; Pile Type 19=No; Pile Type 20=No; Pile Type 21=No; Pile Type 22=No; Pile Type 23=No; Pile Type 24=No; Pile Type 25=No; Pile Type 26=No; Pile Type 27=No; Pile Type 28=No; Pile Type 29=No; Pile Type 30=No; Pile Type 31=No; Pile Type-32=No; Pile Type-33=No; Pile Type-34=No; Pile Type-35=No; Pile Type-36=No; Pile Type-37=No; Pile Type-38=No; Pile Type-39=No; Pile Type-40=No; Pile Type-41=No; Pile Type-42=No; Pile Type-43=No; Pile Type-44=No; Pile Type-45=No; Pile Type-46=No; Pile Type-47=No; Pile Type-48=No; Pile Type-49=No; Pile Type-50=No; Pile Type-51=No; Pile Type-52=Yes; Pile Type-53=No; Pile Type-54=No; Radius=500 mm  [stored 1.64042 ft]; Radius/2=250 mm  [stored 0.82021 ft]; band width=167 mm
- 51: ATK_1.25DIA_Circle_Radius=1250 mm  [stored 4.10105 ft]; ATK_2.5_DIA_Circle_Radius=2500 mm  [stored 8.2021 ft]; ATK_Pile_DIA=1000 mm  [stored 3.28084 ft]; Band Width 2=240 mm; Band Width 3=100 mm  [stored 0.328084 ft]; Depth=15000 mm  [stored 49.2126 ft]; Pile Type 01=No; Pile Type 02=No; Pile Type 03=No; Pile Type 04=No; Pile Type 05=No; Pile Type 06=No; Pile Type 07=No; Pile Type 08=No; Pile Type 09=No; Pile Type 10=No; Pile Type 11=No; Pile Type 12=No; Pile Type 13=No; Pile Type 14=No; Pile Type 15=No; Pile Type 16=No; Pile Type 17=No; Pile Type 18=No; Pile Type 19=No; Pile Type 20=No; Pile Type 21=No; Pile Type 22=No; Pile Type 23=No; Pile Type 24=No; Pile Type 25=No; Pile Type 26=No; Pile Type 27=No; Pile Type 28=No; Pile Type 29=No; Pile Type 30=No; Pile Type 31=No; Pile Type-32=No; Pile Type-33=No; Pile Type-34=No; Pile Type-35=No; Pile Type-36=No; Pile Type-37=No; Pile Type-38=No; Pile Type-39=No; Pile Type-40=No; Pile Type-41=No; Pile Type-42=No; Pile Type-43=No; Pile Type-44=No; Pile Type-45=No; Pile Type-46=No; Pile Type-47=No; Pile Type-48=No; Pile Type-49=No; Pile Type-50=No; Pile Type-51=Yes; Pile Type-52=No; Pile Type-53=No; Pile Type-54=No; Radius=500 mm  [stored 1.64042 ft]; Radius/2=250 mm  [stored 0.82021 ft]; band width=167 mm
- 50: ATK_1.25DIA_Circle_Radius=1250 mm  [stored 4.10105 ft]; ATK_2.5_DIA_Circle_Radius=2500 mm  [stored 8.2021 ft]; ATK_Pile_DIA=1000 mm  [stored 3.28084 ft]; Band Width 2=240 mm; Band Width 3=100 mm  [stored 0.328084 ft]; Depth=15000 mm  [stored 49.2126 ft]; Pile Type 01=No; Pile Type 02=No; Pile Type 03=No; Pile Type 04=No; Pile Type 05=No; Pile Type 06=No; Pile Type 07=No; Pile Type 08=No; Pile Type 09=No; Pile Type 10=No; Pile Type 11=No; Pile Type 12=No; Pile Type 13=No; Pile Type 14=No; Pile Type 15=No; Pile Type 16=No; Pile Type 17=No; Pile Type 18=No; Pile Type 19=No; Pile Type 20=No; Pile Type 21=No; Pile Type 22=No; Pile Type 23=No; Pile Type 24=No; Pile Type 25=No; Pile Type 26=No; Pile Type 27=No; Pile Type 28=No; Pile Type 29=No; Pile Type 30=No; Pile Type 31=No; Pile Type-32=No; Pile Type-33=No; Pile Type-34=No; Pile Type-35=No; Pile Type-36=No; Pile Type-37=No; Pile Type-38=No; Pile Type-39=No; Pile Type-40=No; Pile Type-41=No; Pile Type-42=No; Pile Type-43=No; Pile Type-44=No; Pile Type-45=No; Pile Type-46=No; Pile Type-47=No; Pile Type-48=No; Pile Type-49=No; Pile Type-50=Yes; Pile Type-51=No; Pile Type-52=No; Pile Type-53=No; Pile Type-54=No; Radius=500 mm  [stored 1.64042 ft]; Radius/2=250 mm  [stored 0.82021 ft]; band width=167 mm
- 49: ATK_1.25DIA_Circle_Radius=1250 mm  [stored 4.10105 ft]; ATK_2.5_DIA_Circle_Radius=2500 mm  [stored 8.2021 ft]; ATK_Pile_DIA=1000 mm  [stored 3.28084 ft]; Band Width 2=240 mm; Band Width 3=100 mm  [stored 0.328084 ft]; Depth=15000 mm  [stored 49.2126 ft]; Pile Type 01=No; Pile Type 02=No; Pile Type 03=No; Pile Type 04=No; Pile Type 05=No; Pile Type 06=No; Pile Type 07=No; Pile Type 08=No; Pile Type 09=No; Pile Type 10=No; Pile Type 11=No; Pile Type 12=No; Pile Type 13=No; Pile Type 14=No; Pile Type 15=No; Pile Type 16=No; Pile Type 17=No; Pile Type 18=No; Pile Type 19=No; Pile Type 20=No; Pile Type 21=No; Pile Type 22=No; Pile Type 23=No; Pile Type 24=No; Pile Type 25=No; Pile Type 26=No; Pile Type 27=No; Pile Type 28=No; Pile Type 29=No; Pile Type 30=No; Pile Type 31=No; Pile Type-32=No; Pile Type-33=No; Pile Type-34=No; Pile Type-35=No; Pile Type-36=No; Pile Type-37=No; Pile Type-38=No; Pile Type-39=No; Pile Type-40=No; Pile Type-41=No; Pile Type-42=No; Pile Type-43=No; Pile Type-44=No; Pile Type-45=No; Pile Type-46=No; Pile Type-47=No; Pile Type-48=No; Pile Type-49=Yes; Pile Type-50=No; Pile Type-51=No; Pile Type-52=No; Pile Type-53=No; Pile Type-54=No; Radius=500 mm  [stored 1.64042 ft]; Radius/2=250 mm  [stored 0.82021 ft]; band width=167 mm
- 48: ATK_1.25DIA_Circle_Radius=1250 mm  [stored 4.10105 ft]; ATK_2.5_DIA_Circle_Radius=2500 mm  [stored 8.2021 ft]; ATK_Pile_DIA=1000 mm  [stored 3.28084 ft]; Band Width 2=240 mm; Band Width 3=100 mm  [stored 0.328084 ft]; Depth=15000 mm  [stored 49.2126 ft]; Pile Type 01=No; Pile Type 02=No; Pile Type 03=No; Pile Type 04=No; Pile Type 05=No; Pile Type 06=No; Pile Type 07=No; Pile Type 08=No; Pile Type 09=No; Pile Type 10=No; Pile Type 11=No; Pile Type 12=No; Pile Type 13=No; Pile Type 14=No; Pile Type 15=No; Pile Type 16=No; Pile Type 17=No; Pile Type 18=No; Pile Type 19=No; Pile Type 20=No; Pile Type 21=No; Pile Type 22=No; Pile Type 23=No; Pile Type 24=No; Pile Type 25=No; Pile Type 26=No; Pile Type 27=No; Pile Type 28=No; Pile Type 29=No; Pile Type 30=No; Pile Type 31=No; Pile Type-32=No; Pile Type-33=No; Pile Type-34=No; Pile Type-35=No; Pile Type-36=No; Pile Type-37=No; Pile Type-38=No; Pile Type-39=No; Pile Type-40=No; Pile Type-41=No; Pile Type-42=No; Pile Type-43=No; Pile Type-44=No; Pile Type-45=No; Pile Type-46=No; Pile Type-47=No; Pile Type-48=Yes; Pile Type-49=No; Pile Type-50=No; Pile Type-51=No; Pile Type-52=No; Pile Type-53=No; Pile Type-54=No; Radius=500 mm  [stored 1.64042 ft]; Radius/2=250 mm  [stored 0.82021 ft]; band width=167 mm
- 47: ATK_1.25DIA_Circle_Radius=1250 mm  [stored 4.10105 ft]; ATK_2.5_DIA_Circle_Radius=2500 mm  [stored 8.2021 ft]; ATK_Pile_DIA=1000 mm  [stored 3.28084 ft]; Band Width 2=240 mm; Band Width 3=100 mm  [stored 0.328084 ft]; Depth=15000 mm  [stored 49.2126 ft]; Pile Type 01=No; Pile Type 02=No; Pile Type 03=No; Pile Type 04=No; Pile Type 05=No; Pile Type 06=No; Pile Type 07=No; Pile Type 08=No; Pile Type 09=No; Pile Type 10=No; Pile Type 11=No; Pile Type 12=No; Pile Type 13=No; Pile Type 14=No; Pile Type 15=No; Pile Type 16=No; Pile Type 17=No; Pile Type 18=No; Pile Type 19=No; Pile Type 20=No; Pile Type 21=No; Pile Type 22=No; Pile Type 23=No; Pile Type 24=No; Pile Type 25=No; Pile Type 26=No; Pile Type 27=No; Pile Type 28=No; Pile Type 29=No; Pile Type 30=No; Pile Type 31=No; Pile Type-32=No; Pile Type-33=No; Pile Type-34=No; Pile Type-35=No; Pile Type-36=No; Pile Type-37=No; Pile Type-38=No; Pile Type-39=No; Pile Type-40=No; Pile Type-41=No; Pile Type-42=No; Pile Type-43=No; Pile Type-44=No; Pile Type-45=No; Pile Type-46=No; Pile Type-47=Yes; Pile Type-48=No; Pile Type-49=No; Pile Type-50=No; Pile Type-51=No; Pile Type-52=No; Pile Type-53=No; Pile Type-54=No; Radius=500 mm  [stored 1.64042 ft]; Radius/2=250 mm  [stored 0.82021 ft]; band width=167 mm
- 46: ATK_1.25DIA_Circle_Radius=1250 mm  [stored 4.10105 ft]; ATK_2.5_DIA_Circle_Radius=2500 mm  [stored 8.2021 ft]; ATK_Pile_DIA=1000 mm  [stored 3.28084 ft]; Band Width 2=240 mm; Band Width 3=100 mm  [stored 0.328084 ft]; Depth=15000 mm  [stored 49.2126 ft]; Pile Type 01=No; Pile Type 02=No; Pile Type 03=No; Pile Type 04=No; Pile Type 05=No; Pile Type 06=No; Pile Type 07=No; Pile Type 08=No; Pile Type 09=No; Pile Type 10=No; Pile Type 11=No; Pile Type 12=No; Pile Type 13=No; Pile Type 14=No; Pile Type 15=No; Pile Type 16=No; Pile Type 17=No; Pile Type 18=No; Pile Type 19=No; Pile Type 20=No; Pile Type 21=No; Pile Type 22=No; Pile Type 23=No; Pile Type 24=No; Pile Type 25=No; Pile Type 26=No; Pile Type 27=No; Pile Type 28=No; Pile Type 29=No; Pile Type 30=No; Pile Type 31=No; Pile Type-32=No; Pile Type-33=No; Pile Type-34=No; Pile Type-35=No; Pile Type-36=No; Pile Type-37=No; Pile Type-38=No; Pile Type-39=No; Pile Type-40=No; Pile Type-41=No; Pile Type-42=No; Pile Type-43=No; Pile Type-44=No; Pile Type-45=No; Pile Type-46=Yes; Pile Type-47=No; Pile Type-48=No; Pile Type-49=No; Pile Type-50=No; Pile Type-51=No; Pile Type-52=No; Pile Type-53=No; Pile Type-54=No; Radius=500 mm  [stored 1.64042 ft]; Radius/2=250 mm  [stored 0.82021 ft]; band width=167 mm
- 45: ATK_1.25DIA_Circle_Radius=1250 mm  [stored 4.10105 ft]; ATK_2.5_DIA_Circle_Radius=2500 mm  [stored 8.2021 ft]; ATK_Pile_DIA=1000 mm  [stored 3.28084 ft]; Band Width 2=240 mm; Band Width 3=100 mm  [stored 0.328084 ft]; Depth=15000 mm  [stored 49.2126 ft]; Pile Type 01=No; Pile Type 02=No; Pile Type 03=No; Pile Type 04=No; Pile Type 05=No; Pile Type 06=No; Pile Type 07=No; Pile Type 08=No; Pile Type 09=No; Pile Type 10=No; Pile Type 11=No; Pile Type 12=No; Pile Type 13=No; Pile Type 14=No; Pile Type 15=No; Pile Type 16=No; Pile Type 17=No; Pile Type 18=No; Pile Type 19=No; Pile Type 20=No; Pile Type 21=No; Pile Type 22=No; Pile Type 23=No; Pile Type 24=No; Pile Type 25=No; Pile Type 26=No; Pile Type 27=No; Pile Type 28=No; Pile Type 29=No; Pile Type 30=No; Pile Type 31=No; Pile Type-32=No; Pile Type-33=No; Pile Type-34=No; Pile Type-35=No; Pile Type-36=No; Pile Type-37=No; Pile Type-38=No; Pile Type-39=No; Pile Type-40=No; Pile Type-41=No; Pile Type-42=No; Pile Type-43=No; Pile Type-44=No; Pile Type-45=Yes; Pile Type-46=No; Pile Type-47=No; Pile Type-48=No; Pile Type-49=No; Pile Type-50=No; Pile Type-51=No; Pile Type-52=No; Pile Type-53=No; Pile Type-54=No; Radius=500 mm  [stored 1.64042 ft]; Radius/2=250 mm  [stored 0.82021 ft]; band width=167 mm
- 44: ATK_1.25DIA_Circle_Radius=1250 mm  [stored 4.10105 ft]; ATK_2.5_DIA_Circle_Radius=2500 mm  [stored 8.2021 ft]; ATK_Pile_DIA=1000 mm  [stored 3.28084 ft]; Band Width 2=240 mm; Band Width 3=100 mm  [stored 0.328084 ft]; Depth=15000 mm  [stored 49.2126 ft]; Pile Type 01=No; Pile Type 02=No; Pile Type 03=No; Pile Type 04=No; Pile Type 05=No; Pile Type 06=No; Pile Type 07=No; Pile Type 08=No; Pile Type 09=No; Pile Type 10=No; Pile Type 11=No; Pile Type 12=No; Pile Type 13=No; Pile Type 14=No; Pile Type 15=No; Pile Type 16=No; Pile Type 17=No; Pile Type 18=No; Pile Type 19=No; Pile Type 20=No; Pile Type 21=No; Pile Type 22=No; Pile Type 23=No; Pile Type 24=No; Pile Type 25=No; Pile Type 26=No; Pile Type 27=No; Pile Type 28=No; Pile Type 29=No; Pile Type 30=No; Pile Type 31=No; Pile Type-32=No; Pile Type-33=No; Pile Type-34=No; Pile Type-35=No; Pile Type-36=No; Pile Type-37=No; Pile Type-38=No; Pile Type-39=No; Pile Type-40=No; Pile Type-41=No; Pile Type-42=No; Pile Type-43=No; Pile Type-44=Yes; Pile Type-45=No; Pile Type-46=No; Pile Type-47=No; Pile Type-48=No; Pile Type-49=No; Pile Type-50=No; Pile Type-51=No; Pile Type-52=No; Pile Type-53=No; Pile Type-54=No; Radius=500 mm  [stored 1.64042 ft]; Radius/2=250 mm  [stored 0.82021 ft]; band width=167 mm
- 43: ATK_1.25DIA_Circle_Radius=1250 mm  [stored 4.10105 ft]; ATK_2.5_DIA_Circle_Radius=2500 mm  [stored 8.2021 ft]; ATK_Pile_DIA=1000 mm  [stored 3.28084 ft]; Band Width 2=240 mm; Band Width 3=100 mm  [stored 0.328084 ft]; Depth=15000 mm  [stored 49.2126 ft]; Pile Type 01=No; Pile Type 02=No; Pile Type 03=No; Pile Type 04=No; Pile Type 05=No; Pile Type 06=No; Pile Type 07=No; Pile Type 08=No; Pile Type 09=No; Pile Type 10=No; Pile Type 11=No; Pile Type 12=No; Pile Type 13=No; Pile Type 14=No; Pile Type 15=No; Pile Type 16=No; Pile Type 17=No; Pile Type 18=No; Pile Type 19=No; Pile Type 20=No; Pile Type 21=No; Pile Type 22=No; Pile Type 23=No; Pile Type 24=No; Pile Type 25=No; Pile Type 26=No; Pile Type 27=No; Pile Type 28=No; Pile Type 29=No; Pile Type 30=No; Pile Type 31=No; Pile Type-32=No; Pile Type-33=No; Pile Type-34=No; Pile Type-35=No; Pile Type-36=No; Pile Type-37=No; Pile Type-38=No; Pile Type-39=No; Pile Type-40=No; Pile Type-41=No; Pile Type-42=No; Pile Type-43=Yes; Pile Type-44=No; Pile Type-45=No; Pile Type-46=No; Pile Type-47=No; Pile Type-48=No; Pile Type-49=No; Pile Type-50=No; Pile Type-51=No; Pile Type-52=No; Pile Type-53=No; Pile Type-54=No; Radius=500 mm  [stored 1.64042 ft]; Radius/2=250 mm  [stored 0.82021 ft]; band width=167 mm
- 42: ATK_1.25DIA_Circle_Radius=1250 mm  [stored 4.10105 ft]; ATK_2.5_DIA_Circle_Radius=2500 mm  [stored 8.2021 ft]; ATK_Pile_DIA=1000 mm  [stored 3.28084 ft]; Band Width 2=240 mm; Band Width 3=100 mm  [stored 0.328084 ft]; Depth=15000 mm  [stored 49.2126 ft]; Pile Type 01=No; Pile Type 02=No; Pile Type 03=No; Pile Type 04=No; Pile Type 05=No; Pile Type 06=No; Pile Type 07=No; Pile Type 08=No; Pile Type 09=No; Pile Type 10=No; Pile Type 11=No; Pile Type 12=No; Pile Type 13=No; Pile Type 14=No; Pile Type 15=No; Pile Type 16=No; Pile Type 17=No; Pile Type 18=No; Pile Type 19=No; Pile Type 20=No; Pile Type 21=No; Pile Type 22=No; Pile Type 23=No; Pile Type 24=No; Pile Type 25=No; Pile Type 26=No; Pile Type 27=No; Pile Type 28=No; Pile Type 29=No; Pile Type 30=No; Pile Type 31=No; Pile Type-32=No; Pile Type-33=No; Pile Type-34=No; Pile Type-35=No; Pile Type-36=No; Pile Type-37=No; Pile Type-38=No; Pile Type-39=No; Pile Type-40=No; Pile Type-41=No; Pile Type-42=Yes; Pile Type-43=No; Pile Type-44=No; Pile Type-45=No; Pile Type-46=No; Pile Type-47=No; Pile Type-48=No; Pile Type-49=No; Pile Type-50=No; Pile Type-51=No; Pile Type-52=No; Pile Type-53=No; Pile Type-54=No; Radius=500 mm  [stored 1.64042 ft]; Radius/2=250 mm  [stored 0.82021 ft]; band width=167 mm
- 41: ATK_1.25DIA_Circle_Radius=1250 mm  [stored 4.10105 ft]; ATK_2.5_DIA_Circle_Radius=2500 mm  [stored 8.2021 ft]; ATK_Pile_DIA=1000 mm  [stored 3.28084 ft]; Band Width 2=240 mm; Band Width 3=100 mm  [stored 0.328084 ft]; Depth=15000 mm  [stored 49.2126 ft]; Pile Type 01=No; Pile Type 02=No; Pile Type 03=No; Pile Type 04=No; Pile Type 05=No; Pile Type 06=No; Pile Type 07=No; Pile Type 08=No; Pile Type 09=No; Pile Type 10=No; Pile Type 11=No; Pile Type 12=No; Pile Type 13=No; Pile Type 14=No; Pile Type 15=No; Pile Type 16=No; Pile Type 17=No; Pile Type 18=No; Pile Type 19=No; Pile Type 20=No; Pile Type 21=No; Pile Type 22=No; Pile Type 23=No; Pile Type 24=No; Pile Type 25=No; Pile Type 26=No; Pile Type 27=No; Pile Type 28=No; Pile Type 29=No; Pile Type 30=No; Pile Type 31=No; Pile Type-32=No; Pile Type-33=No; Pile Type-34=No; Pile Type-35=No; Pile Type-36=No; Pile Type-37=No; Pile Type-38=No; Pile Type-39=No; Pile Type-40=No; Pile Type-41=Yes; Pile Type-42=No; Pile Type-43=No; Pile Type-44=No; Pile Type-45=No; Pile Type-46=No; Pile Type-47=No; Pile Type-48=No; Pile Type-49=No; Pile Type-50=No; Pile Type-51=No; Pile Type-52=No; Pile Type-53=No; Pile Type-54=No; Radius=500 mm  [stored 1.64042 ft]; Radius/2=250 mm  [stored 0.82021 ft]; band width=167 mm
- 40: ATK_1.25DIA_Circle_Radius=1250 mm  [stored 4.10105 ft]; ATK_2.5_DIA_Circle_Radius=2500 mm  [stored 8.2021 ft]; ATK_Pile_DIA=1000 mm  [stored 3.28084 ft]; Band Width 2=240 mm; Band Width 3=100 mm  [stored 0.328084 ft]; Depth=15000 mm  [stored 49.2126 ft]; Pile Type 01=No; Pile Type 02=No; Pile Type 03=No; Pile Type 04=No; Pile Type 05=No; Pile Type 06=No; Pile Type 07=No; Pile Type 08=No; Pile Type 09=No; Pile Type 10=No; Pile Type 11=No; Pile Type 12=No; Pile Type 13=No; Pile Type 14=No; Pile Type 15=No; Pile Type 16=No; Pile Type 17=No; Pile Type 18=No; Pile Type 19=No; Pile Type 20=No; Pile Type 21=No; Pile Type 22=No; Pile Type 23=No; Pile Type 24=No; Pile Type 25=No; Pile Type 26=No; Pile Type 27=No; Pile Type 28=No; Pile Type 29=No; Pile Type 30=No; Pile Type 31=No; Pile Type-32=No; Pile Type-33=No; Pile Type-34=No; Pile Type-35=No; Pile Type-36=No; Pile Type-37=No; Pile Type-38=No; Pile Type-39=No; Pile Type-40=Yes; Pile Type-41=No; Pile Type-42=No; Pile Type-43=No; Pile Type-44=No; Pile Type-45=No; Pile Type-46=No; Pile Type-47=No; Pile Type-48=No; Pile Type-49=No; Pile Type-50=No; Pile Type-51=No; Pile Type-52=No; Pile Type-53=No; Pile Type-54=No; Radius=500 mm  [stored 1.64042 ft]; Radius/2=250 mm  [stored 0.82021 ft]; band width=167 mm
- 39: ATK_1.25DIA_Circle_Radius=1250 mm  [stored 4.10105 ft]; ATK_2.5_DIA_Circle_Radius=2500 mm  [stored 8.2021 ft]; ATK_Pile_DIA=1000 mm  [stored 3.28084 ft]; Band Width 2=240 mm; Band Width 3=100 mm  [stored 0.328084 ft]; Depth=15000 mm  [stored 49.2126 ft]; Pile Type 01=No; Pile Type 02=No; Pile Type 03=No; Pile Type 04=No; Pile Type 05=No; Pile Type 06=No; Pile Type 07=No; Pile Type 08=No; Pile Type 09=No; Pile Type 10=No; Pile Type 11=No; Pile Type 12=No; Pile Type 13=No; Pile Type 14=No; Pile Type 15=No; Pile Type 16=No; Pile Type 17=No; Pile Type 18=No; Pile Type 19=No; Pile Type 20=No; Pile Type 21=No; Pile Type 22=No; Pile Type 23=No; Pile Type 24=No; Pile Type 25=No; Pile Type 26=No; Pile Type 27=No; Pile Type 28=No; Pile Type 29=No; Pile Type 30=No; Pile Type 31=No; Pile Type-32=No; Pile Type-33=No; Pile Type-34=No; Pile Type-35=No; Pile Type-36=No; Pile Type-37=No; Pile Type-38=No; Pile Type-39=Yes; Pile Type-40=No; Pile Type-41=No; Pile Type-42=No; Pile Type-43=No; Pile Type-44=No; Pile Type-45=No; Pile Type-46=No; Pile Type-47=No; Pile Type-48=No; Pile Type-49=No; Pile Type-50=No; Pile Type-51=No; Pile Type-52=No; Pile Type-53=No; Pile Type-54=No; Radius=500 mm  [stored 1.64042 ft]; Radius/2=250 mm  [stored 0.82021 ft]; band width=167 mm
- 38: ATK_1.25DIA_Circle_Radius=1250 mm  [stored 4.10105 ft]; ATK_2.5_DIA_Circle_Radius=2500 mm  [stored 8.2021 ft]; ATK_Pile_DIA=1000 mm  [stored 3.28084 ft]; Band Width 2=240 mm; Band Width 3=100 mm  [stored 0.328084 ft]; Depth=15000 mm  [stored 49.2126 ft]; Pile Type 01=No; Pile Type 02=No; Pile Type 03=No; Pile Type 04=No; Pile Type 05=No; Pile Type 06=No; Pile Type 07=No; Pile Type 08=No; Pile Type 09=No; Pile Type 10=No; Pile Type 11=No; Pile Type 12=No; Pile Type 13=No; Pile Type 14=No; Pile Type 15=No; Pile Type 16=No; Pile Type 17=No; Pile Type 18=No; Pile Type 19=No; Pile Type 20=No; Pile Type 21=No; Pile Type 22=No; Pile Type 23=No; Pile Type 24=No; Pile Type 25=No; Pile Type 26=No; Pile Type 27=No; Pile Type 28=No; Pile Type 29=No; Pile Type 30=No; Pile Type 31=No; Pile Type-32=No; Pile Type-33=No; Pile Type-34=No; Pile Type-35=No; Pile Type-36=No; Pile Type-37=No; Pile Type-38=Yes; Pile Type-39=No; Pile Type-40=No; Pile Type-41=No; Pile Type-42=No; Pile Type-43=No; Pile Type-44=No; Pile Type-45=No; Pile Type-46=No; Pile Type-47=No; Pile Type-48=No; Pile Type-49=No; Pile Type-50=No; Pile Type-51=No; Pile Type-52=No; Pile Type-53=No; Pile Type-54=No; Radius=500 mm  [stored 1.64042 ft]; Radius/2=250 mm  [stored 0.82021 ft]; band width=167 mm
- 37: ATK_1.25DIA_Circle_Radius=1250 mm  [stored 4.10105 ft]; ATK_2.5_DIA_Circle_Radius=2500 mm  [stored 8.2021 ft]; ATK_Pile_DIA=1000 mm  [stored 3.28084 ft]; Band Width 2=240 mm; Band Width 3=100 mm  [stored 0.328084 ft]; Depth=15000 mm  [stored 49.2126 ft]; Pile Type 01=No; Pile Type 02=No; Pile Type 03=No; Pile Type 04=No; Pile Type 05=No; Pile Type 06=No; Pile Type 07=No; Pile Type 08=No; Pile Type 09=No; Pile Type 10=No; Pile Type 11=No; Pile Type 12=No; Pile Type 13=No; Pile Type 14=No; Pile Type 15=No; Pile Type 16=No; Pile Type 17=No; Pile Type 18=No; Pile Type 19=No; Pile Type 20=No; Pile Type 21=No; Pile Type 22=No; Pile Type 23=No; Pile Type 24=No; Pile Type 25=No; Pile Type 26=No; Pile Type 27=No; Pile Type 28=No; Pile Type 29=No; Pile Type 30=No; Pile Type 31=No; Pile Type-32=No; Pile Type-33=No; Pile Type-34=No; Pile Type-35=No; Pile Type-36=No; Pile Type-37=Yes; Pile Type-38=No; Pile Type-39=No; Pile Type-40=No; Pile Type-41=No; Pile Type-42=No; Pile Type-43=No; Pile Type-44=No; Pile Type-45=No; Pile Type-46=No; Pile Type-47=No; Pile Type-48=No; Pile Type-49=No; Pile Type-50=No; Pile Type-51=No; Pile Type-52=No; Pile Type-53=No; Pile Type-54=No; Radius=500 mm  [stored 1.64042 ft]; Radius/2=250 mm  [stored 0.82021 ft]; band width=167 mm
- 36: ATK_1.25DIA_Circle_Radius=1250 mm  [stored 4.10105 ft]; ATK_2.5_DIA_Circle_Radius=2500 mm  [stored 8.2021 ft]; ATK_Pile_DIA=1000 mm  [stored 3.28084 ft]; Band Width 2=240 mm; Band Width 3=100 mm  [stored 0.328084 ft]; Depth=15000 mm  [stored 49.2126 ft]; Pile Type 01=No; Pile Type 02=No; Pile Type 03=No; Pile Type 04=No; Pile Type 05=No; Pile Type 06=No; Pile Type 07=No; Pile Type 08=No; Pile Type 09=No; Pile Type 10=No; Pile Type 11=No; Pile Type 12=No; Pile Type 13=No; Pile Type 14=No; Pile Type 15=No; Pile Type 16=No; Pile Type 17=No; Pile Type 18=No; Pile Type 19=No; Pile Type 20=No; Pile Type 21=No; Pile Type 22=No; Pile Type 23=No; Pile Type 24=No; Pile Type 25=No; Pile Type 26=No; Pile Type 27=No; Pile Type 28=No; Pile Type 29=No; Pile Type 30=No; Pile Type 31=No; Pile Type-32=No; Pile Type-33=No; Pile Type-34=No; Pile Type-35=No; Pile Type-36=Yes; Pile Type-37=No; Pile Type-38=No; Pile Type-39=No; Pile Type-40=No; Pile Type-41=No; Pile Type-42=No; Pile Type-43=No; Pile Type-44=No; Pile Type-45=No; Pile Type-46=No; Pile Type-47=No; Pile Type-48=No; Pile Type-49=No; Pile Type-50=No; Pile Type-51=No; Pile Type-52=No; Pile Type-53=No; Pile Type-54=No; Radius=500 mm  [stored 1.64042 ft]; Radius/2=250 mm  [stored 0.82021 ft]; band width=167 mm
- 35: ATK_1.25DIA_Circle_Radius=1250 mm  [stored 4.10105 ft]; ATK_2.5_DIA_Circle_Radius=2500 mm  [stored 8.2021 ft]; ATK_Pile_DIA=1000 mm  [stored 3.28084 ft]; Band Width 2=240 mm; Band Width 3=100 mm  [stored 0.328084 ft]; Depth=15000 mm  [stored 49.2126 ft]; Pile Type 01=No; Pile Type 02=No; Pile Type 03=No; Pile Type 04=No; Pile Type 05=No; Pile Type 06=No; Pile Type 07=No; Pile Type 08=No; Pile Type 09=No; Pile Type 10=No; Pile Type 11=No; Pile Type 12=No; Pile Type 13=No; Pile Type 14=No; Pile Type 15=No; Pile Type 16=No; Pile Type 17=No; Pile Type 18=No; Pile Type 19=No; Pile Type 20=No; Pile Type 21=No; Pile Type 22=No; Pile Type 23=No; Pile Type 24=No; Pile Type 25=No; Pile Type 26=No; Pile Type 27=No; Pile Type 28=No; Pile Type 29=No; Pile Type 30=No; Pile Type 31=No; Pile Type-32=No; Pile Type-33=No; Pile Type-34=No; Pile Type-35=Yes; Pile Type-36=No; Pile Type-37=No; Pile Type-38=No; Pile Type-39=No; Pile Type-40=No; Pile Type-41=No; Pile Type-42=No; Pile Type-43=No; Pile Type-44=No; Pile Type-45=No; Pile Type-46=No; Pile Type-47=No; Pile Type-48=No; Pile Type-49=No; Pile Type-50=No; Pile Type-51=No; Pile Type-52=No; Pile Type-53=No; Pile Type-54=No; Radius=500 mm  [stored 1.64042 ft]; Radius/2=250 mm  [stored 0.82021 ft]; band width=167 mm
- 34: ATK_1.25DIA_Circle_Radius=1250 mm  [stored 4.10105 ft]; ATK_2.5_DIA_Circle_Radius=2500 mm  [stored 8.2021 ft]; ATK_Pile_DIA=1000 mm  [stored 3.28084 ft]; Band Width 2=240 mm; Band Width 3=100 mm  [stored 0.328084 ft]; Depth=15000 mm  [stored 49.2126 ft]; Pile Type 01=No; Pile Type 02=No; Pile Type 03=No; Pile Type 04=No; Pile Type 05=No; Pile Type 06=No; Pile Type 07=No; Pile Type 08=No; Pile Type 09=No; Pile Type 10=No; Pile Type 11=No; Pile Type 12=No; Pile Type 13=No; Pile Type 14=No; Pile Type 15=No; Pile Type 16=No; Pile Type 17=No; Pile Type 18=No; Pile Type 19=No; Pile Type 20=No; Pile Type 21=No; Pile Type 22=No; Pile Type 23=No; Pile Type 24=No; Pile Type 25=No; Pile Type 26=No; Pile Type 27=No; Pile Type 28=No; Pile Type 29=No; Pile Type 30=No; Pile Type 31=No; Pile Type-32=No; Pile Type-33=No; Pile Type-34=Yes; Pile Type-35=No; Pile Type-36=No; Pile Type-37=No; Pile Type-38=No; Pile Type-39=No; Pile Type-40=No; Pile Type-41=No; Pile Type-42=No; Pile Type-43=No; Pile Type-44=No; Pile Type-45=No; Pile Type-46=No; Pile Type-47=No; Pile Type-48=No; Pile Type-49=No; Pile Type-50=No; Pile Type-51=No; Pile Type-52=No; Pile Type-53=No; Pile Type-54=No; Radius=500 mm  [stored 1.64042 ft]; Radius/2=250 mm  [stored 0.82021 ft]; band width=167 mm
- 33: ATK_1.25DIA_Circle_Radius=1250 mm  [stored 4.10105 ft]; ATK_2.5_DIA_Circle_Radius=2500 mm  [stored 8.2021 ft]; ATK_Pile_DIA=1000 mm  [stored 3.28084 ft]; Band Width 2=240 mm; Band Width 3=100 mm  [stored 0.328084 ft]; Depth=15000 mm  [stored 49.2126 ft]; Pile Type 01=No; Pile Type 02=No; Pile Type 03=No; Pile Type 04=No; Pile Type 05=No; Pile Type 06=No; Pile Type 07=No; Pile Type 08=No; Pile Type 09=No; Pile Type 10=No; Pile Type 11=No; Pile Type 12=No; Pile Type 13=No; Pile Type 14=No; Pile Type 15=No; Pile Type 16=No; Pile Type 17=No; Pile Type 18=No; Pile Type 19=No; Pile Type 20=No; Pile Type 21=No; Pile Type 22=No; Pile Type 23=No; Pile Type 24=No; Pile Type 25=No; Pile Type 26=No; Pile Type 27=No; Pile Type 28=No; Pile Type 29=No; Pile Type 30=No; Pile Type 31=No; Pile Type-32=No; Pile Type-33=Yes; Pile Type-34=No; Pile Type-35=No; Pile Type-36=No; Pile Type-37=No; Pile Type-38=No; Pile Type-39=No; Pile Type-40=No; Pile Type-41=No; Pile Type-42=No; Pile Type-43=No; Pile Type-44=No; Pile Type-45=No; Pile Type-46=No; Pile Type-47=No; Pile Type-48=No; Pile Type-49=No; Pile Type-50=No; Pile Type-51=No; Pile Type-52=No; Pile Type-53=No; Pile Type-54=No; Radius=500 mm  [stored 1.64042 ft]; Radius/2=250 mm  [stored 0.82021 ft]; band width=167 mm
- 32: ATK_1.25DIA_Circle_Radius=1250 mm  [stored 4.10105 ft]; ATK_2.5_DIA_Circle_Radius=2500 mm  [stored 8.2021 ft]; ATK_Pile_DIA=1000 mm  [stored 3.28084 ft]; Band Width 2=240 mm; Band Width 3=100 mm  [stored 0.328084 ft]; Depth=15000 mm  [stored 49.2126 ft]; Pile Type 01=No; Pile Type 02=No; Pile Type 03=No; Pile Type 04=No; Pile Type 05=No; Pile Type 06=No; Pile Type 07=No; Pile Type 08=No; Pile Type 09=No; Pile Type 10=No; Pile Type 11=No; Pile Type 12=No; Pile Type 13=No; Pile Type 14=No; Pile Type 15=No; Pile Type 16=No; Pile Type 17=No; Pile Type 18=No; Pile Type 19=No; Pile Type 20=No; Pile Type 21=No; Pile Type 22=No; Pile Type 23=No; Pile Type 24=No; Pile Type 25=No; Pile Type 26=No; Pile Type 27=No; Pile Type 28=No; Pile Type 29=No; Pile Type 30=No; Pile Type 31=No; Pile Type-32=Yes; Pile Type-33=No; Pile Type-34=No; Pile Type-35=No; Pile Type-36=No; Pile Type-37=No; Pile Type-38=No; Pile Type-39=No; Pile Type-40=No; Pile Type-41=No; Pile Type-42=No; Pile Type-43=No; Pile Type-44=No; Pile Type-45=No; Pile Type-46=No; Pile Type-47=No; Pile Type-48=No; Pile Type-49=No; Pile Type-50=No; Pile Type-51=No; Pile Type-52=No; Pile Type-53=No; Pile Type-54=No; Radius=500 mm  [stored 1.64042 ft]; Radius/2=250 mm  [stored 0.82021 ft]; band width=167 mm
- 31: ATK_1.25DIA_Circle_Radius=1250 mm  [stored 4.10105 ft]; ATK_2.5_DIA_Circle_Radius=2500 mm  [stored 8.2021 ft]; ATK_Pile_DIA=1000 mm  [stored 3.28084 ft]; Band Width 2=240 mm; Band Width 3=100 mm  [stored 0.328084 ft]; Depth=15000 mm  [stored 49.2126 ft]; Pile Type 01=No; Pile Type 02=No; Pile Type 03=No; Pile Type 04=No; Pile Type 05=No; Pile Type 06=No; Pile Type 07=No; Pile Type 08=No; Pile Type 09=No; Pile Type 10=No; Pile Type 11=No; Pile Type 12=No; Pile Type 13=No; Pile Type 14=No; Pile Type 15=No; Pile Type 16=No; Pile Type 17=No; Pile Type 18=No; Pile Type 19=No; Pile Type 20=No; Pile Type 21=No; Pile Type 22=No; Pile Type 23=No; Pile Type 24=No; Pile Type 25=No; Pile Type 26=No; Pile Type 27=No; Pile Type 28=No; Pile Type 29=No; Pile Type 30=No; Pile Type 31=Yes; Pile Type-32=No; Pile Type-33=No; Pile Type-34=No; Pile Type-35=No; Pile Type-36=No; Pile Type-37=No; Pile Type-38=No; Pile Type-39=No; Pile Type-40=No; Pile Type-41=No; Pile Type-42=No; Pile Type-43=No; Pile Type-44=No; Pile Type-45=No; Pile Type-46=No; Pile Type-47=No; Pile Type-48=No; Pile Type-49=No; Pile Type-50=No; Pile Type-51=No; Pile Type-52=No; Pile Type-53=No; Pile Type-54=No; Radius=500 mm  [stored 1.64042 ft]; Radius/2=250 mm  [stored 0.82021 ft]; band width=167 mm
- 30: ATK_1.25DIA_Circle_Radius=1250 mm  [stored 4.10105 ft]; ATK_2.5_DIA_Circle_Radius=2500 mm  [stored 8.2021 ft]; ATK_Pile_DIA=1000 mm  [stored 3.28084 ft]; Band Width 2=240 mm; Band Width 3=100 mm  [stored 0.328084 ft]; Depth=15000 mm  [stored 49.2126 ft]; Pile Type 01=No; Pile Type 02=No; Pile Type 03=No; Pile Type 04=No; Pile Type 05=No; Pile Type 06=No; Pile Type 07=No; Pile Type 08=No; Pile Type 09=No; Pile Type 10=No; Pile Type 11=No; Pile Type 12=No; Pile Type 13=No; Pile Type 14=No; Pile Type 15=No; Pile Type 16=No; Pile Type 17=No; Pile Type 18=No; Pile Type 19=No; Pile Type 20=No; Pile Type 21=No; Pile Type 22=No; Pile Type 23=No; Pile Type 24=No; Pile Type 25=No; Pile Type 26=No; Pile Type 27=No; Pile Type 28=No; Pile Type 29=No; Pile Type 30=Yes; Pile Type 31=No; Pile Type-32=No; Pile Type-33=No; Pile Type-34=No; Pile Type-35=No; Pile Type-36=No; Pile Type-37=No; Pile Type-38=No; Pile Type-39=No; Pile Type-40=No; Pile Type-41=No; Pile Type-42=No; Pile Type-43=No; Pile Type-44=No; Pile Type-45=No; Pile Type-46=No; Pile Type-47=No; Pile Type-48=No; Pile Type-49=No; Pile Type-50=No; Pile Type-51=No; Pile Type-52=No; Pile Type-53=No; Pile Type-54=No; Radius=500 mm  [stored 1.64042 ft]; Radius/2=250 mm  [stored 0.82021 ft]; band width=167 mm
- 29: ATK_1.25DIA_Circle_Radius=1250 mm  [stored 4.10105 ft]; ATK_2.5_DIA_Circle_Radius=2500 mm  [stored 8.2021 ft]; ATK_Pile_DIA=1000 mm  [stored 3.28084 ft]; Band Width 2=240 mm; Band Width 3=100 mm  [stored 0.328084 ft]; Depth=15000 mm  [stored 49.2126 ft]; Pile Type 01=No; Pile Type 02=No; Pile Type 03=No; Pile Type 04=No; Pile Type 05=No; Pile Type 06=No; Pile Type 07=No; Pile Type 08=No; Pile Type 09=No; Pile Type 10=No; Pile Type 11=No; Pile Type 12=No; Pile Type 13=No; Pile Type 14=No; Pile Type 15=No; Pile Type 16=No; Pile Type 17=No; Pile Type 18=No; Pile Type 19=No; Pile Type 20=No; Pile Type 21=No; Pile Type 22=No; Pile Type 23=No; Pile Type 24=No; Pile Type 25=No; Pile Type 26=No; Pile Type 27=No; Pile Type 28=No; Pile Type 29=Yes; Pile Type 30=No; Pile Type 31=No; Pile Type-32=No; Pile Type-33=No; Pile Type-34=No; Pile Type-35=No; Pile Type-36=No; Pile Type-37=No; Pile Type-38=No; Pile Type-39=No; Pile Type-40=No; Pile Type-41=No; Pile Type-42=No; Pile Type-43=No; Pile Type-44=No; Pile Type-45=No; Pile Type-46=No; Pile Type-47=No; Pile Type-48=No; Pile Type-49=No; Pile Type-50=No; Pile Type-51=No; Pile Type-52=No; Pile Type-53=No; Pile Type-54=No; Radius=500 mm  [stored 1.64042 ft]; Radius/2=250 mm  [stored 0.82021 ft]; band width=167 mm
- 28: ATK_1.25DIA_Circle_Radius=1250 mm  [stored 4.10105 ft]; ATK_2.5_DIA_Circle_Radius=2500 mm  [stored 8.2021 ft]; ATK_Pile_DIA=1000 mm  [stored 3.28084 ft]; Band Width 2=240 mm; Band Width 3=100 mm  [stored 0.328084 ft]; Depth=15000 mm  [stored 49.2126 ft]; Pile Type 01=No; Pile Type 02=No; Pile Type 03=No; Pile Type 04=No; Pile Type 05=No; Pile Type 06=No; Pile Type 07=No; Pile Type 08=No; Pile Type 09=No; Pile Type 10=No; Pile Type 11=No; Pile Type 12=No; Pile Type 13=No; Pile Type 14=No; Pile Type 15=No; Pile Type 16=No; Pile Type 17=No; Pile Type 18=No; Pile Type 19=No; Pile Type 20=No; Pile Type 21=No; Pile Type 22=No; Pile Type 23=No; Pile Type 24=No; Pile Type 25=No; Pile Type 26=No; Pile Type 27=No; Pile Type 28=Yes; Pile Type 29=No; Pile Type 30=No; Pile Type 31=No; Pile Type-32=No; Pile Type-33=No; Pile Type-34=No; Pile Type-35=No; Pile Type-36=No; Pile Type-37=No; Pile Type-38=No; Pile Type-39=No; Pile Type-40=No; Pile Type-41=No; Pile Type-42=No; Pile Type-43=No; Pile Type-44=No; Pile Type-45=No; Pile Type-46=No; Pile Type-47=No; Pile Type-48=No; Pile Type-49=No; Pile Type-50=No; Pile Type-51=No; Pile Type-52=No; Pile Type-53=No; Pile Type-54=No; Radius=500 mm  [stored 1.64042 ft]; Radius/2=250 mm  [stored 0.82021 ft]; band width=167 mm
- 27: ATK_1.25DIA_Circle_Radius=1250 mm  [stored 4.10105 ft]; ATK_2.5_DIA_Circle_Radius=2500 mm  [stored 8.2021 ft]; ATK_Pile_DIA=1000 mm  [stored 3.28084 ft]; Band Width 2=240 mm; Band Width 3=100 mm  [stored 0.328084 ft]; Depth=15000 mm  [stored 49.2126 ft]; Pile Type 01=No; Pile Type 02=No; Pile Type 03=No; Pile Type 04=No; Pile Type 05=No; Pile Type 06=No; Pile Type 07=No; Pile Type 08=No; Pile Type 09=No; Pile Type 10=No; Pile Type 11=No; Pile Type 12=No; Pile Type 13=No; Pile Type 14=No; Pile Type 15=No; Pile Type 16=No; Pile Type 17=No; Pile Type 18=No; Pile Type 19=No; Pile Type 20=No; Pile Type 21=No; Pile Type 22=No; Pile Type 23=No; Pile Type 24=No; Pile Type 25=No; Pile Type 26=No; Pile Type 27=Yes; Pile Type 28=No; Pile Type 29=No; Pile Type 30=No; Pile Type 31=No; Pile Type-32=No; Pile Type-33=No; Pile Type-34=No; Pile Type-35=No; Pile Type-36=No; Pile Type-37=No; Pile Type-38=No; Pile Type-39=No; Pile Type-40=No; Pile Type-41=No; Pile Type-42=No; Pile Type-43=No; Pile Type-44=No; Pile Type-45=No; Pile Type-46=No; Pile Type-47=No; Pile Type-48=No; Pile Type-49=No; Pile Type-50=No; Pile Type-51=No; Pile Type-52=No; Pile Type-53=No; Pile Type-54=No; Radius=500 mm  [stored 1.64042 ft]; Radius/2=250 mm  [stored 0.82021 ft]; band width=167 mm
- 26: ATK_1.25DIA_Circle_Radius=1250 mm  [stored 4.10105 ft]; ATK_2.5_DIA_Circle_Radius=2500 mm  [stored 8.2021 ft]; ATK_Pile_DIA=1000 mm  [stored 3.28084 ft]; Band Width 2=240 mm; Band Width 3=100 mm  [stored 0.328084 ft]; Depth=15000 mm  [stored 49.2126 ft]; Pile Type 01=No; Pile Type 02=No; Pile Type 03=No; Pile Type 04=No; Pile Type 05=No; Pile Type 06=No; Pile Type 07=No; Pile Type 08=No; Pile Type 09=No; Pile Type 10=No; Pile Type 11=No; Pile Type 12=No; Pile Type 13=No; Pile Type 14=No; Pile Type 15=No; Pile Type 16=No; Pile Type 17=No; Pile Type 18=No; Pile Type 19=No; Pile Type 20=No; Pile Type 21=No; Pile Type 22=No; Pile Type 23=No; Pile Type 24=No; Pile Type 25=No; Pile Type 26=Yes; Pile Type 27=No; Pile Type 28=No; Pile Type 29=No; Pile Type 30=No; Pile Type 31=No; Pile Type-32=No; Pile Type-33=No; Pile Type-34=No; Pile Type-35=No; Pile Type-36=No; Pile Type-37=No; Pile Type-38=No; Pile Type-39=No; Pile Type-40=No; Pile Type-41=No; Pile Type-42=No; Pile Type-43=No; Pile Type-44=No; Pile Type-45=No; Pile Type-46=No; Pile Type-47=No; Pile Type-48=No; Pile Type-49=No; Pile Type-50=No; Pile Type-51=No; Pile Type-52=No; Pile Type-53=No; Pile Type-54=No; Radius=500 mm  [stored 1.64042 ft]; Radius/2=250 mm  [stored 0.82021 ft]; band width=167 mm
- 25: ATK_1.25DIA_Circle_Radius=1250 mm  [stored 4.10105 ft]; ATK_2.5_DIA_Circle_Radius=2500 mm  [stored 8.2021 ft]; ATK_Pile_DIA=1000 mm  [stored 3.28084 ft]; Band Width 2=240 mm; Band Width 3=100 mm  [stored 0.328084 ft]; Depth=15000 mm  [stored 49.2126 ft]; Pile Type 01=No; Pile Type 02=No; Pile Type 03=No; Pile Type 04=No; Pile Type 05=No; Pile Type 06=No; Pile Type 07=No; Pile Type 08=No; Pile Type 09=No; Pile Type 10=No; Pile Type 11=No; Pile Type 12=No; Pile Type 13=No; Pile Type 14=No; Pile Type 15=No; Pile Type 16=No; Pile Type 17=No; Pile Type 18=No; Pile Type 19=No; Pile Type 20=No; Pile Type 21=No; Pile Type 22=No; Pile Type 23=No; Pile Type 24=No; Pile Type 25=Yes; Pile Type 26=No; Pile Type 27=No; Pile Type 28=No; Pile Type 29=No; Pile Type 30=No; Pile Type 31=No; Pile Type-32=No; Pile Type-33=No; Pile Type-34=No; Pile Type-35=No; Pile Type-36=No; Pile Type-37=No; Pile Type-38=No; Pile Type-39=No; Pile Type-40=No; Pile Type-41=No; Pile Type-42=No; Pile Type-43=No; Pile Type-44=No; Pile Type-45=No; Pile Type-46=No; Pile Type-47=No; Pile Type-48=No; Pile Type-49=No; Pile Type-50=No; Pile Type-51=No; Pile Type-52=No; Pile Type-53=No; Pile Type-54=No; Radius=500 mm  [stored 1.64042 ft]; Radius/2=250 mm  [stored 0.82021 ft]; band width=167 mm
- 24: ATK_1.25DIA_Circle_Radius=1250 mm  [stored 4.10105 ft]; ATK_2.5_DIA_Circle_Radius=2500 mm  [stored 8.2021 ft]; ATK_Pile_DIA=1000 mm  [stored 3.28084 ft]; Band Width 2=240 mm; Band Width 3=100 mm  [stored 0.328084 ft]; Depth=15000 mm  [stored 49.2126 ft]; Pile Type 01=No; Pile Type 02=No; Pile Type 03=No; Pile Type 04=No; Pile Type 05=No; Pile Type 06=No; Pile Type 07=No; Pile Type 08=No; Pile Type 09=No; Pile Type 10=No; Pile Type 11=No; Pile Type 12=No; Pile Type 13=No; Pile Type 14=No; Pile Type 15=No; Pile Type 16=No; Pile Type 17=No; Pile Type 18=No; Pile Type 19=No; Pile Type 20=No; Pile Type 21=No; Pile Type 22=No; Pile Type 23=No; Pile Type 24=Yes; Pile Type 25=No; Pile Type 26=No; Pile Type 27=No; Pile Type 28=No; Pile Type 29=No; Pile Type 30=No; Pile Type 31=No; Pile Type-32=No; Pile Type-33=No; Pile Type-34=No; Pile Type-35=No; Pile Type-36=No; Pile Type-37=No; Pile Type-38=No; Pile Type-39=No; Pile Type-40=No; Pile Type-41=No; Pile Type-42=No; Pile Type-43=No; Pile Type-44=No; Pile Type-45=No; Pile Type-46=No; Pile Type-47=No; Pile Type-48=No; Pile Type-49=No; Pile Type-50=No; Pile Type-51=No; Pile Type-52=No; Pile Type-53=No; Pile Type-54=No; Radius=500 mm  [stored 1.64042 ft]; Radius/2=250 mm  [stored 0.82021 ft]; band width=167 mm
- 23: ATK_1.25DIA_Circle_Radius=1250 mm  [stored 4.10105 ft]; ATK_2.5_DIA_Circle_Radius=2500 mm  [stored 8.2021 ft]; ATK_Pile_DIA=1000 mm  [stored 3.28084 ft]; Band Width 2=240 mm; Band Width 3=100 mm  [stored 0.328084 ft]; Depth=15000 mm  [stored 49.2126 ft]; Pile Type 01=No; Pile Type 02=No; Pile Type 03=No; Pile Type 04=No; Pile Type 05=No; Pile Type 06=No; Pile Type 07=No; Pile Type 08=No; Pile Type 09=No; Pile Type 10=No; Pile Type 11=No; Pile Type 12=No; Pile Type 13=No; Pile Type 14=No; Pile Type 15=No; Pile Type 16=No; Pile Type 17=No; Pile Type 18=No; Pile Type 19=No; Pile Type 20=No; Pile Type 21=No; Pile Type 22=No; Pile Type 23=Yes; Pile Type 24=No; Pile Type 25=No; Pile Type 26=No; Pile Type 27=No; Pile Type 28=No; Pile Type 29=No; Pile Type 30=No; Pile Type 31=No; Pile Type-32=No; Pile Type-33=No; Pile Type-34=No; Pile Type-35=No; Pile Type-36=No; Pile Type-37=No; Pile Type-38=No; Pile Type-39=No; Pile Type-40=No; Pile Type-41=No; Pile Type-42=No; Pile Type-43=No; Pile Type-44=No; Pile Type-45=No; Pile Type-46=No; Pile Type-47=No; Pile Type-48=No; Pile Type-49=No; Pile Type-50=No; Pile Type-51=No; Pile Type-52=No; Pile Type-53=No; Pile Type-54=No; Radius=500 mm  [stored 1.64042 ft]; Radius/2=250 mm  [stored 0.82021 ft]; band width=167 mm
- 22: ATK_1.25DIA_Circle_Radius=1250 mm  [stored 4.10105 ft]; ATK_2.5_DIA_Circle_Radius=2500 mm  [stored 8.2021 ft]; ATK_Pile_DIA=1000 mm  [stored 3.28084 ft]; Band Width 2=240 mm; Band Width 3=100 mm  [stored 0.328084 ft]; Depth=15000 mm  [stored 49.2126 ft]; Pile Type 01=No; Pile Type 02=No; Pile Type 03=No; Pile Type 04=No; Pile Type 05=No; Pile Type 06=No; Pile Type 07=No; Pile Type 08=No; Pile Type 09=No; Pile Type 10=No; Pile Type 11=No; Pile Type 12=No; Pile Type 13=No; Pile Type 14=No; Pile Type 15=No; Pile Type 16=No; Pile Type 17=No; Pile Type 18=No; Pile Type 19=No; Pile Type 20=No; Pile Type 21=No; Pile Type 22=Yes; Pile Type 23=No; Pile Type 24=No; Pile Type 25=No; Pile Type 26=No; Pile Type 27=No; Pile Type 28=Yes; Pile Type 29=No; Pile Type 30=No; Pile Type 31=No; Pile Type-32=No; Pile Type-33=No; Pile Type-34=No; Pile Type-35=No; Pile Type-36=No; Pile Type-37=No; Pile Type-38=No; Pile Type-39=No; Pile Type-40=No; Pile Type-41=No; Pile Type-42=No; Pile Type-43=No; Pile Type-44=No; Pile Type-45=No; Pile Type-46=No; Pile Type-47=No; Pile Type-48=No; Pile Type-49=No; Pile Type-50=No; Pile Type-51=No; Pile Type-52=No; Pile Type-53=No; Pile Type-54=No; Radius=500 mm  [stored 1.64042 ft]; Radius/2=250 mm  [stored 0.82021 ft]; band width=167 mm
- 21: ATK_1.25DIA_Circle_Radius=1250 mm  [stored 4.10105 ft]; ATK_2.5_DIA_Circle_Radius=2500 mm  [stored 8.2021 ft]; ATK_Pile_DIA=1000 mm  [stored 3.28084 ft]; Band Width 2=240 mm; Band Width 3=100 mm  [stored 0.328084 ft]; Depth=15000 mm  [stored 49.2126 ft]; Pile Type 01=No; Pile Type 02=No; Pile Type 03=No; Pile Type 04=No; Pile Type 05=No; Pile Type 06=No; Pile Type 07=No; Pile Type 08=No; Pile Type 09=No; Pile Type 10=No; Pile Type 11=No; Pile Type 12=No; Pile Type 13=No; Pile Type 14=No; Pile Type 15=No; Pile Type 16=No; Pile Type 17=No; Pile Type 18=No; Pile Type 19=No; Pile Type 20=No; Pile Type 21=Yes; Pile Type 22=No; Pile Type 23=No; Pile Type 24=No; Pile Type 25=No; Pile Type 26=No; Pile Type 27=No; Pile Type 28=No; Pile Type 29=No; Pile Type 30=No; Pile Type 31=No; Pile Type-32=No; Pile Type-33=No; Pile Type-34=No; Pile Type-35=No; Pile Type-36=No; Pile Type-37=No; Pile Type-38=No; Pile Type-39=No; Pile Type-40=No; Pile Type-41=No; Pile Type-42=No; Pile Type-43=No; Pile Type-44=No; Pile Type-45=No; Pile Type-46=No; Pile Type-47=No; Pile Type-48=No; Pile Type-49=No; Pile Type-50=No; Pile Type-51=No; Pile Type-52=No; Pile Type-53=No; Pile Type-54=No; Radius=500 mm  [stored 1.64042 ft]; Radius/2=250 mm  [stored 0.82021 ft]; band width=167 mm
- 20: ATK_1.25DIA_Circle_Radius=1250 mm  [stored 4.10105 ft]; ATK_2.5_DIA_Circle_Radius=2500 mm  [stored 8.2021 ft]; ATK_Pile_DIA=1000 mm  [stored 3.28084 ft]; Band Width 2=240 mm; Band Width 3=100 mm  [stored 0.328084 ft]; Depth=15000 mm  [stored 49.2126 ft]; Pile Type 01=No; Pile Type 02=No; Pile Type 03=No; Pile Type 04=No; Pile Type 05=No; Pile Type 06=No; Pile Type 07=No; Pile Type 08=No; Pile Type 09=No; Pile Type 10=No; Pile Type 11=No; Pile Type 12=No; Pile Type 13=No; Pile Type 14=No; Pile Type 15=No; Pile Type 16=No; Pile Type 17=No; Pile Type 18=No; Pile Type 19=No; Pile Type 20=Yes; Pile Type 21=No; Pile Type 22=No; Pile Type 23=No; Pile Type 24=No; Pile Type 25=No; Pile Type 26=No; Pile Type 27=No; Pile Type 28=No; Pile Type 29=No; Pile Type 30=No; Pile Type 31=No; Pile Type-32=No; Pile Type-33=No; Pile Type-34=No; Pile Type-35=No; Pile Type-36=No; Pile Type-37=No; Pile Type-38=No; Pile Type-39=No; Pile Type-40=No; Pile Type-41=No; Pile Type-42=No; Pile Type-43=No; Pile Type-44=No; Pile Type-45=No; Pile Type-46=No; Pile Type-47=No; Pile Type-48=No; Pile Type-49=No; Pile Type-50=No; Pile Type-51=No; Pile Type-52=No; Pile Type-53=No; Pile Type-54=No; Radius=500 mm  [stored 1.64042 ft]; Radius/2=250 mm  [stored 0.82021 ft]; band width=167 mm
- 19: ATK_1.25DIA_Circle_Radius=1250 mm  [stored 4.10105 ft]; ATK_2.5_DIA_Circle_Radius=2500 mm  [stored 8.2021 ft]; ATK_Pile_DIA=1000 mm  [stored 3.28084 ft]; Band Width 2=240 mm; Band Width 3=100 mm  [stored 0.328084 ft]; Depth=15000 mm  [stored 49.2126 ft]; Pile Type 01=No; Pile Type 02=No; Pile Type 03=No; Pile Type 04=No; Pile Type 05=No; Pile Type 06=No; Pile Type 07=No; Pile Type 08=No; Pile Type 09=No; Pile Type 10=No; Pile Type 11=No; Pile Type 12=No; Pile Type 13=No; Pile Type 14=No; Pile Type 15=No; Pile Type 16=No; Pile Type 17=No; Pile Type 18=No; Pile Type 19=Yes; Pile Type 20=No; Pile Type 21=No; Pile Type 22=No; Pile Type 23=No; Pile Type 24=No; Pile Type 25=No; Pile Type 26=No; Pile Type 27=No; Pile Type 28=No; Pile Type 29=No; Pile Type 30=No; Pile Type 31=No; Pile Type-32=No; Pile Type-33=No; Pile Type-34=No; Pile Type-35=No; Pile Type-36=No; Pile Type-37=No; Pile Type-38=No; Pile Type-39=No; Pile Type-40=No; Pile Type-41=No; Pile Type-42=No; Pile Type-43=No; Pile Type-44=No; Pile Type-45=No; Pile Type-46=No; Pile Type-47=No; Pile Type-48=No; Pile Type-49=No; Pile Type-50=No; Pile Type-51=No; Pile Type-52=No; Pile Type-53=No; Pile Type-54=No; Radius=500 mm  [stored 1.64042 ft]; Radius/2=250 mm  [stored 0.82021 ft]; band width=167 mm
- 18: ATK_1.25DIA_Circle_Radius=1250 mm  [stored 4.10105 ft]; ATK_2.5_DIA_Circle_Radius=2500 mm  [stored 8.2021 ft]; ATK_Pile_DIA=1000 mm  [stored 3.28084 ft]; Band Width 2=240 mm; Band Width 3=100 mm  [stored 0.328084 ft]; Depth=15000 mm  [stored 49.2126 ft]; Pile Type 01=No; Pile Type 02=No; Pile Type 03=No; Pile Type 04=No; Pile Type 05=No; Pile Type 06=No; Pile Type 07=No; Pile Type 08=No; Pile Type 09=No; Pile Type 10=No; Pile Type 11=No; Pile Type 12=No; Pile Type 13=No; Pile Type 14=No; Pile Type 15=No; Pile Type 16=No; Pile Type 17=No; Pile Type 18=Yes; Pile Type 19=No; Pile Type 20=No; Pile Type 21=No; Pile Type 22=No; Pile Type 23=No; Pile Type 24=No; Pile Type 25=No; Pile Type 26=No; Pile Type 27=No; Pile Type 28=No; Pile Type 29=No; Pile Type 30=No; Pile Type 31=No; Pile Type-32=No; Pile Type-33=No; Pile Type-34=No; Pile Type-35=No; Pile Type-36=No; Pile Type-37=No; Pile Type-38=No; Pile Type-39=No; Pile Type-40=No; Pile Type-41=No; Pile Type-42=No; Pile Type-43=No; Pile Type-44=No; Pile Type-45=No; Pile Type-46=No; Pile Type-47=No; Pile Type-48=No; Pile Type-49=No; Pile Type-50=No; Pile Type-51=No; Pile Type-52=No; Pile Type-53=No; Pile Type-54=No; Radius=500 mm  [stored 1.64042 ft]; Radius/2=250 mm  [stored 0.82021 ft]; band width=167 mm
- 17: ATK_1.25DIA_Circle_Radius=1250 mm  [stored 4.10105 ft]; ATK_2.5_DIA_Circle_Radius=2500 mm  [stored 8.2021 ft]; ATK_Pile_DIA=1000 mm  [stored 3.28084 ft]; Band Width 2=240 mm; Band Width 3=100 mm  [stored 0.328084 ft]; Depth=15000 mm  [stored 49.2126 ft]; Pile Type 01=No; Pile Type 02=No; Pile Type 03=No; Pile Type 04=No; Pile Type 05=No; Pile Type 06=No; Pile Type 07=No; Pile Type 08=No; Pile Type 09=No; Pile Type 10=No; Pile Type 11=No; Pile Type 12=No; Pile Type 13=No; Pile Type 14=No; Pile Type 15=No; Pile Type 16=No; Pile Type 17=Yes; Pile Type 18=No; Pile Type 19=No; Pile Type 20=No; Pile Type 21=No; Pile Type 22=No; Pile Type 23=No; Pile Type 24=No; Pile Type 25=No; Pile Type 26=No; Pile Type 27=No; Pile Type 28=No; Pile Type 29=No; Pile Type 30=No; Pile Type 31=No; Pile Type-32=No; Pile Type-33=No; Pile Type-34=No; Pile Type-35=No; Pile Type-36=No; Pile Type-37=No; Pile Type-38=No; Pile Type-39=No; Pile Type-40=No; Pile Type-41=No; Pile Type-42=No; Pile Type-43=No; Pile Type-44=No; Pile Type-45=No; Pile Type-46=No; Pile Type-47=No; Pile Type-48=No; Pile Type-49=No; Pile Type-50=No; Pile Type-51=No; Pile Type-52=No; Pile Type-53=No; Pile Type-54=No; Radius=500 mm  [stored 1.64042 ft]; Radius/2=250 mm  [stored 0.82021 ft]; band width=167 mm
- 16: ATK_1.25DIA_Circle_Radius=1250 mm  [stored 4.10105 ft]; ATK_2.5_DIA_Circle_Radius=2500 mm  [stored 8.2021 ft]; ATK_Pile_DIA=1000 mm  [stored 3.28084 ft]; Band Width 2=240 mm; Band Width 3=100 mm  [stored 0.328084 ft]; Depth=15000 mm  [stored 49.2126 ft]; Pile Type 01=No; Pile Type 02=No; Pile Type 03=No; Pile Type 04=No; Pile Type 05=No; Pile Type 06=No; Pile Type 07=No; Pile Type 08=No; Pile Type 09=No; Pile Type 10=No; Pile Type 11=No; Pile Type 12=No; Pile Type 13=No; Pile Type 14=No; Pile Type 15=No; Pile Type 16=Yes; Pile Type 17=No; Pile Type 18=No; Pile Type 19=No; Pile Type 20=No; Pile Type 21=No; Pile Type 22=No; Pile Type 23=No; Pile Type 24=No; Pile Type 25=No; Pile Type 26=No; Pile Type 27=No; Pile Type 28=No; Pile Type 29=No; Pile Type 30=No; Pile Type 31=No; Pile Type-32=No; Pile Type-33=No; Pile Type-34=No; Pile Type-35=No; Pile Type-36=No; Pile Type-37=No; Pile Type-38=No; Pile Type-39=No; Pile Type-40=No; Pile Type-41=No; Pile Type-42=No; Pile Type-43=No; Pile Type-44=No; Pile Type-45=No; Pile Type-46=No; Pile Type-47=No; Pile Type-48=No; Pile Type-49=No; Pile Type-50=No; Pile Type-51=No; Pile Type-52=No; Pile Type-53=No; Pile Type-54=No; Radius=500 mm  [stored 1.64042 ft]; Radius/2=250 mm  [stored 0.82021 ft]; band width=167 mm
- 15: ATK_1.25DIA_Circle_Radius=1250 mm  [stored 4.10105 ft]; ATK_2.5_DIA_Circle_Radius=2500 mm  [stored 8.2021 ft]; ATK_Pile_DIA=1000 mm  [stored 3.28084 ft]; Band Width 2=240 mm; Band Width 3=100 mm  [stored 0.328084 ft]; Depth=15000 mm  [stored 49.2126 ft]; Pile Type 01=No; Pile Type 02=No; Pile Type 03=No; Pile Type 04=No; Pile Type 05=No; Pile Type 06=No; Pile Type 07=No; Pile Type 08=No; Pile Type 09=No; Pile Type 10=No; Pile Type 11=No; Pile Type 12=No; Pile Type 13=No; Pile Type 14=No; Pile Type 15=Yes; Pile Type 16=No; Pile Type 17=No; Pile Type 18=No; Pile Type 19=No; Pile Type 20=No; Pile Type 21=No; Pile Type 22=No; Pile Type 23=No; Pile Type 24=No; Pile Type 25=No; Pile Type 26=No; Pile Type 27=No; Pile Type 28=No; Pile Type 29=No; Pile Type 30=No; Pile Type 31=No; Pile Type-32=No; Pile Type-33=No; Pile Type-34=No; Pile Type-35=No; Pile Type-36=No; Pile Type-37=No; Pile Type-38=No; Pile Type-39=No; Pile Type-40=No; Pile Type-41=No; Pile Type-42=No; Pile Type-43=No; Pile Type-44=No; Pile Type-45=No; Pile Type-46=No; Pile Type-47=No; Pile Type-48=No; Pile Type-49=No; Pile Type-50=No; Pile Type-51=No; Pile Type-52=No; Pile Type-53=No; Pile Type-54=No; Radius=500 mm  [stored 1.64042 ft]; Radius/2=250 mm  [stored 0.82021 ft]; band width=167 mm
- 14: ATK_1.25DIA_Circle_Radius=1250 mm  [stored 4.10105 ft]; ATK_2.5_DIA_Circle_Radius=2500 mm  [stored 8.2021 ft]; ATK_Pile_DIA=1000 mm  [stored 3.28084 ft]; Band Width 2=240 mm; Band Width 3=100 mm  [stored 0.328084 ft]; Depth=15000 mm  [stored 49.2126 ft]; Pile Type 01=No; Pile Type 02=No; Pile Type 03=No; Pile Type 04=No; Pile Type 05=No; Pile Type 06=No; Pile Type 07=No; Pile Type 08=No; Pile Type 09=No; Pile Type 10=No; Pile Type 11=No; Pile Type 12=No; Pile Type 13=No; Pile Type 14=Yes; Pile Type 15=No; Pile Type 16=No; Pile Type 17=No; Pile Type 18=No; Pile Type 19=No; Pile Type 20=No; Pile Type 21=No; Pile Type 22=No; Pile Type 23=No; Pile Type 24=No; Pile Type 25=No; Pile Type 26=No; Pile Type 27=No; Pile Type 28=No; Pile Type 29=No; Pile Type 30=No; Pile Type 31=No; Pile Type-32=No; Pile Type-33=No; Pile Type-34=No; Pile Type-35=No; Pile Type-36=No; Pile Type-37=No; Pile Type-38=No; Pile Type-39=No; Pile Type-40=No; Pile Type-41=No; Pile Type-42=No; Pile Type-43=No; Pile Type-44=No; Pile Type-45=No; Pile Type-46=No; Pile Type-47=No; Pile Type-48=No; Pile Type-49=No; Pile Type-50=No; Pile Type-51=No; Pile Type-52=No; Pile Type-53=No; Pile Type-54=No; Radius=500 mm  [stored 1.64042 ft]; Radius/2=250 mm  [stored 0.82021 ft]; band width=167 mm
- 13: ATK_1.25DIA_Circle_Radius=1250 mm  [stored 4.10105 ft]; ATK_2.5_DIA_Circle_Radius=2500 mm  [stored 8.2021 ft]; ATK_Pile_DIA=1000 mm  [stored 3.28084 ft]; Band Width 2=240 mm; Band Width 3=100 mm  [stored 0.328084 ft]; Depth=15000 mm  [stored 49.2126 ft]; Pile Type 01=No; Pile Type 02=No; Pile Type 03=No; Pile Type 04=No; Pile Type 05=No; Pile Type 06=No; Pile Type 07=No; Pile Type 08=No; Pile Type 09=No; Pile Type 10=No; Pile Type 11=No; Pile Type 12=No; Pile Type 13=Yes; Pile Type 14=No; Pile Type 15=No; Pile Type 16=No; Pile Type 17=No; Pile Type 18=No; Pile Type 19=No; Pile Type 20=No; Pile Type 21=No; Pile Type 22=No; Pile Type 23=No; Pile Type 24=No; Pile Type 25=No; Pile Type 26=No; Pile Type 27=No; Pile Type 28=No; Pile Type 29=No; Pile Type 30=No; Pile Type 31=No; Pile Type-32=No; Pile Type-33=No; Pile Type-34=No; Pile Type-35=No; Pile Type-36=No; Pile Type-37=No; Pile Type-38=No; Pile Type-39=No; Pile Type-40=No; Pile Type-41=No; Pile Type-42=No; Pile Type-43=No; Pile Type-44=No; Pile Type-45=No; Pile Type-46=No; Pile Type-47=No; Pile Type-48=No; Pile Type-49=No; Pile Type-50=No; Pile Type-51=No; Pile Type-52=No; Pile Type-53=No; Pile Type-54=No; Radius=500 mm  [stored 1.64042 ft]; Radius/2=250 mm  [stored 0.82021 ft]; band width=167 mm
- 12: ATK_1.25DIA_Circle_Radius=1250 mm  [stored 4.10105 ft]; ATK_2.5_DIA_Circle_Radius=2500 mm  [stored 8.2021 ft]; ATK_Pile_DIA=1000 mm  [stored 3.28084 ft]; Band Width 2=240 mm; Band Width 3=100 mm  [stored 0.328084 ft]; Depth=15000 mm  [stored 49.2126 ft]; Pile Type 01=No; Pile Type 02=No; Pile Type 03=No; Pile Type 04=No; Pile Type 05=No; Pile Type 06=No; Pile Type 07=No; Pile Type 08=No; Pile Type 09=No; Pile Type 10=No; Pile Type 11=No; Pile Type 12=Yes; Pile Type 13=No; Pile Type 14=No; Pile Type 15=No; Pile Type 16=No; Pile Type 17=No; Pile Type 18=No; Pile Type 19=No; Pile Type 20=No; Pile Type 21=No; Pile Type 22=No; Pile Type 23=No; Pile Type 24=No; Pile Type 25=No; Pile Type 26=No; Pile Type 27=No; Pile Type 28=No; Pile Type 29=No; Pile Type 30=No; Pile Type 31=No; Pile Type-32=No; Pile Type-33=No; Pile Type-34=No; Pile Type-35=No; Pile Type-36=No; Pile Type-37=No; Pile Type-38=No; Pile Type-39=No; Pile Type-40=No; Pile Type-41=No; Pile Type-42=No; Pile Type-43=No; Pile Type-44=No; Pile Type-45=No; Pile Type-46=No; Pile Type-47=No; Pile Type-48=No; Pile Type-49=No; Pile Type-50=No; Pile Type-51=No; Pile Type-52=No; Pile Type-53=No; Pile Type-54=No; Radius=500 mm  [stored 1.64042 ft]; Radius/2=250 mm  [stored 0.82021 ft]; band width=167 mm
- 11: ATK_1.25DIA_Circle_Radius=1250 mm  [stored 4.10105 ft]; ATK_2.5_DIA_Circle_Radius=2500 mm  [stored 8.2021 ft]; ATK_Pile_DIA=1000 mm  [stored 3.28084 ft]; Band Width 2=240 mm; Band Width 3=100 mm  [stored 0.328084 ft]; Depth=15000 mm  [stored 49.2126 ft]; Pile Type 01=No; Pile Type 02=No; Pile Type 03=No; Pile Type 04=No; Pile Type 05=No; Pile Type 06=No; Pile Type 07=No; Pile Type 08=No; Pile Type 09=No; Pile Type 10=No; Pile Type 11=No; Pile Type 12=Yes; Pile Type 13=No; Pile Type 14=Yes; Pile Type 15=No; Pile Type 16=No; Pile Type 17=No; Pile Type 18=No; Pile Type 19=No; Pile Type 20=No; Pile Type 21=No; Pile Type 22=No; Pile Type 23=No; Pile Type 24=No; Pile Type 25=No; Pile Type 26=No; Pile Type 27=No; Pile Type 28=No; Pile Type 29=No; Pile Type 30=No; Pile Type 31=No; Pile Type-32=No; Pile Type-33=No; Pile Type-34=No; Pile Type-35=No; Pile Type-36=No; Pile Type-37=No; Pile Type-38=No; Pile Type-39=No; Pile Type-40=No; Pile Type-41=No; Pile Type-42=No; Pile Type-43=No; Pile Type-44=No; Pile Type-45=No; Pile Type-46=No; Pile Type-47=No; Pile Type-48=No; Pile Type-49=No; Pile Type-50=No; Pile Type-51=No; Pile Type-52=No; Pile Type-53=No; Pile Type-54=No; Radius=500 mm  [stored 1.64042 ft]; Radius/2=250 mm  [stored 0.82021 ft]; band width=167 mm
- 10: ATK_1.25DIA_Circle_Radius=1250 mm  [stored 4.10105 ft]; ATK_2.5_DIA_Circle_Radius=2500 mm  [stored 8.2021 ft]; ATK_Pile_DIA=1000 mm  [stored 3.28084 ft]; Band Width 2=240 mm; Band Width 3=100 mm  [stored 0.328084 ft]; Depth=15000 mm  [stored 49.2126 ft]; Pile Type 01=No; Pile Type 02=No; Pile Type 03=No; Pile Type 04=No; Pile Type 05=No; Pile Type 06=No; Pile Type 07=No; Pile Type 08=No; Pile Type 09=No; Pile Type 10=Yes; Pile Type 11=No; Pile Type 12=No; Pile Type 13=No; Pile Type 14=No; Pile Type 15=No; Pile Type 16=No; Pile Type 17=No; Pile Type 18=No; Pile Type 19=No; Pile Type 20=No; Pile Type 21=No; Pile Type 22=No; Pile Type 23=No; Pile Type 24=No; Pile Type 25=No; Pile Type 26=No; Pile Type 27=No; Pile Type 28=No; Pile Type 29=No; Pile Type 30=No; Pile Type 31=No; Pile Type-32=No; Pile Type-33=No; Pile Type-34=No; Pile Type-35=No; Pile Type-36=No; Pile Type-37=No; Pile Type-38=No; Pile Type-39=No; Pile Type-40=No; Pile Type-41=No; Pile Type-42=No; Pile Type-43=No; Pile Type-44=No; Pile Type-45=No; Pile Type-46=No; Pile Type-47=No; Pile Type-48=No; Pile Type-49=No; Pile Type-50=No; Pile Type-51=No; Pile Type-52=No; Pile Type-53=No; Pile Type-54=No; Radius=500 mm  [stored 1.64042 ft]; Radius/2=250 mm  [stored 0.82021 ft]; band width=167 mm
- 9: ATK_1.25DIA_Circle_Radius=1250 mm  [stored 4.10105 ft]; ATK_2.5_DIA_Circle_Radius=2500 mm  [stored 8.2021 ft]; ATK_Pile_DIA=1000 mm  [stored 3.28084 ft]; Band Width 2=240 mm; Band Width 3=100 mm  [stored 0.328084 ft]; Depth=15000 mm  [stored 49.2126 ft]; Pile Type 01=No; Pile Type 02=No; Pile Type 03=No; Pile Type 04=No; Pile Type 05=No; Pile Type 06=No; Pile Type 07=No; Pile Type 08=No; Pile Type 09=Yes; Pile Type 10=No; Pile Type 11=No; Pile Type 12=No; Pile Type 13=No; Pile Type 14=No; Pile Type 15=No; Pile Type 16=No; Pile Type 17=No; Pile Type 18=No; Pile Type 19=No; Pile Type 20=No; Pile Type 21=No; Pile Type 22=No; Pile Type 23=No; Pile Type 24=No; Pile Type 25=No; Pile Type 26=No; Pile Type 27=No; Pile Type 28=No; Pile Type 29=No; Pile Type 30=No; Pile Type 31=No; Pile Type-32=No; Pile Type-33=No; Pile Type-34=No; Pile Type-35=No; Pile Type-36=No; Pile Type-37=No; Pile Type-38=No; Pile Type-39=No; Pile Type-40=No; Pile Type-41=No; Pile Type-42=No; Pile Type-43=No; Pile Type-44=No; Pile Type-45=No; Pile Type-46=No; Pile Type-47=No; Pile Type-48=No; Pile Type-49=No; Pile Type-50=No; Pile Type-51=No; Pile Type-52=No; Pile Type-53=No; Pile Type-54=No; Radius=500 mm  [stored 1.64042 ft]; Radius/2=250 mm  [stored 0.82021 ft]; band width=167 mm
- 8: ATK_1.25DIA_Circle_Radius=1250 mm  [stored 4.10105 ft]; ATK_2.5_DIA_Circle_Radius=2500 mm  [stored 8.2021 ft]; ATK_Pile_DIA=1000 mm  [stored 3.28084 ft]; Band Width 2=240 mm; Band Width 3=100 mm  [stored 0.328084 ft]; Depth=15000 mm  [stored 49.2126 ft]; Pile Type 01=No; Pile Type 02=No; Pile Type 03=No; Pile Type 04=No; Pile Type 05=No; Pile Type 06=No; Pile Type 07=No; Pile Type 08=Yes; Pile Type 09=No; Pile Type 10=No; Pile Type 11=No; Pile Type 12=No; Pile Type 13=No; Pile Type 14=No; Pile Type 15=No; Pile Type 16=No; Pile Type 17=No; Pile Type 18=No; Pile Type 19=No; Pile Type 20=No; Pile Type 21=No; Pile Type 22=No; Pile Type 23=No; Pile Type 24=No; Pile Type 25=No; Pile Type 26=No; Pile Type 27=No; Pile Type 28=No; Pile Type 29=No; Pile Type 30=No; Pile Type 31=No; Pile Type-32=No; Pile Type-33=No; Pile Type-34=No; Pile Type-35=No; Pile Type-36=No; Pile Type-37=No; Pile Type-38=No; Pile Type-39=No; Pile Type-40=No; Pile Type-41=No; Pile Type-42=No; Pile Type-43=No; Pile Type-44=No; Pile Type-45=No; Pile Type-46=No; Pile Type-47=No; Pile Type-48=No; Pile Type-49=No; Pile Type-50=No; Pile Type-51=No; Pile Type-52=No; Pile Type-53=No; Pile Type-54=No; Radius=500 mm  [stored 1.64042 ft]; Radius/2=250 mm  [stored 0.82021 ft]; band width=167 mm
- 7: ATK_1.25DIA_Circle_Radius=1250 mm  [stored 4.10105 ft]; ATK_2.5_DIA_Circle_Radius=2500 mm  [stored 8.2021 ft]; ATK_Pile_DIA=1000 mm  [stored 3.28084 ft]; Band Width 2=240 mm; Band Width 3=100 mm  [stored 0.328084 ft]; Depth=15000 mm  [stored 49.2126 ft]; Pile Type 01=No; Pile Type 02=No; Pile Type 03=No; Pile Type 04=No; Pile Type 05=No; Pile Type 06=No; Pile Type 07=Yes; Pile Type 08=No; Pile Type 09=No; Pile Type 10=No; Pile Type 11=No; Pile Type 12=No; Pile Type 13=No; Pile Type 14=No; Pile Type 15=No; Pile Type 16=No; Pile Type 17=No; Pile Type 18=No; Pile Type 19=No; Pile Type 20=No; Pile Type 21=No; Pile Type 22=No; Pile Type 23=No; Pile Type 24=No; Pile Type 25=No; Pile Type 26=No; Pile Type 27=No; Pile Type 28=No; Pile Type 29=No; Pile Type 30=No; Pile Type 31=No; Pile Type-32=No; Pile Type-33=No; Pile Type-34=No; Pile Type-35=No; Pile Type-36=No; Pile Type-37=No; Pile Type-38=No; Pile Type-39=No; Pile Type-40=No; Pile Type-41=No; Pile Type-42=No; Pile Type-43=No; Pile Type-44=No; Pile Type-45=No; Pile Type-46=No; Pile Type-47=No; Pile Type-48=No; Pile Type-49=No; Pile Type-50=No; Pile Type-51=No; Pile Type-52=No; Pile Type-53=No; Pile Type-54=No; Radius=500 mm  [stored 1.64042 ft]; Radius/2=250 mm  [stored 0.82021 ft]; band width=167 mm
- 6: ATK_1.25DIA_Circle_Radius=1250 mm  [stored 4.10105 ft]; ATK_2.5_DIA_Circle_Radius=2500 mm  [stored 8.2021 ft]; ATK_Pile_DIA=1000 mm  [stored 3.28084 ft]; Band Width 2=240 mm; Band Width 3=100 mm  [stored 0.328084 ft]; Depth=15000 mm  [stored 49.2126 ft]; Pile Type 01=No; Pile Type 02=No; Pile Type 03=No; Pile Type 04=No; Pile Type 05=No; Pile Type 06=Yes; Pile Type 07=No; Pile Type 08=No; Pile Type 09=No; Pile Type 10=No; Pile Type 11=No; Pile Type 12=No; Pile Type 13=No; Pile Type 14=No; Pile Type 15=No; Pile Type 16=No; Pile Type 17=No; Pile Type 18=No; Pile Type 19=No; Pile Type 20=No; Pile Type 21=No; Pile Type 22=No; Pile Type 23=No; Pile Type 24=No; Pile Type 25=No; Pile Type 26=No; Pile Type 27=No; Pile Type 28=No; Pile Type 29=No; Pile Type 30=No; Pile Type 31=No; Pile Type-32=No; Pile Type-33=No; Pile Type-34=No; Pile Type-35=No; Pile Type-36=No; Pile Type-37=No; Pile Type-38=No; Pile Type-39=No; Pile Type-40=No; Pile Type-41=No; Pile Type-42=No; Pile Type-43=No; Pile Type-44=No; Pile Type-45=No; Pile Type-46=No; Pile Type-47=No; Pile Type-48=No; Pile Type-49=No; Pile Type-50=No; Pile Type-51=No; Pile Type-52=No; Pile Type-53=No; Pile Type-54=No; Radius=500 mm  [stored 1.64042 ft]; Radius/2=250 mm  [stored 0.82021 ft]; band width=167 mm
- 5: ATK_1.25DIA_Circle_Radius=1250 mm  [stored 4.10105 ft]; ATK_2.5_DIA_Circle_Radius=2500 mm  [stored 8.2021 ft]; ATK_Pile_DIA=1000 mm  [stored 3.28084 ft]; Band Width 2=240 mm; Band Width 3=100 mm  [stored 0.328084 ft]; Depth=15000 mm  [stored 49.2126 ft]; Pile Type 01=No; Pile Type 02=No; Pile Type 03=No; Pile Type 04=No; Pile Type 05=Yes; Pile Type 06=No; Pile Type 07=No; Pile Type 08=No; Pile Type 09=No; Pile Type 10=No; Pile Type 11=No; Pile Type 12=No; Pile Type 13=No; Pile Type 14=No; Pile Type 15=No; Pile Type 16=No; Pile Type 17=No; Pile Type 18=No; Pile Type 19=No; Pile Type 20=No; Pile Type 21=No; Pile Type 22=No; Pile Type 23=No; Pile Type 24=No; Pile Type 25=No; Pile Type 26=No; Pile Type 27=No; Pile Type 28=No; Pile Type 29=No; Pile Type 30=No; Pile Type 31=No; Pile Type-32=No; Pile Type-33=No; Pile Type-34=No; Pile Type-35=No; Pile Type-36=No; Pile Type-37=No; Pile Type-38=No; Pile Type-39=No; Pile Type-40=No; Pile Type-41=No; Pile Type-42=No; Pile Type-43=No; Pile Type-44=No; Pile Type-45=No; Pile Type-46=No; Pile Type-47=No; Pile Type-48=No; Pile Type-49=No; Pile Type-50=No; Pile Type-51=No; Pile Type-52=No; Pile Type-53=No; Pile Type-54=No; Radius=500 mm  [stored 1.64042 ft]; Radius/2=250 mm  [stored 0.82021 ft]; band width=167 mm
- 4: ATK_1.25DIA_Circle_Radius=1250 mm  [stored 4.10105 ft]; ATK_2.5_DIA_Circle_Radius=2500 mm  [stored 8.2021 ft]; ATK_Pile_DIA=1000 mm  [stored 3.28084 ft]; Band Width 2=240 mm; Band Width 3=100 mm  [stored 0.328084 ft]; Depth=15000 mm  [stored 49.2126 ft]; Pile Type 01=No; Pile Type 02=No; Pile Type 03=No; Pile Type 04=Yes; Pile Type 05=No; Pile Type 06=No; Pile Type 07=No; Pile Type 08=No; Pile Type 09=No; Pile Type 10=No; Pile Type 11=No; Pile Type 12=No; Pile Type 13=No; Pile Type 14=No; Pile Type 15=No; Pile Type 16=No; Pile Type 17=No; Pile Type 18=No; Pile Type 19=No; Pile Type 20=No; Pile Type 21=No; Pile Type 22=No; Pile Type 23=No; Pile Type 24=No; Pile Type 25=No; Pile Type 26=No; Pile Type 27=No; Pile Type 28=No; Pile Type 29=No; Pile Type 30=No; Pile Type 31=No; Pile Type-32=No; Pile Type-33=No; Pile Type-34=No; Pile Type-35=No; Pile Type-36=No; Pile Type-37=No; Pile Type-38=No; Pile Type-39=No; Pile Type-40=No; Pile Type-41=No; Pile Type-42=No; Pile Type-43=No; Pile Type-44=No; Pile Type-45=No; Pile Type-46=No; Pile Type-47=No; Pile Type-48=No; Pile Type-49=No; Pile Type-50=No; Pile Type-51=No; Pile Type-52=No; Pile Type-53=No; Pile Type-54=No; Radius=500 mm  [stored 1.64042 ft]; Radius/2=250 mm  [stored 0.82021 ft]; band width=167 mm
- 3: ATK_1.25DIA_Circle_Radius=1250 mm  [stored 4.10105 ft]; ATK_2.5_DIA_Circle_Radius=2500 mm  [stored 8.2021 ft]; ATK_Pile_DIA=1000 mm  [stored 3.28084 ft]; Band Width 2=240 mm; Band Width 3=100 mm  [stored 0.328084 ft]; Depth=15000 mm  [stored 49.2126 ft]; Pile Type 01=No; Pile Type 02=No; Pile Type 03=Yes; Pile Type 04=No; Pile Type 05=No; Pile Type 06=No; Pile Type 07=No; Pile Type 08=No; Pile Type 09=No; Pile Type 10=No; Pile Type 11=No; Pile Type 12=No; Pile Type 13=No; Pile Type 14=No; Pile Type 15=No; Pile Type 16=No; Pile Type 17=No; Pile Type 18=No; Pile Type 19=No; Pile Type 20=No; Pile Type 21=No; Pile Type 22=No; Pile Type 23=No; Pile Type 24=No; Pile Type 25=No; Pile Type 26=No; Pile Type 27=No; Pile Type 28=No; Pile Type 29=No; Pile Type 30=No; Pile Type 31=No; Pile Type-32=No; Pile Type-33=No; Pile Type-34=No; Pile Type-35=No; Pile Type-36=No; Pile Type-37=No; Pile Type-38=No; Pile Type-39=No; Pile Type-40=No; Pile Type-41=No; Pile Type-42=No; Pile Type-43=No; Pile Type-44=No; Pile Type-45=No; Pile Type-46=No; Pile Type-47=No; Pile Type-48=No; Pile Type-49=No; Pile Type-50=No; Pile Type-51=No; Pile Type-52=No; Pile Type-53=No; Pile Type-54=No; Radius=500 mm  [stored 1.64042 ft]; Radius/2=250 mm  [stored 0.82021 ft]; band width=167 mm
- 2: ATK_1.25DIA_Circle_Radius=1250 mm  [stored 4.10105 ft]; ATK_2.5_DIA_Circle_Radius=2500 mm  [stored 8.2021 ft]; ATK_Pile_DIA=1000 mm  [stored 3.28084 ft]; Band Width 2=240 mm; Band Width 3=100 mm  [stored 0.328084 ft]; Depth=15000 mm  [stored 49.2126 ft]; Pile Type 01=No; Pile Type 02=Yes; Pile Type 03=No; Pile Type 04=No; Pile Type 05=No; Pile Type 06=No; Pile Type 07=No; Pile Type 08=No; Pile Type 09=No; Pile Type 10=No; Pile Type 11=No; Pile Type 12=No; Pile Type 13=No; Pile Type 14=No; Pile Type 15=No; Pile Type 16=No; Pile Type 17=No; Pile Type 18=No; Pile Type 19=No; Pile Type 20=No; Pile Type 21=No; Pile Type 22=No; Pile Type 23=No; Pile Type 24=No; Pile Type 25=No; Pile Type 26=No; Pile Type 27=No; Pile Type 28=No; Pile Type 29=No; Pile Type 30=No; Pile Type 31=No; Pile Type-32=No; Pile Type-33=No; Pile Type-34=No; Pile Type-35=No; Pile Type-36=No; Pile Type-37=No; Pile Type-38=No; Pile Type-39=No; Pile Type-40=No; Pile Type-41=No; Pile Type-42=No; Pile Type-43=No; Pile Type-44=No; Pile Type-45=No; Pile Type-46=No; Pile Type-47=No; Pile Type-48=No; Pile Type-49=No; Pile Type-50=No; Pile Type-51=No; Pile Type-52=No; Pile Type-53=No; Pile Type-54=No; Radius=500 mm  [stored 1.64042 ft]; Radius/2=250 mm  [stored 0.82021 ft]; band width=167 mm
- 1: ATK_1.25DIA_Circle_Radius=1250 mm  [stored 4.10105 ft]; ATK_2.5_DIA_Circle_Radius=2500 mm  [stored 8.2021 ft]; ATK_Pile_DIA=1000 mm  [stored 3.28084 ft]; Band Width 2=240 mm; Band Width 3=100 mm  [stored 0.328084 ft]; Depth=15000 mm  [stored 49.2126 ft]; Pile Type 01=Yes; Pile Type 02=No; Pile Type 03=No; Pile Type 04=No; Pile Type 05=No; Pile Type 06=No; Pile Type 07=No; Pile Type 08=No; Pile Type 09=No; Pile Type 10=No; Pile Type 11=No; Pile Type 12=No; Pile Type 13=No; Pile Type 14=No; Pile Type 15=No; Pile Type 16=No; Pile Type 17=No; Pile Type 18=No; Pile Type 19=No; Pile Type 20=No; Pile Type 21=No; Pile Type 22=No; Pile Type 23=No; Pile Type 24=No; Pile Type 25=No; Pile Type 26=No; Pile Type 27=No; Pile Type 28=No; Pile Type 29=No; Pile Type 30=No; Pile Type 31=No; Pile Type-32=No; Pile Type-33=No; Pile Type-34=No; Pile Type-35=No; Pile Type-36=No; Pile Type-37=No; Pile Type-38=No; Pile Type-39=No; Pile Type-40=No; Pile Type-41=No; Pile Type-42=No; Pile Type-43=No; Pile Type-44=No; Pile Type-45=No; Pile Type-46=No; Pile Type-47=No; Pile Type-48=No; Pile Type-49=No; Pile Type-50=No; Pile Type-51=No; Pile Type-52=No; Pile Type-53=No; Pile Type-54=No; Radius=500 mm  [stored 1.64042 ft]; Radius/2=250 mm  [stored 0.82021 ft]; band width=167 mm

note: [stored X ft] marks values corroborated as IEEE doubles in the binary element streams (Revit-internal decimal feet)
